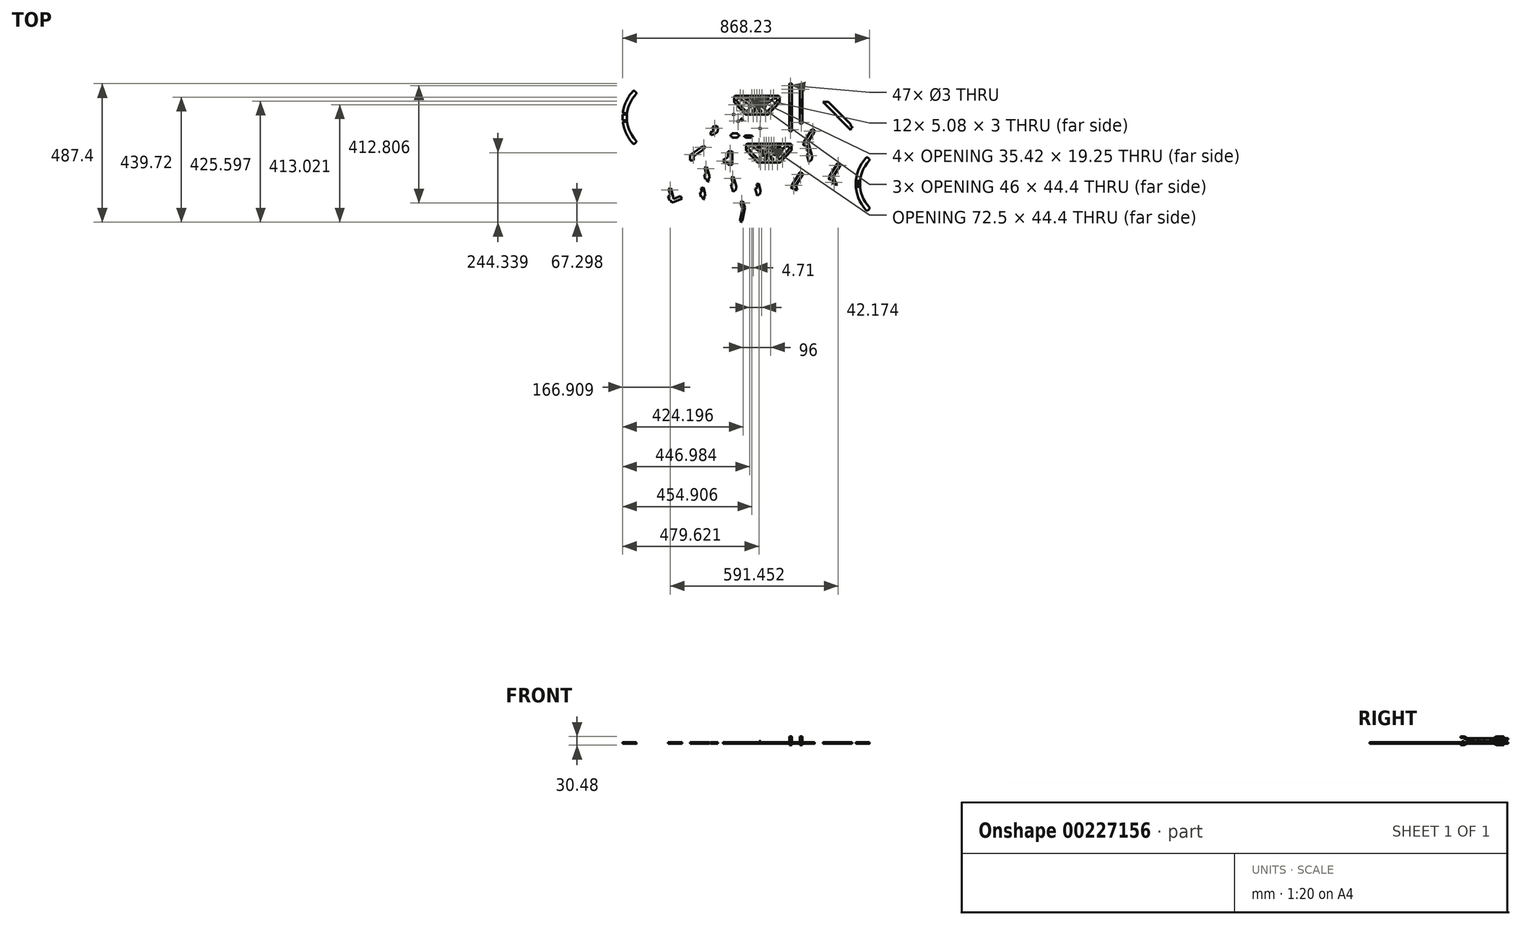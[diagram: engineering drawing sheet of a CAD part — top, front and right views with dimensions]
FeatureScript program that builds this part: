
annotation { "Feature Type Name" : "Feature", "Feature Type Description" : "" }
export const myFeature = defineFeature(function(context is Context, id is Id, definition is map)
    precondition{}
    {
        {
            var Q0;
            Q0=qCreatedBy(makeId("Top.planeOp"),FACE);
            var sketch = newSketch(context, id + "F0", { "sketchPlane" : qUnion([Q0])});
            skLineSegment(sketch, "E0.bottom", {"start": v(11.13, 62.94) * mm, "end": v(-148.87, 62.94) * mm});
            skLineSegment(sketch, "E0.top", {"start": v(11.13, 53.94) * mm, "end": v(-148.87, 53.94) * mm});
            skLineSegment(sketch, "E0.left", {"start": v(11.13, 62.94) * mm, "end": v(11.13, 53.94) * mm});
            skLineSegment(sketch, "E0.right", {"start": v(-148.87, 62.94) * mm, "end": v(-148.87, 53.94) * mm});
            skCircle(sketch, "E1", {"center": v(-127.12, 58.44) * mm, "radius": 1.5 * mm});
            skLineSegment(sketch, "E2.bottom", {"start": v(-43.87, 30.69) * mm, "end": v(-93.87, 30.69) * mm});
            skLineSegment(sketch, "E2.top", {"start": v(-43.87, 21.69) * mm, "end": v(-93.87, 21.69) * mm});
            skLineSegment(sketch, "E2.left", {"start": v(-43.87, 30.69) * mm, "end": v(-43.87, 21.69) * mm});
            skLineSegment(sketch, "E2.right", {"start": v(-93.87, 30.69) * mm, "end": v(-93.87, 21.69) * mm});
            skPoint(sketch, "E2.centerSnap0", {"position": v(-68.87, 53.94) * mm});
            skLineSegment(sketch, "E3", {"start": v(-76.37, 30.69) * mm, "end": v(-76.37, 53.94) * mm});
            skLineSegment(sketch, "E4", {"start": v(-68.87, 62.94) * mm, "end": v(-68.87, 21.69) * mm, "construction": true});
            skLineSegment(sketch, "E5.MirrorCS", {"start": v(-61.37, 30.69) * mm, "end": v(-61.37, 53.94) * mm});
            skPoint(sketch, "E6.centerSnap0", {"position": v(-93.87, 26.19) * mm});
            skCircle(sketch, "E7.MirrorC", {"center": v(-88, 26.19) * mm, "radius": 1.5 * mm});
            skCircle(sketch, "E8", {"center": v(-10.62, 58.44) * mm, "radius": 1.5 * mm});
            skLineSegment(sketch, "E9", {"start": v(-127.12, 58.44) * mm, "end": v(-10.62, 58.44) * mm, "construction": true});
            skLineSegment(sketch, "E10.bottom", {"start": v(-41.37, 6.69) * mm, "end": v(-96.37, 6.69) * mm});
            skLineSegment(sketch, "E10.top", {"start": v(-41.37, -2.31) * mm, "end": v(-96.37, -2.31) * mm});
            skLineSegment(sketch, "E10.left", {"start": v(-41.37, 6.69) * mm, "end": v(-41.37, -2.31) * mm});
            skLineSegment(sketch, "E10.right", {"start": v(-96.37, 6.69) * mm, "end": v(-96.37, -2.31) * mm});
            skLineSegment(sketch, "E11", {"start": v(-76.37, 21.69) * mm, "end": v(-76.37, 6.69) * mm});
            skLineSegment(sketch, "E12", {"start": v(-61.37, 21.69) * mm, "end": v(-61.37, 6.69) * mm});
            skCircle(sketch, "E13", {"center": v(-98.87, 2.19) * mm, "radius": 1.5 * mm});
            skPoint(sketch, "E13.centerSnap0", {"position": v(-96.37, 2.19) * mm});
            skLineSegment(sketch, "E14", {"start": v(-68.87, 21.69) * mm, "end": v(-68.87, -2.31) * mm});
            skCircle(sketch, "E15.MirrorC", {"center": v(-38.87, 2.19) * mm, "radius": 1.5 * mm});
            skLineSegment(sketch, "E16", {"start": v(-96.37, -2.31) * mm, "end": v(-148.87, 53.94) * mm});
            skLineSegment(sketch, "E17", {"start": v(-109.55, -2.31) * mm, "end": v(-96.37, -2.31) * mm});
            skLineSegment(sketch, "E18", {"start": v(-96.37, 6.69) * mm, "end": v(-104.77, 6.69) * mm});
            skLineSegment(sketch, "E19.MirrorCS", {"start": v(-41.37, -2.31) * mm, "end": v(11.13, 53.94) * mm});
            skLineSegment(sketch, "E20.MirrorCS", {"start": v(-28.2, -2.31) * mm, "end": v(-41.37, -2.31) * mm});
            skLineSegment(sketch, "E21.MirrorCS", {"start": v(-41.37, 6.69) * mm, "end": v(-32.97, 6.69) * mm});
            skLineSegment(sketch, "E22", {"start": v(-43.87, 21.69) * mm, "end": v(-32.97, 6.69) * mm});
            skLineSegment(sketch, "E23", {"start": v(-55, 21.69) * mm, "end": v(-44.1, 6.69) * mm});
            skLineSegment(sketch, "E24.MirrorCS", {"start": v(-82.75, 21.69) * mm, "end": v(-93.65, 6.69) * mm});
            skLineSegment(sketch, "E25.MirrorCS", {"start": v(-93.87, 21.69) * mm, "end": v(-104.77, 6.69) * mm});
            skLineSegment(sketch, "E26", {"start": v(2.13, 53.94) * mm, "end": v(2.13, 44.3) * mm});
            skLineSegment(sketch, "E27", {"start": v(11.13, 53.94) * mm, "end": v(11.13, 40.8) * mm});
            skLineSegment(sketch, "E28", {"start": v(11.13, 40.8) * mm, "end": v(-28.2, -2.31) * mm});
            skLineSegment(sketch, "E29.MirrorCS", {"start": v(-148.87, 40.8) * mm, "end": v(-109.55, -2.31) * mm});
            skLineSegment(sketch, "E30.MirrorCS", {"start": v(-148.87, 53.94) * mm, "end": v(-148.87, 40.8) * mm});
            skLineSegment(sketch, "E31.MirrorCS", {"start": v(-139.87, 53.94) * mm, "end": v(-139.87, 44.3) * mm});
            skLineSegment(sketch, "E32", {"start": v(-93.87, 30.69) * mm, "end": v(-129.3, 53.94) * mm});
            skLineSegment(sketch, "E33.MirrorCS", {"start": v(-43.87, 30.69) * mm, "end": v(-8.45, 53.94) * mm});
            skLineSegment(sketch, "E34", {"start": v(-104.18, 6.06) * mm, "end": v(-104.18, -2.31) * mm});
            skLineSegment(sketch, "E35", {"start": v(-93.57, -2.31) * mm, "end": v(-93.57, 6.69) * mm});
            skLineSegment(sketch, "E36", {"start": v(-93.57, 6.69) * mm, "end": v(-82.67, 21.69) * mm});
            skLineSegment(sketch, "E37.MirrorCS", {"start": v(-44.18, 6.69) * mm, "end": v(-55.08, 21.69) * mm});
            skLineSegment(sketch, "E38", {"start": v(-44.18, 6.69) * mm, "end": v(-44.18, -2.31) * mm});
            skLineSegment(sketch, "E39", {"start": v(-93.57, -2.31) * mm, "end": v(-76.13, 21.69) * mm});
            skLineSegment(sketch, "E40.MirrorCS", {"start": v(-44.18, -2.31) * mm, "end": v(-61.62, 21.69) * mm});
            skPoint(sketch, "E41.endSnap0", {"position": v(-111.59, 42.31) * mm});
            skLineSegment(sketch, "E42", {"start": v(-76.37, 30.69) * mm, "end": v(-111.8, 53.94) * mm});
            skLineSegment(sketch, "E43.MirrorCS", {"start": v(-61.37, 30.69) * mm, "end": v(-25.95, 53.94) * mm});
            skCircle(sketch, "E44", {"center": v(-60.12, 58.44) * mm, "radius": 1.5 * mm});
            skCircle(sketch, "E45.MirrorC", {"center": v(-77.62, 58.44) * mm, "radius": 1.5 * mm});
            skLineSegment(sketch, "E46", {"start": v(-82.47, 34.69) * mm, "end": v(-55.28, 34.69) * mm});
            skCircle(sketch, "E47", {"center": v(-49.75, 26.19) * mm, "radius": 2.25 * mm});
            skPoint(sketch, "E48.middle", {"position": v(-75.41, 26.69) * mm});
            skLineSegment(sketch, "E49.bottom", {"start": v(-67.37, 31.27) * mm, "end": v(-70.37, 31.27) * mm});
            skLineSegment(sketch, "E49.top", {"start": v(-67.37, 26.19) * mm, "end": v(-70.37, 26.19) * mm});
            skLineSegment(sketch, "E49.left", {"start": v(-67.37, 31.27) * mm, "end": v(-67.37, 26.19) * mm});
            skLineSegment(sketch, "E49.right", {"start": v(-70.37, 31.27) * mm, "end": v(-70.37, 26.19) * mm});
            skPoint(sketch, "E49.middle", {"position": v(-68.87, 28.73) * mm});
            skLineSegment(sketch, "E50.MirrorCS", {"start": v(-67.37, 21.1) * mm, "end": v(-70.37, 21.1) * mm});
            skLineSegment(sketch, "E51", {"start": v(-79.03, 17.69) * mm, "end": v(-58.71, 17.69) * mm});
            skLineSegment(sketch, "E52", {"start": v(-70.37, 26.19) * mm, "end": v(-70.37, 21.1) * mm});
            skLineSegment(sketch, "E53", {"start": v(-67.37, 26.19) * mm, "end": v(-67.37, 21.1) * mm});
            skPoint(sketch, "E54.centerSnap0", {"position": v(-44.18, 2.19) * mm});
            skLineSegment(sketch, "E55.bottom", {"start": v(45.17, 91.12) * mm, "end": v(54.17, 91.12) * mm});
            skLineSegment(sketch, "E55.top", {"start": v(45.17, -61.38) * mm, "end": v(54.17, -61.38) * mm});
            skLineSegment(sketch, "E55.left", {"start": v(45.17, 91.12) * mm, "end": v(45.17, -61.38) * mm});
            skLineSegment(sketch, "E55.right", {"start": v(54.17, 91.12) * mm, "end": v(54.17, -61.38) * mm});
            skCircle(sketch, "E56", {"center": v(49.67, 86.12) * mm, "radius": 1.5 * mm});
            skPoint(sketch, "E56.centerSnap0", {"position": v(49.67, 91.12) * mm});
            skCircle(sketch, "E57", {"center": v(49.67, 73.42) * mm, "radius": 1.5 * mm});
            skCircle(sketch, "E58", {"center": v(49.67, 98.82) * mm, "radius": 1.5 * mm});
            skLineSegment(sketch, "E59.top", {"start": v(45.17, 106.12) * mm, "end": v(54.17, 106.12) * mm});
            skLineSegment(sketch, "E59.left", {"start": v(45.17, 91.12) * mm, "end": v(45.17, 106.12) * mm});
            skLineSegment(sketch, "E59.right", {"start": v(54.17, 91.12) * mm, "end": v(54.17, 106.12) * mm});
            skCircle(sketch, "E60", {"center": v(49.67, -56.38) * mm, "radius": 1.5 * mm});
            skPoint(sketch, "E60.centerSnap0", {"position": v(49.67, -61.38) * mm});
            skLineSegment(sketch, "E61.bottom", {"start": v(82.38, 91.63) * mm, "end": v(91.38, 91.63) * mm});
            skLineSegment(sketch, "E61.top", {"start": v(82.38, -35.87) * mm, "end": v(91.38, -35.87) * mm});
            skLineSegment(sketch, "E61.left", {"start": v(82.38, 91.63) * mm, "end": v(82.38, -35.87) * mm});
            skLineSegment(sketch, "E61.right", {"start": v(91.38, 91.63) * mm, "end": v(91.38, -35.87) * mm});
            skCircle(sketch, "E62", {"center": v(86.88, 86.63) * mm, "radius": 1.5 * mm});
            skPoint(sketch, "E62.centerSnap0", {"position": v(86.88, 91.63) * mm});
            skCircle(sketch, "E63", {"center": v(86.88, -30.87) * mm, "radius": 1.5 * mm});
            skPoint(sketch, "E63.centerSnap0", {"position": v(86.88, -35.87) * mm});
            skCircle(sketch, "E64", {"center": v(-57.64, -51.35) * mm, "radius": 3 * mm});
            skCircle(sketch, "E65", {"center": v(-57.64, -51.35) * mm, "radius": 1.5 * mm});
            skPoint(sketch, "E66.middle", {"position": v(-68.87, 54.94) * mm});
            skLineSegment(sketch, "E67.bottom", {"start": v(-66.37, 49.4) * mm, "end": v(-71.37, 49.4) * mm});
            skLineSegment(sketch, "E67.top", {"start": v(-66.37, 44.32) * mm, "end": v(-71.37, 44.32) * mm});
            skLineSegment(sketch, "E67.left", {"start": v(-66.37, 49.4) * mm, "end": v(-66.37, 44.32) * mm});
            skLineSegment(sketch, "E67.right", {"start": v(-71.37, 49.4) * mm, "end": v(-71.37, 44.32) * mm});
            skPoint(sketch, "E67.middle", {"position": v(-68.87, 46.86) * mm});
            skLineSegment(sketch, "E68.bottom", {"start": v(-66.37, 38.32) * mm, "end": v(-71.37, 38.32) * mm});
            skLineSegment(sketch, "E68.top", {"start": v(-66.37, 33.24) * mm, "end": v(-71.37, 33.24) * mm});
            skLineSegment(sketch, "E68.left", {"start": v(-66.37, 38.32) * mm, "end": v(-66.37, 33.24) * mm});
            skLineSegment(sketch, "E68.right", {"start": v(-71.37, 38.32) * mm, "end": v(-71.37, 33.24) * mm});
            skPoint(sketch, "E68.middle", {"position": v(-68.87, 35.78) * mm});
            skLineSegment(sketch, "E69.bottom", {"start": v(-66.37, 17.1) * mm, "end": v(-71.37, 17.1) * mm});
            skLineSegment(sketch, "E69.top", {"start": v(-66.37, 12.03) * mm, "end": v(-71.37, 12.03) * mm});
            skLineSegment(sketch, "E69.left", {"start": v(-66.37, 17.1) * mm, "end": v(-66.37, 12.03) * mm});
            skLineSegment(sketch, "E69.right", {"start": v(-71.37, 17.1) * mm, "end": v(-71.37, 12.03) * mm});
            skPoint(sketch, "E69.middle", {"position": v(-68.87, 14.57) * mm});
            skLineSegment(sketch, "E70.bottom", {"start": v(-66.33, 3.69) * mm, "end": v(-71.41, 3.69) * mm});
            skLineSegment(sketch, "E70.top", {"start": v(-66.33, 0.69) * mm, "end": v(-71.41, 0.69) * mm});
            skLineSegment(sketch, "E70.left", {"start": v(-66.33, 3.69) * mm, "end": v(-66.33, 0.69) * mm});
            skLineSegment(sketch, "E70.right", {"start": v(-71.41, 3.69) * mm, "end": v(-71.41, 0.69) * mm});
            skPoint(sketch, "E70.middle", {"position": v(-68.87, 2.19) * mm});
            skPoint(sketch, "E70.middle.positionSnap0", {"position": v(-93.57, 2.19) * mm});
            skPoint(sketch, "E70.centerSnap0", {"position": v(-93.57, 2.19) * mm});
            skLineSegment(sketch, "E71.bottom", {"start": v(-58.83, 3.69) * mm, "end": v(-53.75, 3.69) * mm});
            skLineSegment(sketch, "E71.top", {"start": v(-58.83, 0.69) * mm, "end": v(-53.75, 0.69) * mm});
            skLineSegment(sketch, "E71.left", {"start": v(-58.83, 3.69) * mm, "end": v(-58.83, 0.69) * mm});
            skLineSegment(sketch, "E71.right", {"start": v(-53.75, 3.69) * mm, "end": v(-53.75, 0.69) * mm});
            skPoint(sketch, "E71.middle", {"position": v(-56.3, 2.19) * mm});
            skPoint(sketch, "E72.middle", {"position": v(-46.21, 2.19) * mm});
            skLineSegment(sketch, "E73.MirrorCS", {"start": v(-78.91, 3.69) * mm, "end": v(-84, 3.69) * mm});
            skLineSegment(sketch, "E74.MirrorCS", {"start": v(-78.91, 3.69) * mm, "end": v(-78.91, 0.69) * mm});
            skLineSegment(sketch, "E75.MirrorCS", {"start": v(-84, 3.69) * mm, "end": v(-84, 0.69) * mm});
            skLineSegment(sketch, "E76.MirrorCS", {"start": v(-78.91, 0.69) * mm, "end": v(-84, 0.69) * mm});
            skLineSegment(sketch, "E77.bottom", {"start": v(-136.64, -68.47) * mm, "end": v(-156.32, -68.47) * mm});
            skLineSegment(sketch, "E77.top", {"start": v(-136.64, -83.47) * mm, "end": v(-156.32, -83.47) * mm});
            skLineSegment(sketch, "E77.left", {"start": v(-136.64, -68.47) * mm, "end": v(-136.64, -83.47) * mm});
            skLineSegment(sketch, "E77.right", {"start": v(-156.32, -68.47) * mm, "end": v(-156.32, -83.47) * mm});
            skPoint(sketch, "E77.middle", {"position": v(-146.48, -75.97) * mm});
            skLineSegment(sketch, "E78.bottom", {"start": v(-136.64, -73.47) * mm, "end": v(-131.56, -73.47) * mm});
            skLineSegment(sketch, "E78.top", {"start": v(-136.64, -78.47) * mm, "end": v(-131.56, -78.47) * mm});
            skLineSegment(sketch, "E78.left", {"start": v(-136.64, -73.47) * mm, "end": v(-136.64, -78.47) * mm});
            skLineSegment(sketch, "E78.right", {"start": v(-131.56, -73.47) * mm, "end": v(-131.56, -78.47) * mm});
            skLineSegment(sketch, "E79", {"start": v(-146.48, -68.47) * mm, "end": v(-146.48, -83.47) * mm, "construction": true});
            skLineSegment(sketch, "E80.MirrorCS", {"start": v(-156.32, -78.47) * mm, "end": v(-161.4, -78.47) * mm});
            skLineSegment(sketch, "E81.MirrorCS", {"start": v(-161.4, -73.47) * mm, "end": v(-161.4, -78.47) * mm});
            skLineSegment(sketch, "E82.MirrorCS", {"start": v(-156.32, -73.47) * mm, "end": v(-161.4, -73.47) * mm});
            skLineSegment(sketch, "E83.bottom", {"start": v(-89.01, -76) * mm, "end": v(-108.7, -76) * mm});
            skLineSegment(sketch, "E83.top", {"start": v(-89.01, -84) * mm, "end": v(-108.7, -84) * mm});
            skLineSegment(sketch, "E83.left", {"start": v(-89.01, -76) * mm, "end": v(-89.01, -84) * mm});
            skLineSegment(sketch, "E83.right", {"start": v(-108.7, -76) * mm, "end": v(-108.7, -84) * mm});
            skPoint(sketch, "E83.middle", {"position": v(-98.85, -80) * mm});
            skLineSegment(sketch, "E84.bottom", {"start": v(-89.01, -78) * mm, "end": v(-83.93, -78) * mm});
            skLineSegment(sketch, "E84.top", {"start": v(-89.01, -81) * mm, "end": v(-83.93, -81) * mm});
            skLineSegment(sketch, "E84.left", {"start": v(-89.01, -78) * mm, "end": v(-89.01, -81) * mm});
            skLineSegment(sketch, "E84.right", {"start": v(-83.93, -78) * mm, "end": v(-83.93, -81) * mm});
            skLineSegment(sketch, "E85", {"start": v(-98.85, -76) * mm, "end": v(-98.85, -84) * mm, "construction": true});
            skLineSegment(sketch, "E86.MirrorCS", {"start": v(-108.7, -78) * mm, "end": v(-113.78, -78) * mm});
            skLineSegment(sketch, "E87.MirrorCS", {"start": v(-113.78, -78) * mm, "end": v(-113.78, -81) * mm});
            skLineSegment(sketch, "E88.MirrorCS", {"start": v(-108.7, -81) * mm, "end": v(-113.78, -81) * mm});
            skCircle(sketch, "E89", {"center": v(127.69, -61.42) * mm, "radius": 1.5 * mm});
            skCircle(sketch, "E90", {"center": v(103.99, -99.67) * mm, "radius": 1.5 * mm});
            skLineSegment(sketch, "E91", {"start": v(127.69, -61.42) * mm, "end": v(103.99, -99.67) * mm, "construction": true});
            skLineSegment(sketch, "E92", {"start": v(127.69, -61.42) * mm, "end": v(127.69, -99.67) * mm, "construction": true});
            skLineSegment(sketch, "E93", {"start": v(127.69, -99.67) * mm, "end": v(103.99, -99.67) * mm, "construction": true});
            skLineSegment(sketch, "E94", {"start": v(127.69, -61.42) * mm, "end": v(120.63, -61.42) * mm});
            skLineSegment(sketch, "E95", {"start": v(120.63, -61.42) * mm, "end": v(96.93, -99.67) * mm});
            skLineSegment(sketch, "E96", {"start": v(96.93, -99.67) * mm, "end": v(103.99, -99.67) * mm});
            skLineSegment(sketch, "E97", {"start": v(127.69, -61.42) * mm, "end": v(134.75, -61.42) * mm});
            skLineSegment(sketch, "E98", {"start": v(134.75, -61.42) * mm, "end": v(111.05, -99.67) * mm});
            skPoint(sketch, "E98.endSnap0", {"position": v(115.84, -99.67) * mm});
            skLineSegment(sketch, "E99", {"start": v(95.39, -107.27) * mm, "end": v(103.99, -104.75) * mm});
            skLineSegment(sketch, "E100", {"start": v(103.99, -104.75) * mm, "end": v(114.65, -141.2) * mm});
            skLineSegment(sketch, "E101", {"start": v(114.65, -141.2) * mm, "end": v(106.34, -143.64) * mm});
            skLineSegment(sketch, "E102", {"start": v(106.34, -143.64) * mm, "end": v(113.65, -168.6) * mm});
            skLineSegment(sketch, "E103", {"start": v(113.65, -168.6) * mm, "end": v(124.09, -161.55) * mm});
            skLineSegment(sketch, "E104", {"start": v(124.09, -161.55) * mm, "end": v(125.58, -149.65) * mm});
            skLineSegment(sketch, "E105", {"start": v(125.58, -149.65) * mm, "end": v(111.05, -99.67) * mm});
            skLineSegment(sketch, "E106", {"start": v(95.39, -107.27) * mm, "end": v(94.37, -103.8) * mm});
            skLineSegment(sketch, "E107", {"start": v(96.93, -99.67) * mm, "end": v(94.37, -103.8) * mm});
            skLineSegment(sketch, "E108", {"start": v(95.39, -107.27) * mm, "end": v(105.67, -110.5) * mm});
            skLineSegment(sketch, "E109", {"start": v(106.34, -143.64) * mm, "end": v(112.22, -132.88) * mm});
            skLineSegment(sketch, "E110", {"start": v(120.63, -61.42) * mm, "end": v(124.55, -55.1) * mm});
            skLineSegment(sketch, "E111", {"start": v(124.55, -55.1) * mm, "end": v(134.75, -61.42) * mm});
            skLineSegment(sketch, "E112", {"start": v(124.55, -55.1) * mm, "end": v(126.03, -52.7) * mm});
            skLineSegment(sketch, "E113", {"start": v(126.03, -52.7) * mm, "end": v(136.23, -59.03) * mm});
            skLineSegment(sketch, "E114", {"start": v(136.23, -59.03) * mm, "end": v(134.75, -61.42) * mm});
            skLineSegment(sketch, "E115", {"start": v(95.39, -107.27) * mm, "end": v(97.07, -113.01) * mm});
            skLineSegment(sketch, "E116", {"start": v(97.07, -113.01) * mm, "end": v(105.67, -110.5) * mm});
            skLineSegment(sketch, "E117.bottom", {"start": v(-49.04, 59.94) * mm, "end": v(-54.12, 59.94) * mm});
            skLineSegment(sketch, "E117.top", {"start": v(-49.04, 56.94) * mm, "end": v(-54.12, 56.94) * mm});
            skLineSegment(sketch, "E117.left", {"start": v(-49.04, 59.94) * mm, "end": v(-49.04, 56.94) * mm});
            skLineSegment(sketch, "E117.right", {"start": v(-54.12, 59.94) * mm, "end": v(-54.12, 56.94) * mm});
            skPoint(sketch, "E117.middle", {"position": v(-51.58, 58.44) * mm});
            skLineSegment(sketch, "E118", {"start": v(-49.75, 26.19) * mm, "end": v(-43.87, 26.19) * mm});
            skLineSegment(sketch, "E119.MirrorCS", {"start": v(-88.7, 59.94) * mm, "end": v(-83.62, 59.94) * mm});
            skLineSegment(sketch, "E120.MirrorCS", {"start": v(-83.62, 59.94) * mm, "end": v(-83.62, 56.94) * mm});
            skLineSegment(sketch, "E121.MirrorCS", {"start": v(-88.7, 56.94) * mm, "end": v(-83.62, 56.94) * mm});
            skLineSegment(sketch, "E122.MirrorCS", {"start": v(-88.7, 59.94) * mm, "end": v(-88.7, 56.94) * mm});
            skCircle(sketch, "E123", {"center": v(-134.48, -25.95) * mm, "radius": 1.5 * mm});
            skCircle(sketch, "E124", {"center": v(-134.48, -25.95) * mm, "radius": 3 * mm});
            skCircle(sketch, "E125", {"center": v(-121.7, -20.62) * mm, "radius": 2.25 * mm});
            skCircle(sketch, "E126", {"center": v(-121.7, -20.62) * mm, "radius": 3.75 * mm});
            skLineSegment(sketch, "E127", {"start": v(-93.87, 26.19) * mm, "end": v(-88, 26.19) * mm});
            skLineSegment(sketch, "E128.bottom", {"start": v(-66.33, 59.94) * mm, "end": v(-71.41, 59.94) * mm});
            skLineSegment(sketch, "E128.top", {"start": v(-66.33, 56.94) * mm, "end": v(-71.41, 56.94) * mm});
            skLineSegment(sketch, "E128.left", {"start": v(-66.33, 59.94) * mm, "end": v(-66.33, 56.94) * mm});
            skLineSegment(sketch, "E128.right", {"start": v(-71.41, 59.94) * mm, "end": v(-71.41, 56.94) * mm});
            skPoint(sketch, "E128.middle", {"position": v(-68.87, 58.44) * mm});
            skLineSegment(sketch, "E129.bottom", {"start": v(53.3, -105.74) * mm, "end": v(-106.7, -105.74) * mm});
            skLineSegment(sketch, "E129.top", {"start": v(53.3, -114.74) * mm, "end": v(-106.7, -114.74) * mm});
            skLineSegment(sketch, "E129.left", {"start": v(53.3, -105.74) * mm, "end": v(53.3, -114.74) * mm});
            skLineSegment(sketch, "E129.right", {"start": v(-106.7, -105.74) * mm, "end": v(-106.7, -114.74) * mm});
            skCircle(sketch, "E130", {"center": v(-84.95, -110.24) * mm, "radius": 1.5 * mm});
            skLineSegment(sketch, "E131.bottom", {"start": v(-1.7, -138) * mm, "end": v(-51.7, -138) * mm});
            skLineSegment(sketch, "E131.top", {"start": v(-1.7, -147) * mm, "end": v(-51.7, -147) * mm});
            skLineSegment(sketch, "E131.left", {"start": v(-1.7, -138) * mm, "end": v(-1.7, -147) * mm});
            skLineSegment(sketch, "E131.right", {"start": v(-51.7, -138) * mm, "end": v(-51.7, -147) * mm});
            skPoint(sketch, "E131.centerSnap0", {"position": v(-26.7, -114.74) * mm});
            skLineSegment(sketch, "E132", {"start": v(-34.2, -138) * mm, "end": v(-34.2, -114.74) * mm});
            skLineSegment(sketch, "E133", {"start": v(-26.7, -105.74) * mm, "end": v(-26.7, -147) * mm, "construction": true});
            skLineSegment(sketch, "E134.MirrorCS", {"start": v(-19.2, -138) * mm, "end": v(-19.2, -114.74) * mm});
            skPoint(sketch, "E135.centerSnap0", {"position": v(-51.7, -142.5) * mm});
            skCircle(sketch, "E136.MirrorC", {"center": v(-45.82, -142.5) * mm, "radius": 1.5 * mm});
            skCircle(sketch, "E137", {"center": v(31.55, -110.24) * mm, "radius": 1.5 * mm});
            skLineSegment(sketch, "E138", {"start": v(-84.95, -110.24) * mm, "end": v(31.55, -110.24) * mm, "construction": true});
            skLineSegment(sketch, "E139.bottom", {"start": v(0.8, -162) * mm, "end": v(-54.2, -162) * mm});
            skLineSegment(sketch, "E139.top", {"start": v(0.8, -171) * mm, "end": v(-54.2, -171) * mm});
            skLineSegment(sketch, "E139.left", {"start": v(0.8, -162) * mm, "end": v(0.8, -171) * mm});
            skLineSegment(sketch, "E139.right", {"start": v(-54.2, -162) * mm, "end": v(-54.2, -171) * mm});
            skLineSegment(sketch, "E140", {"start": v(-34.2, -147) * mm, "end": v(-34.2, -162) * mm});
            skLineSegment(sketch, "E141", {"start": v(-19.2, -147) * mm, "end": v(-19.2, -162) * mm});
            skCircle(sketch, "E142", {"center": v(-56.7, -166.5) * mm, "radius": 1.5 * mm});
            skPoint(sketch, "E142.centerSnap0", {"position": v(-54.2, -166.5) * mm});
            skLineSegment(sketch, "E143", {"start": v(-26.7, -147) * mm, "end": v(-26.7, -171) * mm});
            skCircle(sketch, "E144.MirrorC", {"center": v(3.3, -166.5) * mm, "radius": 1.5 * mm});
            skLineSegment(sketch, "E145", {"start": v(-54.2, -171) * mm, "end": v(-106.7, -114.74) * mm});
            skLineSegment(sketch, "E146", {"start": v(-67.37, -171) * mm, "end": v(-54.2, -171) * mm});
            skLineSegment(sketch, "E147", {"start": v(-54.2, -162) * mm, "end": v(-62.6, -162) * mm});
            skLineSegment(sketch, "E148.MirrorCS", {"start": v(0.8, -171) * mm, "end": v(53.3, -114.74) * mm});
            skLineSegment(sketch, "E149.MirrorCS", {"start": v(13.98, -171) * mm, "end": v(0.8, -171) * mm});
            skLineSegment(sketch, "E150.MirrorCS", {"start": v(0.8, -162) * mm, "end": v(9.2, -162) * mm});
            skLineSegment(sketch, "E151", {"start": v(-1.7, -147) * mm, "end": v(9.2, -162) * mm});
            skLineSegment(sketch, "E152", {"start": v(-12.82, -147) * mm, "end": v(-1.92, -162) * mm});
            skLineSegment(sketch, "E153.MirrorCS", {"start": v(-40.57, -147) * mm, "end": v(-51.47, -162) * mm});
            skLineSegment(sketch, "E154.MirrorCS", {"start": v(-51.7, -147) * mm, "end": v(-62.6, -162) * mm});
            skLineSegment(sketch, "E155", {"start": v(44.3, -114.74) * mm, "end": v(44.3, -124.39) * mm});
            skLineSegment(sketch, "E156", {"start": v(53.3, -114.74) * mm, "end": v(53.3, -127.87) * mm});
            skLineSegment(sketch, "E157", {"start": v(53.3, -127.87) * mm, "end": v(13.98, -171) * mm});
            skLineSegment(sketch, "E158.MirrorCS", {"start": v(-106.7, -127.87) * mm, "end": v(-67.37, -171) * mm});
            skLineSegment(sketch, "E159.MirrorCS", {"start": v(-106.7, -114.74) * mm, "end": v(-106.7, -127.87) * mm});
            skLineSegment(sketch, "E160.MirrorCS", {"start": v(-97.7, -114.74) * mm, "end": v(-97.7, -124.39) * mm});
            skLineSegment(sketch, "E161", {"start": v(-51.7, -138) * mm, "end": v(-87.12, -114.74) * mm});
            skLineSegment(sketch, "E162.MirrorCS", {"start": v(-1.7, -138) * mm, "end": v(33.73, -114.74) * mm});
            skLineSegment(sketch, "E163", {"start": v(-62, -162.63) * mm, "end": v(-62, -171) * mm});
            skLineSegment(sketch, "E164", {"start": v(-51.4, -171) * mm, "end": v(-51.4, -162) * mm});
            skLineSegment(sketch, "E165", {"start": v(-51.4, -162) * mm, "end": v(-40.5, -147) * mm});
            skLineSegment(sketch, "E166.MirrorCS", {"start": v(-2, -162) * mm, "end": v(-12.9, -147) * mm});
            skLineSegment(sketch, "E167", {"start": v(-2, -162) * mm, "end": v(-2, -171) * mm});
            skLineSegment(sketch, "E168", {"start": v(-51.4, -171) * mm, "end": v(-33.95, -147) * mm});
            skLineSegment(sketch, "E169.MirrorCS", {"start": v(-2, -171) * mm, "end": v(-19.45, -147) * mm});
            skPoint(sketch, "E170.endSnap0", {"position": v(-69.41, -126.37) * mm});
            skLineSegment(sketch, "E171", {"start": v(-34.2, -138) * mm, "end": v(-69.62, -114.74) * mm});
            skLineSegment(sketch, "E172.MirrorCS", {"start": v(-19.2, -138) * mm, "end": v(16.23, -114.74) * mm});
            skCircle(sketch, "E173", {"center": v(-17.95, -110.24) * mm, "radius": 1.5 * mm});
            skCircle(sketch, "E174.MirrorC", {"center": v(-35.45, -110.24) * mm, "radius": 1.5 * mm});
            skLineSegment(sketch, "E175", {"start": v(-40.3, -134) * mm, "end": v(-13.1, -134) * mm});
            skCircle(sketch, "E176", {"center": v(-7.57, -142.5) * mm, "radius": 2.25 * mm});
            skPoint(sketch, "E177.middle", {"position": v(-33.24, -142) * mm});
            skLineSegment(sketch, "E178.bottom", {"start": v(-25.2, -137.41) * mm, "end": v(-28.2, -137.41) * mm});
            skLineSegment(sketch, "E178.top", {"start": v(-25.2, -142.5) * mm, "end": v(-28.2, -142.5) * mm});
            skLineSegment(sketch, "E178.left", {"start": v(-25.2, -137.41) * mm, "end": v(-25.2, -142.5) * mm});
            skLineSegment(sketch, "E178.right", {"start": v(-28.2, -137.41) * mm, "end": v(-28.2, -142.5) * mm});
            skPoint(sketch, "E178.middle", {"position": v(-26.7, -139.95) * mm});
            skLineSegment(sketch, "E179.MirrorCS", {"start": v(-25.2, -147.57) * mm, "end": v(-28.2, -147.57) * mm});
            skLineSegment(sketch, "E180", {"start": v(-36.86, -151) * mm, "end": v(-16.54, -151) * mm});
            skLineSegment(sketch, "E181", {"start": v(-28.2, -142.5) * mm, "end": v(-28.2, -147.57) * mm});
            skLineSegment(sketch, "E182", {"start": v(-25.2, -142.5) * mm, "end": v(-25.2, -147.57) * mm});
            skPoint(sketch, "E183.centerSnap0", {"position": v(-2, -166.5) * mm});
            skPoint(sketch, "E184.middle", {"position": v(-26.7, -113.74) * mm});
            skLineSegment(sketch, "E185.bottom", {"start": v(-24.2, -119.28) * mm, "end": v(-29.2, -119.28) * mm});
            skLineSegment(sketch, "E185.top", {"start": v(-24.2, -124.36) * mm, "end": v(-29.2, -124.36) * mm});
            skLineSegment(sketch, "E185.left", {"start": v(-24.2, -119.28) * mm, "end": v(-24.2, -124.36) * mm});
            skLineSegment(sketch, "E185.right", {"start": v(-29.2, -119.28) * mm, "end": v(-29.2, -124.36) * mm});
            skPoint(sketch, "E185.middle", {"position": v(-26.7, -121.82) * mm});
            skPoint(sketch, "E186.middle", {"position": v(-26.7, -132.9) * mm});
            skLineSegment(sketch, "E187.bottom", {"start": v(-24.2, -151.57) * mm, "end": v(-29.2, -151.57) * mm});
            skLineSegment(sketch, "E187.top", {"start": v(-24.2, -156.65) * mm, "end": v(-29.2, -156.65) * mm});
            skLineSegment(sketch, "E187.left", {"start": v(-24.2, -151.57) * mm, "end": v(-24.2, -156.65) * mm});
            skLineSegment(sketch, "E187.right", {"start": v(-29.2, -151.57) * mm, "end": v(-29.2, -156.65) * mm});
            skPoint(sketch, "E187.middle", {"position": v(-26.7, -154.11) * mm});
            skLineSegment(sketch, "E188.bottom", {"start": v(-24.16, -165) * mm, "end": v(-29.24, -165) * mm});
            skLineSegment(sketch, "E188.top", {"start": v(-24.16, -168) * mm, "end": v(-29.24, -168) * mm});
            skLineSegment(sketch, "E188.left", {"start": v(-24.16, -165) * mm, "end": v(-24.16, -168) * mm});
            skLineSegment(sketch, "E188.right", {"start": v(-29.24, -165) * mm, "end": v(-29.24, -168) * mm});
            skPoint(sketch, "E188.middle", {"position": v(-26.7, -166.5) * mm});
            skPoint(sketch, "E188.middle.positionSnap0", {"position": v(-51.4, -166.5) * mm});
            skPoint(sketch, "E188.centerSnap0", {"position": v(-51.4, -166.5) * mm});
            skLineSegment(sketch, "E189.bottom", {"start": v(-16.66, -165) * mm, "end": v(-11.58, -165) * mm});
            skLineSegment(sketch, "E189.top", {"start": v(-16.66, -168) * mm, "end": v(-11.58, -168) * mm});
            skLineSegment(sketch, "E189.left", {"start": v(-16.66, -165) * mm, "end": v(-16.66, -168) * mm});
            skLineSegment(sketch, "E189.right", {"start": v(-11.58, -165) * mm, "end": v(-11.58, -168) * mm});
            skPoint(sketch, "E189.middle", {"position": v(-14.12, -166.5) * mm});
            skPoint(sketch, "E190.middle", {"position": v(-4.04, -166.5) * mm});
            skLineSegment(sketch, "E191.MirrorCS", {"start": v(-36.74, -165) * mm, "end": v(-41.82, -165) * mm});
            skLineSegment(sketch, "E192.MirrorCS", {"start": v(-36.74, -165) * mm, "end": v(-36.74, -168) * mm});
            skLineSegment(sketch, "E193.MirrorCS", {"start": v(-41.82, -165) * mm, "end": v(-41.82, -168) * mm});
            skLineSegment(sketch, "E194.MirrorCS", {"start": v(-36.74, -168) * mm, "end": v(-41.82, -168) * mm});
            skLineSegment(sketch, "E195.bottom", {"start": v(-6.87, -108.74) * mm, "end": v(-11.95, -108.74) * mm});
            skLineSegment(sketch, "E195.top", {"start": v(-6.87, -111.74) * mm, "end": v(-11.95, -111.74) * mm});
            skLineSegment(sketch, "E195.left", {"start": v(-6.87, -108.74) * mm, "end": v(-6.87, -111.74) * mm});
            skLineSegment(sketch, "E195.right", {"start": v(-11.95, -108.74) * mm, "end": v(-11.95, -111.74) * mm});
            skPoint(sketch, "E195.middle", {"position": v(-9.4, -110.24) * mm});
            skLineSegment(sketch, "E196", {"start": v(-7.57, -142.5) * mm, "end": v(-1.7, -142.5) * mm});
            skLineSegment(sketch, "E197.MirrorCS", {"start": v(-46.53, -108.74) * mm, "end": v(-41.45, -108.74) * mm});
            skLineSegment(sketch, "E198.MirrorCS", {"start": v(-41.45, -108.74) * mm, "end": v(-41.45, -111.74) * mm});
            skLineSegment(sketch, "E199.MirrorCS", {"start": v(-46.53, -111.74) * mm, "end": v(-41.45, -111.74) * mm});
            skLineSegment(sketch, "E200.MirrorCS", {"start": v(-46.53, -108.74) * mm, "end": v(-46.53, -111.74) * mm});
            skLineSegment(sketch, "E201", {"start": v(-51.7, -142.5) * mm, "end": v(-45.82, -142.5) * mm});
            skLineSegment(sketch, "E202.bottom", {"start": v(-24.16, -108.74) * mm, "end": v(-29.24, -108.74) * mm});
            skLineSegment(sketch, "E202.top", {"start": v(-24.16, -111.74) * mm, "end": v(-29.24, -111.74) * mm});
            skLineSegment(sketch, "E202.left", {"start": v(-24.16, -108.74) * mm, "end": v(-24.16, -111.74) * mm});
            skLineSegment(sketch, "E202.right", {"start": v(-29.24, -108.74) * mm, "end": v(-29.24, -111.74) * mm});
            skPoint(sketch, "E202.middle", {"position": v(-26.7, -110.24) * mm});
            skLineSegment(sketch, "E203", {"start": v(261.92, -36.97) * mm, "end": v(261.92, -56.97) * mm});
            skLineSegment(sketch, "E204", {"start": v(261.92, -56.97) * mm, "end": v(163.29, 41.66) * mm});
            skLineSegment(sketch, "E205", {"start": v(163.29, 41.66) * mm, "end": v(163.29, 61.66) * mm});
            skLineSegment(sketch, "E206", {"start": v(163.29, 61.66) * mm, "end": v(261.92, -36.97) * mm});
            skLineSegment(sketch, "E207", {"start": v(163.29, 41.66) * mm, "end": v(183.29, 41.66) * mm});
            skLineSegment(sketch, "E208.bottom", {"start": v(170.79, 41.66) * mm, "end": v(175.79, 41.66) * mm});
            skLineSegment(sketch, "E208.top", {"start": v(170.79, 46.74) * mm, "end": v(175.79, 46.74) * mm});
            skLineSegment(sketch, "E208.left", {"start": v(170.79, 41.66) * mm, "end": v(170.79, 46.74) * mm});
            skLineSegment(sketch, "E208.right", {"start": v(175.79, 41.66) * mm, "end": v(175.79, 46.74) * mm});
            skLineSegment(sketch, "E209.bottom", {"start": v(261.92, -44.47) * mm, "end": v(267, -44.47) * mm});
            skLineSegment(sketch, "E209.top", {"start": v(261.92, -49.47) * mm, "end": v(267, -49.47) * mm});
            skLineSegment(sketch, "E209.left", {"start": v(261.92, -44.47) * mm, "end": v(261.92, -49.47) * mm});
            skLineSegment(sketch, "E209.right", {"start": v(267, -44.47) * mm, "end": v(267, -49.47) * mm});
            skLineSegment(sketch, "E210.bottom", {"start": v(-24.2, -128.02) * mm, "end": v(-29.2, -128.02) * mm});
            skLineSegment(sketch, "E210.top", {"start": v(-24.2, -133.1) * mm, "end": v(-29.2, -133.1) * mm});
            skLineSegment(sketch, "E210.left", {"start": v(-24.2, -128.02) * mm, "end": v(-24.2, -133.1) * mm});
            skLineSegment(sketch, "E210.right", {"start": v(-29.2, -128.02) * mm, "end": v(-29.2, -133.1) * mm});
            skPoint(sketch, "E210.middle", {"position": v(-26.7, -130.56) * mm});
            skCircle(sketch, "E211", {"center": v(-406.07, -12.56) * mm, "radius": 120 * mm});
            skCircle(sketch, "E212", {"center": v(-406.07, -12.56) * mm, "radius": 135 * mm});
            skLineSegment(sketch, "E213", {"start": v(-406.07, 122.44) * mm, "end": v(-406.07, -147.56) * mm});
            skLineSegment(sketch, "E214", {"start": v(-406.07, -12.56) * mm, "end": v(-541.07, -12.56) * mm, "construction": true});
            skPoint(sketch, "E215.middle", {"position": v(-523.61, -12.56) * mm});
            skLineSegment(sketch, "E216", {"start": v(103.99, -99.67) * mm, "end": v(136.1, -90.33) * mm, "construction": true});
            skLineSegment(sketch, "E217", {"start": v(136.1, -90.33) * mm, "end": v(127.69, -61.42) * mm, "construction": true});
            skCircle(sketch, "E218", {"center": v(-255.87, -118.2) * mm, "radius": 1.5 * mm});
            skCircle(sketch, "E219", {"center": v(-292.67, -144.1) * mm, "radius": 1.5 * mm});
            skLineSegment(sketch, "E220", {"start": v(-255.87, -118.2) * mm, "end": v(-257.18, -139.48) * mm, "construction": true});
            skLineSegment(sketch, "E221", {"start": v(-257.18, -139.48) * mm, "end": v(-292.67, -144.1) * mm, "construction": true});
            skLineSegment(sketch, "E222", {"start": v(-255.87, -118.2) * mm, "end": v(-292.67, -144.1) * mm, "construction": true});
            skLineSegment(sketch, "E223", {"start": v(-255.87, -118.2) * mm, "end": v(-259.32, -113.3) * mm});
            skLineSegment(sketch, "E224", {"start": v(-259.32, -113.3) * mm, "end": v(-303.57, -144.43) * mm});
            skLineSegment(sketch, "E225", {"start": v(-303.57, -144.43) * mm, "end": v(-303.57, -164.43) * mm});
            skLineSegment(sketch, "E226", {"start": v(-279.88, -142.44) * mm, "end": v(-238.46, -113.3) * mm});
            skLineSegment(sketch, "E227", {"start": v(-259.32, -113.3) * mm, "end": v(-245.37, -103.49) * mm});
            skLineSegment(sketch, "E228", {"start": v(-245.37, -103.49) * mm, "end": v(-238.46, -113.3) * mm});
            skLineSegment(sketch, "E229", {"start": v(-248.32, -120.24) * mm, "end": v(-255.23, -110.42) * mm});
            skLineSegment(sketch, "E230", {"start": v(-279.88, -142.44) * mm, "end": v(-296.67, -154.24) * mm});
            skLineSegment(sketch, "E231", {"start": v(-303.57, -144.43) * mm, "end": v(-296.67, -154.24) * mm});
            skLineSegment(sketch, "E232", {"start": v(-291.57, -164.43) * mm, "end": v(-303.57, -164.43) * mm});
            skLineSegment(sketch, "E233", {"start": v(-291.57, -164.43) * mm, "end": v(-291.57, -150.66) * mm});
            skLineSegment(sketch, "E234.bottom", {"start": v(-300.07, -164.43) * mm, "end": v(-295.07, -164.43) * mm});
            skLineSegment(sketch, "E234.top", {"start": v(-300.07, -174.59) * mm, "end": v(-295.07, -174.59) * mm});
            skLineSegment(sketch, "E234.left", {"start": v(-300.07, -164.43) * mm, "end": v(-300.07, -174.59) * mm});
            skLineSegment(sketch, "E234.right", {"start": v(-295.07, -164.43) * mm, "end": v(-295.07, -174.59) * mm});
            skLineSegment(sketch, "E235", {"start": v(-406.07, -12.56) * mm, "end": v(-473.57, 104.35) * mm});
            skLineSegment(sketch, "E236", {"start": v(-406.07, -12.56) * mm, "end": v(-338.57, -129.47) * mm});
            skLineSegment(sketch, "E237.MirrorCS", {"start": v(-406.07, -12.56) * mm, "end": v(-338.57, 104.35) * mm});
            skLineSegment(sketch, "E238.MirrorCS", {"start": v(-406.07, -12.56) * mm, "end": v(-473.57, -129.47) * mm});
            skLineSegment(sketch, "E239", {"start": v(-297.57, -164.43) * mm, "end": v(-297.57, -152.96) * mm});
            skCircle(sketch, "E240", {"center": v(-163.13, -137.41) * mm, "radius": 1.5 * mm});
            skCircle(sketch, "E241", {"center": v(-179.87, -166.4) * mm, "radius": 1.5 * mm});
            skLineSegment(sketch, "E242.bottom", {"start": v(-170.63, -132.41) * mm, "end": v(-155.63, -132.41) * mm});
            skLineSegment(sketch, "E242.top", {"start": v(-170.63, -179.73) * mm, "end": v(-155.63, -179.73) * mm});
            skLineSegment(sketch, "E242.left", {"start": v(-170.63, -132.41) * mm, "end": v(-170.63, -179.73) * mm});
            skLineSegment(sketch, "E242.right", {"start": v(-155.63, -132.41) * mm, "end": v(-155.63, -179.73) * mm});
            skPoint(sketch, "E243", {"position": v(-163.13, -132.41) * mm});
            skLineSegment(sketch, "E244", {"start": v(-170.63, -161.07) * mm, "end": v(-179.87, -166.4) * mm});
            skLineSegment(sketch, "E245", {"start": v(-170.63, -152.41) * mm, "end": v(-187.95, -162.41) * mm});
            skLineSegment(sketch, "E246", {"start": v(-187.95, -162.41) * mm, "end": v(-180.45, -175.4) * mm});
            skLineSegment(sketch, "E247", {"start": v(-180.45, -175.4) * mm, "end": v(-170.63, -169.73) * mm});
            skLineSegment(sketch, "E248.bottom", {"start": v(-165.63, -179.73) * mm, "end": v(-160.63, -179.73) * mm});
            skLineSegment(sketch, "E248.top", {"start": v(-165.63, -184.81) * mm, "end": v(-160.63, -184.81) * mm});
            skLineSegment(sketch, "E248.left", {"start": v(-165.63, -179.73) * mm, "end": v(-165.63, -184.81) * mm});
            skLineSegment(sketch, "E248.right", {"start": v(-160.63, -179.73) * mm, "end": v(-160.63, -184.81) * mm});
            skCircle(sketch, "E249", {"center": v(-163.13, -174.73) * mm, "radius": 1.5 * mm});
            skPoint(sketch, "E249.centerSnap0", {"position": v(-163.13, -179.73) * mm});
            skLineSegment(sketch, "E250", {"start": v(-253.18, -113.33) * mm, "end": v(-267.26, -118.89) * mm});
            skLineSegment(sketch, "E251.MirrorCS", {"start": v(-250.37, -117.33) * mm, "end": v(-260.35, -128.7) * mm});
            skLineSegment(sketch, "E252.bottom", {"start": v(-540.7, -2.4) * mm, "end": v(-528.7, -2.4) * mm});
            skLineSegment(sketch, "E252.top", {"start": v(-540.7, 2.68) * mm, "end": v(-528.7, 2.68) * mm});
            skLineSegment(sketch, "E252.left", {"start": v(-540.7, -2.4) * mm, "end": v(-540.7, 2.68) * mm});
            skLineSegment(sketch, "E252.right", {"start": v(-528.7, -2.4) * mm, "end": v(-528.7, 2.68) * mm});
            skLineSegment(sketch, "E253.MirrorCS", {"start": v(-540.7, -22.72) * mm, "end": v(-528.7, -22.72) * mm});
            skLineSegment(sketch, "E254.MirrorCS", {"start": v(-540.7, -27.8) * mm, "end": v(-528.7, -27.8) * mm});
            skLineSegment(sketch, "E255.MirrorCS", {"start": v(-528.7, -22.72) * mm, "end": v(-528.7, -27.8) * mm});
            skLineSegment(sketch, "E256.MirrorCS", {"start": v(-540.7, -22.72) * mm, "end": v(-540.7, -27.8) * mm});
            skCircle(sketch, "E257", {"center": v(113.78, -147.7) * mm, "radius": 1.5 * mm});
            skLineSegment(sketch, "E258", {"start": v(113.78, -147.7) * mm, "end": v(112.1, -141.95) * mm});
            skLineSegment(sketch, "E259", {"start": v(113.78, -147.7) * mm, "end": v(108.02, -149.4) * mm});
            skCircle(sketch, "E260", {"center": v(-203.91, 35.97) * mm, "radius": 1.5 * mm});
            skCircle(sketch, "E261", {"center": v(-227.61, -2.28) * mm, "radius": 1.5 * mm});
            skLineSegment(sketch, "E262", {"start": v(-203.91, 35.97) * mm, "end": v(-227.61, -2.28) * mm, "construction": true});
            skLineSegment(sketch, "E263", {"start": v(-203.91, 35.97) * mm, "end": v(-203.91, -2.28) * mm, "construction": true});
            skLineSegment(sketch, "E264", {"start": v(-203.91, -2.28) * mm, "end": v(-227.61, -2.28) * mm, "construction": true});
            skLineSegment(sketch, "E265", {"start": v(-203.91, 35.97) * mm, "end": v(-210.97, 35.97) * mm});
            skLineSegment(sketch, "E266", {"start": v(-210.97, 35.97) * mm, "end": v(-234.67, -2.28) * mm});
            skLineSegment(sketch, "E267", {"start": v(-234.67, -2.28) * mm, "end": v(-227.61, -2.28) * mm});
            skLineSegment(sketch, "E268", {"start": v(-203.91, 35.97) * mm, "end": v(-196.85, 35.97) * mm});
            skLineSegment(sketch, "E269", {"start": v(-196.85, 35.97) * mm, "end": v(-220.55, -2.28) * mm});
            skPoint(sketch, "E269.endSnap0", {"position": v(-215.76, -2.28) * mm});
            skLineSegment(sketch, "E270", {"start": v(-236.21, -9.88) * mm, "end": v(-227.61, -7.36) * mm});
            skLineSegment(sketch, "E271", {"start": v(-227.61, -7.36) * mm, "end": v(-216.95, -43.8) * mm});
            skLineSegment(sketch, "E272", {"start": v(-216.95, -43.8) * mm, "end": v(-225.26, -46.24) * mm});
            skLineSegment(sketch, "E273", {"start": v(-225.26, -46.24) * mm, "end": v(-217.95, -71.22) * mm});
            skLineSegment(sketch, "E274", {"start": v(-217.95, -71.22) * mm, "end": v(-207.51, -64.16) * mm});
            skLineSegment(sketch, "E275", {"start": v(-207.51, -64.16) * mm, "end": v(-206.02, -52.25) * mm});
            skLineSegment(sketch, "E276", {"start": v(-206.02, -52.25) * mm, "end": v(-220.55, -2.28) * mm});
            skLineSegment(sketch, "E277", {"start": v(-236.21, -9.88) * mm, "end": v(-237.23, -6.4) * mm});
            skLineSegment(sketch, "E278", {"start": v(-234.67, -2.28) * mm, "end": v(-237.23, -6.4) * mm});
            skLineSegment(sketch, "E279", {"start": v(-236.21, -9.88) * mm, "end": v(-225.93, -13.1) * mm});
            skLineSegment(sketch, "E280", {"start": v(-225.26, -46.24) * mm, "end": v(-219.38, -35.49) * mm});
            skLineSegment(sketch, "E281", {"start": v(-210.97, 35.97) * mm, "end": v(-207.05, 42.3) * mm});
            skLineSegment(sketch, "E282", {"start": v(-207.05, 42.3) * mm, "end": v(-196.85, 35.97) * mm});
            skLineSegment(sketch, "E283", {"start": v(-207.05, 42.3) * mm, "end": v(-205.57, 44.69) * mm});
            skLineSegment(sketch, "E284", {"start": v(-205.57, 44.69) * mm, "end": v(-195.37, 38.37) * mm});
            skLineSegment(sketch, "E285", {"start": v(-195.37, 38.37) * mm, "end": v(-196.85, 35.97) * mm});
            skLineSegment(sketch, "E286", {"start": v(-236.21, -9.88) * mm, "end": v(-234.53, -15.62) * mm});
            skLineSegment(sketch, "E287", {"start": v(-234.53, -15.62) * mm, "end": v(-225.93, -13.1) * mm});
            skLineSegment(sketch, "E288", {"start": v(-227.61, -2.28) * mm, "end": v(-195.5, 7.06) * mm, "construction": true});
            skLineSegment(sketch, "E289", {"start": v(-195.5, 7.06) * mm, "end": v(-203.91, 35.97) * mm, "construction": true});
            skCircle(sketch, "E290", {"center": v(-217.82, -50.32) * mm, "radius": 1.5 * mm});
            skLineSegment(sketch, "E291", {"start": v(-217.82, -50.32) * mm, "end": v(-219.5, -44.56) * mm});
            skLineSegment(sketch, "E292", {"start": v(-217.82, -50.32) * mm, "end": v(-223.57, -52) * mm});
            skLineSegment(sketch, "E293", {"start": v(-216.95, -43.8) * mm, "end": v(-209.14, -41.52) * mm});
            skLineSegment(sketch, "E294", {"start": v(-217.95, -71.22) * mm, "end": v(-229.47, -74.58) * mm});
            skLineSegment(sketch, "E295", {"start": v(-229.47, -74.58) * mm, "end": v(-232.32, -64.83) * mm});
            skLineSegment(sketch, "E296", {"start": v(-232.32, -64.83) * mm, "end": v(-220.8, -61.46) * mm});
            skLineSegment(sketch, "E297", {"start": v(-406.07, -12.56) * mm, "end": v(-501.53, 82.9) * mm});
            skLineSegment(sketch, "E298.MirrorCS", {"start": v(-406.07, -12.56) * mm, "end": v(-501.53, -108.02) * mm});
            skCircle(sketch, "E299", {"center": v(414.01, -246.9) * mm, "radius": 135 * mm});
            skCircle(sketch, "E300", {"center": v(414.01, -246.9) * mm, "radius": 120 * mm});
            skLineSegment(sketch, "E301", {"start": v(414.01, -111.9) * mm, "end": v(414.01, -381.9) * mm});
            skLineSegment(sketch, "E302", {"start": v(414.01, -246.9) * mm, "end": v(279.01, -246.9) * mm});
            skLineSegment(sketch, "E303", {"start": v(414.01, -246.9) * mm, "end": v(318.55, -151.45) * mm});
            skLineSegment(sketch, "E304.MirrorCS", {"start": v(414.01, -246.9) * mm, "end": v(318.55, -342.37) * mm});
            skLineSegment(sketch, "E305", {"start": v(109.32, -122.98) * mm, "end": v(117.16, -120.68) * mm, "construction": true});
            skCircle(sketch, "E306", {"center": v(113.24, -121.83) * mm, "radius": 1.5 * mm});
            skLineSegment(sketch, "E307", {"start": v(112.22, -132.88) * mm, "end": v(120.04, -130.6) * mm});
            skCircle(sketch, "E308", {"center": v(217.3, -181.43) * mm, "radius": 1.5 * mm});
            skCircle(sketch, "E309", {"center": v(193.6, -219.69) * mm, "radius": 1.5 * mm});
            skLineSegment(sketch, "E310", {"start": v(217.3, -181.43) * mm, "end": v(193.6, -219.69) * mm, "construction": true});
            skLineSegment(sketch, "E311", {"start": v(217.3, -181.43) * mm, "end": v(217.3, -219.69) * mm, "construction": true});
            skLineSegment(sketch, "E312", {"start": v(217.3, -219.69) * mm, "end": v(193.6, -219.69) * mm, "construction": true});
            skLineSegment(sketch, "E313", {"start": v(217.3, -181.43) * mm, "end": v(210.23, -181.43) * mm});
            skLineSegment(sketch, "E314", {"start": v(210.23, -181.43) * mm, "end": v(186.53, -219.69) * mm});
            skLineSegment(sketch, "E315", {"start": v(186.53, -219.69) * mm, "end": v(193.6, -219.69) * mm});
            skLineSegment(sketch, "E316", {"start": v(217.3, -181.43) * mm, "end": v(224.35, -181.43) * mm});
            skLineSegment(sketch, "E317", {"start": v(224.35, -181.43) * mm, "end": v(200.65, -219.69) * mm});
            skPoint(sketch, "E317.endSnap0", {"position": v(205.44, -219.69) * mm});
            skLineSegment(sketch, "E318", {"start": v(185, -227.28) * mm, "end": v(193.6, -224.77) * mm});
            skLineSegment(sketch, "E319", {"start": v(193.6, -224.77) * mm, "end": v(204.26, -261.22) * mm});
            skLineSegment(sketch, "E320", {"start": v(204.26, -261.22) * mm, "end": v(195.94, -263.65) * mm});
            skLineSegment(sketch, "E321", {"start": v(195.94, -263.65) * mm, "end": v(203.25, -288.62) * mm});
            skLineSegment(sketch, "E322", {"start": v(203.25, -288.62) * mm, "end": v(213.69, -281.57) * mm});
            skLineSegment(sketch, "E323", {"start": v(213.69, -281.57) * mm, "end": v(215.19, -269.66) * mm});
            skLineSegment(sketch, "E324", {"start": v(215.19, -269.66) * mm, "end": v(200.65, -219.69) * mm});
            skLineSegment(sketch, "E325", {"start": v(185, -227.28) * mm, "end": v(183.98, -223.81) * mm});
            skLineSegment(sketch, "E326", {"start": v(186.53, -219.69) * mm, "end": v(183.98, -223.81) * mm});
            skLineSegment(sketch, "E327", {"start": v(185, -227.28) * mm, "end": v(195.27, -230.51) * mm});
            skLineSegment(sketch, "E328", {"start": v(195.94, -263.65) * mm, "end": v(201.82, -252.9) * mm});
            skLineSegment(sketch, "E329", {"start": v(210.23, -181.43) * mm, "end": v(214.15, -175.11) * mm});
            skLineSegment(sketch, "E330", {"start": v(214.15, -175.11) * mm, "end": v(224.35, -181.43) * mm});
            skLineSegment(sketch, "E331", {"start": v(214.15, -175.11) * mm, "end": v(215.63, -172.72) * mm});
            skLineSegment(sketch, "E332", {"start": v(215.63, -172.72) * mm, "end": v(225.83, -179.04) * mm});
            skLineSegment(sketch, "E333", {"start": v(225.83, -179.04) * mm, "end": v(224.35, -181.43) * mm});
            skLineSegment(sketch, "E334", {"start": v(185, -227.28) * mm, "end": v(186.67, -233.03) * mm});
            skLineSegment(sketch, "E335", {"start": v(186.67, -233.03) * mm, "end": v(195.27, -230.51) * mm});
            skLineSegment(sketch, "E336", {"start": v(193.6, -219.69) * mm, "end": v(225.7, -210.35) * mm, "construction": true});
            skLineSegment(sketch, "E337", {"start": v(225.7, -210.35) * mm, "end": v(217.3, -181.43) * mm, "construction": true});
            skCircle(sketch, "E338", {"center": v(203.39, -267.72) * mm, "radius": 1.5 * mm});
            skLineSegment(sketch, "E339", {"start": v(203.39, -267.72) * mm, "end": v(201.7, -261.96) * mm});
            skLineSegment(sketch, "E340", {"start": v(203.39, -267.72) * mm, "end": v(197.63, -269.4) * mm});
            skLineSegment(sketch, "E341", {"start": v(198.92, -243) * mm, "end": v(206.76, -240.7) * mm});
            skLineSegment(sketch, "E342", {"start": v(200.32, -247.78) * mm, "end": v(208.16, -245.5) * mm});
            skLineSegment(sketch, "E343.MirrorCS", {"start": v(197.52, -238.2) * mm, "end": v(205.35, -235.9) * mm});
            skCircle(sketch, "E344", {"center": v(202.84, -241.85) * mm, "radius": 1.5 * mm});
            skCircle(sketch, "E345", {"center": v(84.97, -213.04) * mm, "radius": 1.5 * mm});
            skCircle(sketch, "E346", {"center": v(61.27, -251.3) * mm, "radius": 1.5 * mm});
            skLineSegment(sketch, "E347", {"start": v(84.97, -213.04) * mm, "end": v(61.27, -251.3) * mm, "construction": true});
            skLineSegment(sketch, "E348", {"start": v(84.97, -213.04) * mm, "end": v(84.97, -251.3) * mm, "construction": true});
            skLineSegment(sketch, "E349", {"start": v(84.97, -251.3) * mm, "end": v(61.27, -251.3) * mm, "construction": true});
            skLineSegment(sketch, "E350", {"start": v(84.97, -213.04) * mm, "end": v(77.91, -213.04) * mm});
            skLineSegment(sketch, "E351", {"start": v(77.91, -213.04) * mm, "end": v(54.21, -251.3) * mm});
            skLineSegment(sketch, "E352", {"start": v(54.21, -251.3) * mm, "end": v(61.27, -251.3) * mm});
            skLineSegment(sketch, "E353", {"start": v(84.97, -213.04) * mm, "end": v(92.03, -213.04) * mm});
            skLineSegment(sketch, "E354", {"start": v(92.03, -213.04) * mm, "end": v(68.33, -251.3) * mm});
            skPoint(sketch, "E354.endSnap0", {"position": v(73.12, -251.3) * mm});
            skLineSegment(sketch, "E355", {"start": v(52.67, -258.89) * mm, "end": v(61.27, -256.37) * mm});
            skLineSegment(sketch, "E356", {"start": v(61.27, -256.37) * mm, "end": v(71.94, -292.82) * mm});
            skLineSegment(sketch, "E357", {"start": v(71.94, -292.82) * mm, "end": v(63.62, -295.25) * mm});
            skLineSegment(sketch, "E358", {"start": v(63.62, -295.25) * mm, "end": v(70.93, -320.23) * mm});
            skLineSegment(sketch, "E359", {"start": v(70.93, -320.23) * mm, "end": v(81.37, -313.17) * mm});
            skLineSegment(sketch, "E360", {"start": v(81.37, -313.17) * mm, "end": v(82.87, -301.27) * mm});
            skLineSegment(sketch, "E361", {"start": v(82.87, -301.27) * mm, "end": v(68.33, -251.3) * mm});
            skLineSegment(sketch, "E362", {"start": v(52.67, -258.89) * mm, "end": v(51.66, -255.42) * mm});
            skLineSegment(sketch, "E363", {"start": v(54.21, -251.3) * mm, "end": v(51.66, -255.42) * mm});
            skLineSegment(sketch, "E364", {"start": v(52.67, -258.89) * mm, "end": v(62.95, -262.12) * mm});
            skLineSegment(sketch, "E365", {"start": v(63.62, -295.25) * mm, "end": v(69.5, -284.5) * mm});
            skLineSegment(sketch, "E366", {"start": v(77.91, -213.04) * mm, "end": v(81.83, -206.72) * mm});
            skLineSegment(sketch, "E367", {"start": v(81.83, -206.72) * mm, "end": v(92.03, -213.04) * mm});
            skLineSegment(sketch, "E368", {"start": v(81.83, -206.72) * mm, "end": v(83.31, -204.33) * mm});
            skLineSegment(sketch, "E369", {"start": v(83.31, -204.33) * mm, "end": v(93.51, -210.65) * mm});
            skLineSegment(sketch, "E370", {"start": v(93.51, -210.65) * mm, "end": v(92.03, -213.04) * mm});
            skLineSegment(sketch, "E371", {"start": v(52.67, -258.89) * mm, "end": v(54.35, -264.63) * mm});
            skLineSegment(sketch, "E372", {"start": v(54.35, -264.63) * mm, "end": v(62.95, -262.12) * mm});
            skLineSegment(sketch, "E373", {"start": v(61.27, -251.3) * mm, "end": v(93.38, -241.95) * mm, "construction": true});
            skLineSegment(sketch, "E374", {"start": v(93.38, -241.95) * mm, "end": v(84.97, -213.04) * mm, "construction": true});
            skCircle(sketch, "E375", {"center": v(71.07, -299.33) * mm, "radius": 1.5 * mm});
            skLineSegment(sketch, "E376", {"start": v(71.07, -299.33) * mm, "end": v(69.38, -293.57) * mm});
            skLineSegment(sketch, "E377", {"start": v(71.07, -299.33) * mm, "end": v(65.3, -301.01) * mm});
            skLineSegment(sketch, "E378", {"start": v(66.6, -274.6) * mm, "end": v(74.44, -272.3) * mm});
            skLineSegment(sketch, "E379", {"start": v(68, -279.38) * mm, "end": v(75.84, -277.1) * mm});
            skCircle(sketch, "E380", {"center": v(70.52, -273.45) * mm, "radius": 1.5 * mm});
            skLineSegment(sketch, "E381", {"start": v(65.2, -269.79) * mm, "end": v(73.05, -267.5) * mm});
            skLineSegment(sketch, "E382", {"start": v(62.95, -262.12) * mm, "end": v(70.82, -259.83) * mm});
            skLineSegment(sketch, "E383", {"start": v(195.27, -230.51) * mm, "end": v(203.13, -228.23) * mm});
            skLineSegment(sketch, "E384", {"start": v(-66.4, -260.73) * mm, "end": v(-74.72, -263.16) * mm});
            skLineSegment(sketch, "E385", {"start": v(-74.72, -263.16) * mm, "end": v(-67.4, -288.13) * mm});
            skLineSegment(sketch, "E386", {"start": v(-67.4, -288.13) * mm, "end": v(-56.97, -281.08) * mm});
            skLineSegment(sketch, "E387", {"start": v(-56.97, -281.08) * mm, "end": v(-55.47, -269.17) * mm});
            skLineSegment(sketch, "E388", {"start": v(-74.72, -263.16) * mm, "end": v(-68.84, -252.4) * mm});
            skCircle(sketch, "E389", {"center": v(-67.27, -267.24) * mm, "radius": 1.5 * mm});
            skLineSegment(sketch, "E390", {"start": v(-67.27, -267.24) * mm, "end": v(-68.96, -261.48) * mm});
            skLineSegment(sketch, "E391", {"start": v(-67.27, -267.24) * mm, "end": v(-73.03, -268.92) * mm});
            skLineSegment(sketch, "E392", {"start": v(-71.73, -242.5) * mm, "end": v(-63.9, -240.21) * mm});
            skLineSegment(sketch, "E393", {"start": v(-70.33, -247.3) * mm, "end": v(-62.5, -245.01) * mm});
            skCircle(sketch, "E394", {"center": v(-67.82, -241.36) * mm, "radius": 1.5 * mm});
            skLineSegment(sketch, "E395", {"start": v(-73.14, -237.7) * mm, "end": v(-65.3, -235.41) * mm});
            skLineSegment(sketch, "E396", {"start": v(-151.99, -246.92) * mm, "end": v(-160.3, -249.35) * mm});
            skLineSegment(sketch, "E397", {"start": v(-160.3, -249.35) * mm, "end": v(-153, -274.33) * mm});
            skLineSegment(sketch, "E398", {"start": v(-153, -274.33) * mm, "end": v(-142.56, -267.27) * mm});
            skLineSegment(sketch, "E399", {"start": v(-142.56, -267.27) * mm, "end": v(-141.06, -255.36) * mm});
            skLineSegment(sketch, "E400", {"start": v(-160.3, -249.35) * mm, "end": v(-154.42, -238.6) * mm});
            skCircle(sketch, "E401", {"center": v(-152.86, -253.43) * mm, "radius": 1.5 * mm});
            skLineSegment(sketch, "E402", {"start": v(-152.86, -253.43) * mm, "end": v(-154.54, -247.67) * mm});
            skLineSegment(sketch, "E403", {"start": v(-152.86, -253.43) * mm, "end": v(-158.62, -255.11) * mm});
            skLineSegment(sketch, "E404", {"start": v(-157.32, -228.7) * mm, "end": v(-149.48, -226.4) * mm});
            skLineSegment(sketch, "E405", {"start": v(-155.92, -233.48) * mm, "end": v(-148.09, -231.2) * mm});
            skCircle(sketch, "E406", {"center": v(-153.4, -227.55) * mm, "radius": 1.5 * mm});
            skLineSegment(sketch, "E407", {"start": v(-158.73, -223.88) * mm, "end": v(-150.88, -221.6) * mm});
            skLineSegment(sketch, "E408", {"start": v(-158.73, -223.88) * mm, "end": v(-154.42, -238.6) * mm});
            skLineSegment(sketch, "E409", {"start": v(-150.88, -221.6) * mm, "end": v(-141.06, -255.36) * mm});
            skLineSegment(sketch, "E410", {"start": v(-73.14, -237.7) * mm, "end": v(-68.84, -252.4) * mm});
            skLineSegment(sketch, "E411", {"start": v(-65.3, -235.41) * mm, "end": v(-55.47, -269.17) * mm});
            skLineSegment(sketch, "E412", {"start": v(-68.84, -252.4) * mm, "end": v(-66.4, -260.73) * mm});
            skLineSegment(sketch, "E413", {"start": v(-151.99, -246.92) * mm, "end": v(-154.42, -238.6) * mm});
            skLineSegment(sketch, "E414", {"start": v(-246.05, -212.53) * mm, "end": v(-254.37, -214.96) * mm});
            skLineSegment(sketch, "E415", {"start": v(-254.37, -214.96) * mm, "end": v(-247.06, -239.93) * mm});
            skLineSegment(sketch, "E416", {"start": v(-251.4, -194.3) * mm, "end": v(-243.55, -192) * mm});
            skLineSegment(sketch, "E417", {"start": v(-250, -199.09) * mm, "end": v(-242.16, -196.81) * mm});
            skCircle(sketch, "E418", {"center": v(-247.47, -193.16) * mm, "radius": 1.5 * mm});
            skLineSegment(sketch, "E419", {"start": v(-252.8, -189.49) * mm, "end": v(-244.95, -187.2) * mm});
            skLineSegment(sketch, "E420", {"start": v(-252.8, -189.49) * mm, "end": v(-248.49, -204.2) * mm});
            skLineSegment(sketch, "E421", {"start": v(-244.95, -187.2) * mm, "end": v(-236.55, -216.1) * mm});
            skLineSegment(sketch, "E422", {"start": v(-246.05, -212.53) * mm, "end": v(-248.49, -204.2) * mm});
            skLineSegment(sketch, "E423", {"start": v(-247.06, -239.93) * mm, "end": v(-232.66, -235.72) * mm});
            skLineSegment(sketch, "E424", {"start": v(-232.66, -235.72) * mm, "end": v(-235.52, -225.97) * mm});
            skLineSegment(sketch, "E425", {"start": v(-235.52, -225.97) * mm, "end": v(-236.55, -216.1) * mm});
            skLineSegment(sketch, "E426", {"start": v(-261.27, -275.06) * mm, "end": v(-269.58, -277.49) * mm});
            skLineSegment(sketch, "E427", {"start": v(-269.58, -277.49) * mm, "end": v(-262.28, -302.46) * mm});
            skLineSegment(sketch, "E428", {"start": v(-266.6, -256.83) * mm, "end": v(-258.77, -254.54) * mm});
            skLineSegment(sketch, "E429", {"start": v(-265.2, -261.62) * mm, "end": v(-257.37, -259.34) * mm});
            skCircle(sketch, "E430", {"center": v(-262.69, -255.69) * mm, "radius": 1.5 * mm});
            skLineSegment(sketch, "E431", {"start": v(-268, -252.02) * mm, "end": v(-260.17, -249.74) * mm});
            skLineSegment(sketch, "E432", {"start": v(-268, -252.02) * mm, "end": v(-263.7, -266.73) * mm});
            skLineSegment(sketch, "E433", {"start": v(-260.17, -249.74) * mm, "end": v(-251.76, -278.62) * mm});
            skLineSegment(sketch, "E434", {"start": v(-261.27, -275.06) * mm, "end": v(-263.7, -266.73) * mm});
            skLineSegment(sketch, "E435", {"start": v(-262.28, -302.46) * mm, "end": v(-247.88, -298.25) * mm});
            skLineSegment(sketch, "E436", {"start": v(-247.88, -298.25) * mm, "end": v(-250.73, -288.5) * mm});
            skLineSegment(sketch, "E437", {"start": v(-250.73, -288.5) * mm, "end": v(-251.76, -278.62) * mm});
            skLineSegment(sketch, "E438", {"start": v(-261.27, -275.06) * mm, "end": v(-265.13, -292.7) * mm});
            skLineSegment(sketch, "E439", {"start": v(-246.05, -212.53) * mm, "end": v(-249.91, -230.18) * mm});
            skLineSegment(sketch, "E440", {"start": v(-249.91, -230.18) * mm, "end": v(-235.52, -225.97) * mm});
            skLineSegment(sketch, "E441", {"start": v(-245.11, -228.78) * mm, "end": v(-242.26, -238.53) * mm});
            skLineSegment(sketch, "E442", {"start": v(-240.31, -227.37) * mm, "end": v(-237.46, -237.12) * mm});
            skLineSegment(sketch, "E443", {"start": v(-265.13, -292.7) * mm, "end": v(-250.73, -288.5) * mm});
            skLineSegment(sketch, "E444", {"start": v(-255.53, -289.9) * mm, "end": v(-252.68, -299.65) * mm});
            skLineSegment(sketch, "E445", {"start": v(-257.48, -301.06) * mm, "end": v(-260.33, -291.3) * mm});
            skLineSegment(sketch, "E446.bottom", {"start": v(289.33, -236.79) * mm, "end": v(284.33, -236.79) * mm});
            skLineSegment(sketch, "E446.top", {"start": v(289.33, -257.03) * mm, "end": v(284.33, -257.03) * mm});
            skLineSegment(sketch, "E446.left", {"start": v(289.33, -236.79) * mm, "end": v(289.33, -257.03) * mm});
            skLineSegment(sketch, "E446.right", {"start": v(284.33, -236.79) * mm, "end": v(284.33, -257.03) * mm});
            skPoint(sketch, "E446.middle", {"position": v(286.83, -246.9) * mm});
            skLineSegment(sketch, "E447", {"start": v(76.76, -214.9) * mm, "end": v(80.59, -217.28) * mm});
            skLineSegment(sketch, "E448", {"start": v(80.59, -217.28) * mm, "end": v(78.93, -211.4) * mm});
            skLineSegment(sketch, "E449", {"start": v(77.04, -223) * mm, "end": v(73.21, -220.63) * mm});
            skLineSegment(sketch, "E450", {"start": v(77.04, -223) * mm, "end": v(80.59, -217.28) * mm});
            skLineSegment(sketch, "E451", {"start": v(78.82, -220.14) * mm, "end": v(74.99, -217.77) * mm});
            skLineSegment(sketch, "E452.MirrorCS", {"start": v(77.04, -223) * mm, "end": v(71.04, -224.14) * mm});
            skLineSegment(sketch, "E453", {"start": v(-120.08, -333.56) * mm, "end": v(-128.29, -336.32) * mm, "construction": true});
            skLineSegment(sketch, "E454", {"start": v(-128.29, -336.32) * mm, "end": v(-120, -360.99) * mm, "construction": true});
            skLineSegment(sketch, "E455", {"start": v(-120, -360.99) * mm, "end": v(-109.56, -353.93) * mm, "construction": true});
            skLineSegment(sketch, "E456", {"start": v(-109.56, -353.93) * mm, "end": v(-108.06, -342.03) * mm, "construction": true});
            skLineSegment(sketch, "E457", {"start": v(-128.29, -336.32) * mm, "end": v(-122.84, -325.34) * mm, "construction": true});
            skCircle(sketch, "E458", {"center": v(-120.69, -340.1) * mm, "radius": 1.5 * mm, "construction": true});
            skLineSegment(sketch, "E459", {"start": v(-120.69, -340.1) * mm, "end": v(-122.6, -334.41) * mm, "construction": true});
            skLineSegment(sketch, "E460", {"start": v(-120.69, -340.1) * mm, "end": v(-126.38, -342.01) * mm});
            skLineSegment(sketch, "E461", {"start": v(-126.17, -315.44) * mm, "end": v(-117.1, -312.52) * mm});
            skLineSegment(sketch, "E462", {"start": v(-124.6, -320.14) * mm, "end": v(-115.51, -317.26) * mm});
            skCircle(sketch, "E463", {"center": v(-121.64, -313.98) * mm, "radius": 1.5 * mm});
            skLineSegment(sketch, "E464", {"start": v(-127.73, -310.82) * mm, "end": v(-118.7, -307.78) * mm});
            skLineSegment(sketch, "E465", {"start": v(208.16, -245.5) * mm, "end": v(211.04, -244.66) * mm});
            skLineSegment(sketch, "E466", {"start": v(211.04, -244.66) * mm, "end": v(209.64, -239.86) * mm});
            skLineSegment(sketch, "E467", {"start": v(209.64, -239.86) * mm, "end": v(205.92, -237.82) * mm});
            skLineSegment(sketch, "E468.MirrorCS", {"start": v(211.04, -244.66) * mm, "end": v(212.43, -249.46) * mm});
            skLineSegment(sketch, "E469.MirrorCS", {"start": v(212.43, -249.46) * mm, "end": v(210.4, -253.18) * mm});
            skLineSegment(sketch, "E470", {"start": v(-118.7, -307.78) * mm, "end": v(-111.05, -330.53) * mm});
            skLineSegment(sketch, "E471", {"start": v(-120.08, -333.56) * mm, "end": v(-111.05, -330.53) * mm});
            skLineSegment(sketch, "E472", {"start": v(-111.05, -330.53) * mm, "end": v(-119.96, -374.64) * mm});
            skLineSegment(sketch, "E473", {"start": v(-119.96, -374.64) * mm, "end": v(-128.99, -377.67) * mm});
            skLineSegment(sketch, "E474", {"start": v(-120.08, -333.56) * mm, "end": v(-128.99, -377.67) * mm});
            skLineSegment(sketch, "E475", {"start": v(-127.73, -310.82) * mm, "end": v(-120.08, -333.56) * mm});
            skLineSegment(sketch, "E476", {"start": v(-126.7, -376.9) * mm, "end": v(-125.22, -381.28) * mm});
            skLineSegment(sketch, "E477", {"start": v(-125.22, -381.28) * mm, "end": v(-121, -379.87) * mm});
            skLineSegment(sketch, "E478", {"start": v(-121, -379.87) * mm, "end": v(-122.48, -375.49) * mm});
            skLineSegment(sketch, "E479.bottom", {"start": v(-75.63, -354.1) * mm, "end": v(-25.63, -354.1) * mm});
            skLineSegment(sketch, "E479.top", {"start": v(-75.63, -373.77) * mm, "end": v(-25.63, -373.77) * mm});
            skLineSegment(sketch, "E479.left", {"start": v(-75.63, -354.1) * mm, "end": v(-75.63, -373.77) * mm});
            skLineSegment(sketch, "E479.right", {"start": v(-25.63, -354.1) * mm, "end": v(-25.63, -373.77) * mm});
            skCircle(sketch, "E480", {"center": v(-150.37, -2.62) * mm, "radius": 1.5 * mm});
            skCircle(sketch, "E481", {"center": v(-150.37, -2.62) * mm, "radius": 3 * mm});
            skLineSegment(sketch, "E482", {"start": v(-17.95, -110.24) * mm, "end": v(-7.57, -142.5) * mm});
            skLineSegment(sketch, "E483", {"start": v(-372.74, -286.9) * mm, "end": v(-381.05, -289.34) * mm});
            skLineSegment(sketch, "E484", {"start": v(-381.05, -289.34) * mm, "end": v(-373.75, -314.3) * mm});
            skLineSegment(sketch, "E485", {"start": v(-378.08, -268.68) * mm, "end": v(-370.24, -266.39) * mm});
            skLineSegment(sketch, "E486", {"start": v(-376.68, -273.47) * mm, "end": v(-368.85, -271.19) * mm});
            skCircle(sketch, "E487", {"center": v(-374.16, -267.53) * mm, "radius": 1.5 * mm});
            skLineSegment(sketch, "E488", {"start": v(-379.48, -263.87) * mm, "end": v(-371.64, -261.59) * mm});
            skLineSegment(sketch, "E489", {"start": v(-379.48, -263.87) * mm, "end": v(-375.18, -278.58) * mm});
            skLineSegment(sketch, "E490", {"start": v(-371.64, -261.59) * mm, "end": v(-363.24, -290.47) * mm});
            skLineSegment(sketch, "E491", {"start": v(-372.74, -286.9) * mm, "end": v(-375.18, -278.58) * mm});
            skLineSegment(sketch, "E492", {"start": v(-373.75, -314.3) * mm, "end": v(-359.35, -310.1) * mm});
            skLineSegment(sketch, "E493", {"start": v(-359.35, -310.1) * mm, "end": v(-362.2, -300.35) * mm});
            skLineSegment(sketch, "E494", {"start": v(-362.2, -300.35) * mm, "end": v(-363.24, -290.47) * mm});
            skLineSegment(sketch, "E495", {"start": v(-372.74, -286.9) * mm, "end": v(-376.6, -304.56) * mm});
            skLineSegment(sketch, "E496", {"start": v(-376.6, -304.56) * mm, "end": v(-362.2, -300.35) * mm});
            skLineSegment(sketch, "E497", {"start": v(-367, -301.75) * mm, "end": v(-364.15, -311.5) * mm});
            skLineSegment(sketch, "E498", {"start": v(-368.95, -312.9) * mm, "end": v(-371.8, -303.15) * mm});
            skLineSegment(sketch, "E499", {"start": v(-359.35, -310.1) * mm, "end": v(-331.56, -298.12) * mm});
            skLineSegment(sketch, "E500", {"start": v(-331.56, -298.12) * mm, "end": v(-338.55, -290.15) * mm});
            skLineSegment(sketch, "E501", {"start": v(-338.55, -290.15) * mm, "end": v(-362.2, -300.35) * mm});
            skSolve(sketch);
        }
        {
            var Q0;
            Q0=makeQuery(id+"F0.imprint","IMPRINT",FACE,{"disambiguationData":[TD([[makeQuery(id+"F0.imprint","IMPRINT",EDGE,{"derivedFrom":sQuery(id+"F0.wireOp",EDGE,"E0.bottom")}),1.0]])]});
            var Q1;
            {var subQ3=sQuery(id+"F0.wireOp",EDGE,"E31.MirrorCS");Q1=makeQuery(id+"F0.imprint","IMPRINT",FACE,{"disambiguationData":[TD([[makeQuery(id+"F0.imprint","IMPRINT",EDGE,{"derivedFrom":subQ3}),-1.0]])]});}
            var Q2;
            {var subQ0=sQuery(id+"F0.wireOp",EDGE,"E29.MirrorCS");Q2=makeQuery(id+"F0.imprint","IMPRINT",FACE,{"disambiguationData":[TD([[makeQuery(id+"F0.imprint","IMPRINT",EDGE,{"derivedFrom":subQ0}),1.0]])]});}
            var Q3;
            {var subQ4=sQuery(id+"F0.wireOp",EDGE,"E32");Q3=makeQuery(id+"F0.imprint","IMPRINT",FACE,{"disambiguationData":[TD([[makeQuery(id+"F0.imprint","IMPRINT",EDGE,{"derivedFrom":subQ4}),-1.0]])]});}
            var Q4;
            {var subQ8=sQuery(id+"F0.wireOp",EDGE,"E2.right");Q4=makeQuery(id+"F0.imprint","IMPRINT",FACE,{"disambiguationData":[TD([[makeQuery(id+"F0.imprint","IMPRINT",EDGE,{"derivedFrom":subQ8}),1.0]])]});}
            var Q5;
            {var subQ0=sQuery(id+"F0.wireOp",EDGE,"E3");var subQ1=sQuery(id+"F0.wireOp",EDGE,"E0.top");var subQ2=makeQuery(id+"F0.imprint","INTERSECT",VERTEX,{"derivedFrom":[subQ1,subQ0]});Q5=makeQuery(id+"F0.imprint","IMPRINT",FACE,{"disambiguationData":[TD([[makeQuery(id+"F0.imprint","IMPRINT",EDGE,{"disambiguationData":[TD([[subQ2,1.0]])],"derivedFrom":subQ1}),1.0]])]});}
            var Q6;
            {var subQ4=sQuery(id+"F0.wireOp",EDGE,"E33.MirrorCS");Q6=makeQuery(id+"F0.imprint","IMPRINT",FACE,{"disambiguationData":[TD([[makeQuery(id+"F0.imprint","IMPRINT",EDGE,{"derivedFrom":subQ4}),1.0]])]});}
            var Q7;
            {var subQ8=sQuery(id+"F0.wireOp",EDGE,"E49.bottom");Q7=makeQuery(id+"F0.imprint","IMPRINT",FACE,{"disambiguationData":[TD([[makeQuery(id+"F0.imprint","IMPRINT",EDGE,{"derivedFrom":subQ8}),-1.0]])]});}
            var Q8;
            {var subQ0=sQuery(id+"F0.wireOp",EDGE,"E43.MirrorCS");var subQ3=sQuery(id+"F0.wireOp",EDGE,"E46");var subQ5=makeQuery(id+"F0.imprint","INTERSECT",VERTEX,{"derivedFrom":[subQ0,subQ3]});Q8=makeQuery(id+"F0.imprint","IMPRINT",FACE,{"disambiguationData":[TD([[makeQuery(id+"F0.imprint","IMPRINT",EDGE,{"disambiguationData":[TD([[subQ5,1.0]])],"derivedFrom":subQ3}),-1.0]])]});}
            var Q9;
            {var subQ0=sQuery(id+"F0.wireOp",EDGE,"E42");var subQ3=sQuery(id+"F0.wireOp",EDGE,"E46");var subQ5=makeQuery(id+"F0.imprint","INTERSECT",VERTEX,{"derivedFrom":[subQ0,subQ3]});Q9=makeQuery(id+"F0.imprint","IMPRINT",FACE,{"disambiguationData":[TD([[makeQuery(id+"F0.imprint","IMPRINT",EDGE,{"disambiguationData":[TD([[subQ5,-1.0]])],"derivedFrom":subQ3}),-1.0]])]});}
            var Q10;
            {var subQ4=sQuery(id+"F0.wireOp",EDGE,"E36");Q10=makeQuery(id+"F0.imprint","IMPRINT",FACE,{"disambiguationData":[TD([[makeQuery(id+"F0.imprint","IMPRINT",EDGE,{"derivedFrom":subQ4}),-1.0]])]});}
            var Q11;
            {var subQ0=sQuery(id+"F0.wireOp",EDGE,"E24.MirrorCS");Q11=makeQuery(id+"F0.imprint","IMPRINT",FACE,{"disambiguationData":[TD([[makeQuery(id+"F0.imprint","IMPRINT",EDGE,{"derivedFrom":subQ0}),1.0]])]});}
            var Q12;
            {var subQ1=sQuery(id+"F0.wireOp",EDGE,"E18");Q12=makeQuery(id+"F0.imprint","IMPRINT",FACE,{"disambiguationData":[TD([[makeQuery(id+"F0.imprint","IMPRINT",EDGE,{"derivedFrom":subQ1}),-1.0]])]});}
            var Q13;
            {var subQ0=sQuery(id+"F0.wireOp",EDGE,"E11");var subQ1=sQuery(id+"F0.wireOp",EDGE,"E10.bottom");var subQ2=makeQuery(id+"F0.imprint","INTERSECT",VERTEX,{"derivedFrom":[subQ1,subQ0]});Q13=makeQuery(id+"F0.imprint","IMPRINT",FACE,{"disambiguationData":[TD([[makeQuery(id+"F0.imprint","IMPRINT",EDGE,{"disambiguationData":[TD([[subQ2,1.0]])],"derivedFrom":subQ1}),-1.0]])]});}
            var Q14;
            {var subQ0=sQuery(id+"F0.wireOp",EDGE,"E12");var subQ1=sQuery(id+"F0.wireOp",EDGE,"E10.bottom");var subQ2=makeQuery(id+"F0.imprint","INTERSECT",VERTEX,{"derivedFrom":[subQ1,subQ0]});Q14=makeQuery(id+"F0.imprint","IMPRINT",FACE,{"disambiguationData":[TD([[makeQuery(id+"F0.imprint","IMPRINT",EDGE,{"disambiguationData":[TD([[subQ2,-1.0]])],"derivedFrom":subQ1}),-1.0]])]});}
            var Q15;
            {var subQ7=sQuery(id+"F0.wireOp",EDGE,"E12");var subQ8=sQuery(id+"F0.wireOp",EDGE,"E2.top");var subQ9=makeQuery(id+"F0.imprint","INTERSECT",VERTEX,{"derivedFrom":[subQ8,subQ7]});Q15=makeQuery(id+"F0.imprint","IMPRINT",FACE,{"disambiguationData":[TD([[makeQuery(id+"F0.imprint","IMPRINT",EDGE,{"disambiguationData":[TD([[subQ9,-1.0]])],"derivedFrom":subQ8}),1.0]])]});}
            var Q16;
            {var subQ7=sQuery(id+"F0.wireOp",EDGE,"E2.top");var subQ9=sQuery(id+"F0.wireOp",EDGE,"E11");var subQ10=makeQuery(id+"F0.imprint","INTERSECT",VERTEX,{"derivedFrom":[subQ7,subQ9]});Q16=makeQuery(id+"F0.imprint","IMPRINT",FACE,{"disambiguationData":[TD([[makeQuery(id+"F0.imprint","IMPRINT",EDGE,{"disambiguationData":[TD([[subQ10,1.0]])],"derivedFrom":subQ7}),1.0]])]});}
            var Q17;
            {var subQ10=sQuery(id+"F0.wireOp",EDGE,"E2.left");Q17=makeQuery(id+"F0.imprint","IMPRINT",FACE,{"disambiguationData":[TD([[makeQuery(id+"F0.imprint","IMPRINT",EDGE,{"derivedFrom":subQ10}),-1.0]])]});}
            var Q18;
            {var subQ3=sQuery(id+"F0.wireOp",EDGE,"E34");Q18=makeQuery(id+"F0.imprint","IMPRINT",FACE,{"disambiguationData":[TD([[makeQuery(id+"F0.imprint","IMPRINT",EDGE,{"derivedFrom":subQ3}),1.0]])]});}
            var Q19;
            {var subQ1=sQuery(id+"F0.wireOp",EDGE,"E10.right");Q19=makeQuery(id+"F0.imprint","IMPRINT",FACE,{"disambiguationData":[TD([[makeQuery(id+"F0.imprint","IMPRINT",EDGE,{"derivedFrom":subQ1}),-1.0]])]});}
            var Q20;
            {var subQ0=sQuery(id+"F0.wireOp",EDGE,"E10.right");Q20=makeQuery(id+"F0.imprint","IMPRINT",FACE,{"disambiguationData":[TD([[makeQuery(id+"F0.imprint","IMPRINT",EDGE,{"derivedFrom":subQ0}),1.0]])]});}
            var Q21;
            {var subQ0=sQuery(id+"F0.wireOp",EDGE,"E35");Q21=makeQuery(id+"F0.imprint","IMPRINT",FACE,{"disambiguationData":[TD([[makeQuery(id+"F0.imprint","IMPRINT",EDGE,{"derivedFrom":subQ0}),-1.0]])]});}
            var Q22;
            {var subQ0=sQuery(id+"F0.wireOp",EDGE,"E38");Q22=makeQuery(id+"F0.imprint","IMPRINT",FACE,{"disambiguationData":[TD([[makeQuery(id+"F0.imprint","IMPRINT",EDGE,{"derivedFrom":subQ0}),-1.0]])]});}
            var Q23;
            {var subQ0=sQuery(id+"F0.wireOp",EDGE,"E10.left");Q23=makeQuery(id+"F0.imprint","IMPRINT",FACE,{"disambiguationData":[TD([[makeQuery(id+"F0.imprint","IMPRINT",EDGE,{"derivedFrom":subQ0}),-1.0]])]});}
            var Q24;
            {var subQ4=sQuery(id+"F0.wireOp",EDGE,"E37.MirrorCS");Q24=makeQuery(id+"F0.imprint","IMPRINT",FACE,{"disambiguationData":[TD([[makeQuery(id+"F0.imprint","IMPRINT",EDGE,{"derivedFrom":subQ4}),1.0]])]});}
            var Q25;
            {var subQ0=sQuery(id+"F0.wireOp",EDGE,"E23");Q25=makeQuery(id+"F0.imprint","IMPRINT",FACE,{"disambiguationData":[TD([[makeQuery(id+"F0.imprint","IMPRINT",EDGE,{"derivedFrom":subQ0}),-1.0]])]});}
            var Q26;
            {var subQ1=sQuery(id+"F0.wireOp",EDGE,"E21.MirrorCS");Q26=makeQuery(id+"F0.imprint","IMPRINT",FACE,{"disambiguationData":[TD([[makeQuery(id+"F0.imprint","IMPRINT",EDGE,{"derivedFrom":subQ1}),1.0]])]});}
            var Q27;
            {var subQ3=sQuery(id+"F0.wireOp",EDGE,"E10.bottom");var subQ5=makeQuery(id+"F0.imprint","INTERSECT",VERTEX,{"derivedFrom":[subQ3,sQuery(id+"F0.wireOp",EDGE,"E12")]});Q27=makeQuery(id+"F0.imprint","IMPRINT",FACE,{"disambiguationData":[TD([[makeQuery(id+"F0.imprint","IMPRINT",EDGE,{"disambiguationData":[TD([[subQ5,1.0]])],"derivedFrom":subQ3}),1.0]])]});}
            var Q28;
            {var subQ5=sQuery(id+"F0.wireOp",EDGE,"E10.bottom");var subQ6=makeQuery(id+"F0.imprint","INTERSECT",VERTEX,{"derivedFrom":[subQ5,sQuery(id+"F0.wireOp",EDGE,"E11")]});Q28=makeQuery(id+"F0.imprint","IMPRINT",FACE,{"disambiguationData":[TD([[makeQuery(id+"F0.imprint","IMPRINT",EDGE,{"disambiguationData":[TD([[subQ6,1.0]])],"derivedFrom":subQ5}),1.0]])]});}
            var Q29;
            {var subQ5=sQuery(id+"F0.wireOp",EDGE,"E20.MirrorCS");Q29=makeQuery(id+"F0.imprint","IMPRINT",FACE,{"disambiguationData":[TD([[makeQuery(id+"F0.imprint","IMPRINT",EDGE,{"derivedFrom":subQ5}),-1.0]])]});}
            var Q30;
            {var subQ5=sQuery(id+"F0.wireOp",EDGE,"E10.left");Q30=makeQuery(id+"F0.imprint","IMPRINT",FACE,{"disambiguationData":[TD([[makeQuery(id+"F0.imprint","IMPRINT",EDGE,{"derivedFrom":subQ5}),1.0]])]});}
            var Q31;
            {var subQ3=sQuery(id+"F0.wireOp",EDGE,"E26");Q31=makeQuery(id+"F0.imprint","IMPRINT",FACE,{"disambiguationData":[TD([[makeQuery(id+"F0.imprint","IMPRINT",EDGE,{"derivedFrom":subQ3}),1.0]])]});}
            var Q32;
            Q32=makeQuery(id+"F0.imprint","IMPRINT",FACE,{"disambiguationData":[TD([[makeQuery(id+"F0.imprint","IMPRINT",EDGE,{"derivedFrom":sQuery(id+"F0.wireOp",EDGE,"E55.top")}),1.0]])]});
            var Q33;
            Q33=makeQuery(id+"F0.imprint","IMPRINT",FACE,{"disambiguationData":[TD([[makeQuery(id+"F0.imprint","IMPRINT",EDGE,{"derivedFrom":sQuery(id+"F0.wireOp",EDGE,"E58")}),-1.0]])]});
            var Q34;
            Q34=makeQuery(id+"F0.imprint","IMPRINT",FACE,{"disambiguationData":[TD([[makeQuery(id+"F0.imprint","IMPRINT",EDGE,{"derivedFrom":sQuery(id+"F0.wireOp",EDGE,"E61.bottom")}),-1.0]])]});
            var Q35;
            {var subQ0=sQuery(id+"F0.wireOp",EDGE,"E40.MirrorCS");var subQ1=sQuery(id+"F0.wireOp",EDGE,"E2.top");var subQ2=makeQuery(id+"F0.imprint","INTERSECT",VERTEX,{"derivedFrom":[subQ1,subQ0]});Q35=makeQuery(id+"F0.imprint","IMPRINT",FACE,{"disambiguationData":[TD([[makeQuery(id+"F0.imprint","IMPRINT",EDGE,{"disambiguationData":[TD([[subQ2,-1.0]])],"derivedFrom":subQ1}),1.0]])]});}
            var Q36;
            {var subQ0=sQuery(id+"F0.wireOp",EDGE,"E39");var subQ1=sQuery(id+"F0.wireOp",EDGE,"E2.top");var subQ2=makeQuery(id+"F0.imprint","INTERSECT",VERTEX,{"derivedFrom":[subQ1,subQ0]});Q36=makeQuery(id+"F0.imprint","IMPRINT",FACE,{"disambiguationData":[TD([[makeQuery(id+"F0.imprint","IMPRINT",EDGE,{"disambiguationData":[TD([[subQ2,1.0]])],"derivedFrom":subQ1}),1.0]])]});}
            var Q37;
            {var subQ0=sQuery(id+"F0.wireOp",EDGE,"E86.MirrorCS");Q37=makeQuery(id+"F0.imprint","IMPRINT",FACE,{"disambiguationData":[TD([[makeQuery(id+"F0.imprint","IMPRINT",EDGE,{"derivedFrom":subQ0}),1.0]])]});}
            var Q38;
            {var subQ3=sQuery(id+"F0.wireOp",EDGE,"E83.bottom");Q38=makeQuery(id+"F0.imprint","IMPRINT",FACE,{"disambiguationData":[TD([[makeQuery(id+"F0.imprint","IMPRINT",EDGE,{"derivedFrom":subQ3}),1.0]])]});}
            var Q39;
            Q39=makeQuery(id+"F0.imprint","IMPRINT",FACE,{"disambiguationData":[TD([[makeQuery(id+"F0.imprint","IMPRINT",EDGE,{"derivedFrom":sQuery(id+"F0.wireOp",EDGE,"E84.bottom")}),-1.0]])]});
            var Q40;
            Q40=makeQuery(id+"F0.imprint","IMPRINT",FACE,{"disambiguationData":[TD([[makeQuery(id+"F0.imprint","IMPRINT",EDGE,{"derivedFrom":sQuery(id+"F0.wireOp",EDGE,"E78.bottom")}),-1.0]])]});
            var Q41;
            {var subQ3=sQuery(id+"F0.wireOp",EDGE,"E77.bottom");Q41=makeQuery(id+"F0.imprint","IMPRINT",FACE,{"disambiguationData":[TD([[makeQuery(id+"F0.imprint","IMPRINT",EDGE,{"derivedFrom":subQ3}),1.0]])]});}
            var Q42;
            {var subQ0=sQuery(id+"F0.wireOp",EDGE,"E80.MirrorCS");Q42=makeQuery(id+"F0.imprint","IMPRINT",FACE,{"disambiguationData":[TD([[makeQuery(id+"F0.imprint","IMPRINT",EDGE,{"derivedFrom":subQ0}),-1.0]])]});}
            var Q43;
            Q43=makeQuery(id+"F0.imprint","IMPRINT",FACE,{"disambiguationData":[TD([[makeQuery(id+"F0.imprint","IMPRINT",EDGE,{"derivedFrom":sQuery(id+"F0.wireOp",EDGE,"E90")}),-1.0]])]});
            var Q44;
            {var subQ0=sQuery(id+"F0.wireOp",EDGE,"Khfw0hrx-Nett-xmZW-1Md8-0aTE6gzZZ4sy");Q44=makeQuery(id+"F0.imprint","IMPRINT",FACE,{"disambiguationData":[TD([[makeQuery(id+"F0.imprint","IMPRINT",EDGE,{"derivedFrom":subQ0}),-1.0]])]});}
            var Q45;
            {var subQ0=sQuery(id+"F0.wireOp",EDGE,"E110");Q45=makeQuery(id+"F0.imprint","IMPRINT",FACE,{"disambiguationData":[TD([[makeQuery(id+"F0.imprint","IMPRINT",EDGE,{"derivedFrom":subQ0}),-1.0]])]});}
            var Q46;
            Q46=makeQuery(id+"F0.imprint","IMPRINT",FACE,{"disambiguationData":[TD([[makeQuery(id+"F0.imprint","IMPRINT",EDGE,{"derivedFrom":sQuery(id+"F0.wireOp",EDGE,"E111")}),1.0]])]});
            var Q47;
            {var subQ0=sQuery(id+"F0.wireOp",EDGE,"E99");Q47=makeQuery(id+"F0.imprint","IMPRINT",FACE,{"disambiguationData":[TD([[makeQuery(id+"F0.imprint","IMPRINT",EDGE,{"derivedFrom":subQ0}),-1.0]])]});}
            var Q48;
            Q48=makeQuery(id+"F0.imprint","IMPRINT",FACE,{"disambiguationData":[TD([[makeQuery(id+"F0.imprint","IMPRINT",EDGE,{"derivedFrom":sQuery(id+"F0.wireOp",EDGE,"E108")}),-1.0]])]});
            var Q49;
            {var subQ5=sQuery(id+"F0.wireOp",EDGE,"19e5a43b-f4a1-4c00-8415-8db8257ce5900.MirrorCS");Q49=makeQuery(id+"F0.imprint","IMPRINT",FACE,{"disambiguationData":[TD([[makeQuery(id+"F0.imprint","IMPRINT",EDGE,{"derivedFrom":subQ5}),-1.0]])]});}
            var Q50;
            {var subQ5=sQuery(id+"F0.wireOp",EDGE,"1f2b1b67-34b6-4750-a4c0-013a82e771c90.MirrorCS");Q50=makeQuery(id+"F0.imprint","IMPRINT",FACE,{"disambiguationData":[TD([[makeQuery(id+"F0.imprint","IMPRINT",EDGE,{"derivedFrom":subQ5}),1.0]])]});}
            var Q51;
            {var subQ5=sQuery(id+"F0.wireOp",EDGE,"E72.right");Q51=makeQuery(id+"F0.imprint","IMPRINT",FACE,{"disambiguationData":[TD([[makeQuery(id+"F0.imprint","IMPRINT",EDGE,{"derivedFrom":subQ5}),-1.0]])]});}
            var Q52;
            {var subQ5=sQuery(id+"F0.wireOp",EDGE,"E72.left");Q52=makeQuery(id+"F0.imprint","IMPRINT",FACE,{"disambiguationData":[TD([[makeQuery(id+"F0.imprint","IMPRINT",EDGE,{"derivedFrom":subQ5}),1.0]])]});}
            var Q53;
            {var subQ5=sQuery(id+"F0.wireOp",EDGE,"E68.bottom");Q53=makeQuery(id+"F0.imprint","IMPRINT",FACE,{"disambiguationData":[TD([[makeQuery(id+"F0.imprint","IMPRINT",EDGE,{"derivedFrom":subQ5}),1.0]])]});}
            var Q54;
            {var subQ5=sQuery(id+"F0.wireOp",EDGE,"E49.top");Q54=makeQuery(id+"F0.imprint","IMPRINT",FACE,{"disambiguationData":[TD([[makeQuery(id+"F0.imprint","IMPRINT",EDGE,{"derivedFrom":subQ5}),-1.0]])]});}
            var Q55;
            {var subQ1=sQuery(id+"F0.wireOp",EDGE,"E49.top");Q55=makeQuery(id+"F0.imprint","IMPRINT",FACE,{"disambiguationData":[TD([[makeQuery(id+"F0.imprint","IMPRINT",EDGE,{"derivedFrom":subQ1}),1.0]])]});}
            var Q56;
            {var subQ5=sQuery(id+"F0.wireOp",EDGE,"E69.left");Q56=makeQuery(id+"F0.imprint","IMPRINT",FACE,{"disambiguationData":[TD([[makeQuery(id+"F0.imprint","IMPRINT",EDGE,{"derivedFrom":subQ5}),-1.0]])]});}
            var Q57;
            {var subQ5=sQuery(id+"F0.wireOp",EDGE,"E69.right");Q57=makeQuery(id+"F0.imprint","IMPRINT",FACE,{"disambiguationData":[TD([[makeQuery(id+"F0.imprint","IMPRINT",EDGE,{"derivedFrom":subQ5}),1.0]])]});}
            var Q58;
            {var subQ5=sQuery(id+"F0.wireOp",EDGE,"E68.top");Q58=makeQuery(id+"F0.imprint","IMPRINT",FACE,{"disambiguationData":[TD([[makeQuery(id+"F0.imprint","IMPRINT",EDGE,{"derivedFrom":subQ5}),-1.0]])]});}
            var Q59;
            {var subQ0=sQuery(id+"F0.wireOp",EDGE,"E14");var subQ1=sQuery(id+"F0.wireOp",EDGE,"E2.top");var subQ2=makeQuery(id+"F0.imprint","INTERSECT",VERTEX,{"derivedFrom":[subQ1,subQ0]});Q59=makeQuery(id+"F0.imprint","IMPRINT",FACE,{"disambiguationData":[TD([[makeQuery(id+"F0.imprint","IMPRINT",EDGE,{"disambiguationData":[TD([[subQ2,1.0]])],"derivedFrom":subQ1}),1.0]])]});}
            var Q60;
            {var subQ0=sQuery(id+"F0.wireOp",EDGE,"E14");var subQ1=sQuery(id+"F0.wireOp",EDGE,"E2.top");var subQ2=makeQuery(id+"F0.imprint","INTERSECT",VERTEX,{"derivedFrom":[subQ1,subQ0]});Q60=makeQuery(id+"F0.imprint","IMPRINT",FACE,{"disambiguationData":[TD([[makeQuery(id+"F0.imprint","IMPRINT",EDGE,{"disambiguationData":[TD([[subQ2,-1.0]])],"derivedFrom":subQ1}),1.0]])]});}
            var Q61;
            Q61=makeQuery(id+"F0.imprint","IMPRINT",FACE,{"disambiguationData":[TD([[makeQuery(id+"F0.imprint","IMPRINT",EDGE,{"derivedFrom":sQuery(id+"F0.wireOp",EDGE,"E129.bottom")}),1.0]])]});
            var Q62;
            {var subQ3=sQuery(id+"F0.wireOp",EDGE,"E160.MirrorCS");Q62=makeQuery(id+"F0.imprint","IMPRINT",FACE,{"disambiguationData":[TD([[makeQuery(id+"F0.imprint","IMPRINT",EDGE,{"derivedFrom":subQ3}),-1.0]])]});}
            var Q63;
            {var subQ0=sQuery(id+"F0.wireOp",EDGE,"E158.MirrorCS");Q63=makeQuery(id+"F0.imprint","IMPRINT",FACE,{"disambiguationData":[TD([[makeQuery(id+"F0.imprint","IMPRINT",EDGE,{"derivedFrom":subQ0}),1.0]])]});}
            var Q64;
            Q64=makeQuery(id+"F0.imprint","IMPRINT",FACE,{"disambiguationData":[TD([[makeQuery(id+"F0.imprint","IMPRINT",EDGE,{"derivedFrom":sQuery(id+"F0.wireOp",EDGE,"E185.bottom")}),-1.0]])]});
            var Q65;
            {var subQ1=sQuery(id+"F0.wireOp",EDGE,"E178.bottom");Q65=makeQuery(id+"F0.imprint","IMPRINT",FACE,{"disambiguationData":[TD([[makeQuery(id+"F0.imprint","IMPRINT",EDGE,{"derivedFrom":subQ1}),-1.0]])]});}
            var Q66;
            {var subQ0=sQuery(id+"F0.wireOp",EDGE,"E172.MirrorCS");var subQ3=sQuery(id+"F0.wireOp",EDGE,"E175");var subQ5=makeQuery(id+"F0.imprint","INTERSECT",VERTEX,{"derivedFrom":[subQ0,subQ3]});Q66=makeQuery(id+"F0.imprint","IMPRINT",FACE,{"disambiguationData":[TD([[makeQuery(id+"F0.imprint","IMPRINT",EDGE,{"disambiguationData":[TD([[subQ5,1.0]])],"derivedFrom":subQ3}),-1.0]])]});}
            var Q67;
            {var subQ0=sQuery(id+"F0.wireOp",EDGE,"E171");var subQ3=sQuery(id+"F0.wireOp",EDGE,"E175");var subQ5=makeQuery(id+"F0.imprint","INTERSECT",VERTEX,{"derivedFrom":[subQ0,subQ3]});Q67=makeQuery(id+"F0.imprint","IMPRINT",FACE,{"disambiguationData":[TD([[makeQuery(id+"F0.imprint","IMPRINT",EDGE,{"disambiguationData":[TD([[subQ5,-1.0]])],"derivedFrom":subQ3}),-1.0]])]});}
            var Q68;
            Q68=makeQuery(id+"F0.imprint","IMPRINT",FACE,{"disambiguationData":[TD([[makeQuery(id+"F0.imprint","IMPRINT",EDGE,{"derivedFrom":sQuery(id+"F0.wireOp",EDGE,"E136.MirrorC")}),1.0]])]});
            var Q69;
            {var subQ4=sQuery(id+"F0.wireOp",EDGE,"E162.MirrorCS");Q69=makeQuery(id+"F0.imprint","IMPRINT",FACE,{"disambiguationData":[TD([[makeQuery(id+"F0.imprint","IMPRINT",EDGE,{"derivedFrom":subQ4}),1.0]])]});}
            var Q70;
            {var subQ5=sQuery(id+"F0.wireOp",EDGE,"E149.MirrorCS");Q70=makeQuery(id+"F0.imprint","IMPRINT",FACE,{"disambiguationData":[TD([[makeQuery(id+"F0.imprint","IMPRINT",EDGE,{"derivedFrom":subQ5}),-1.0]])]});}
            var Q71;
            {var subQ3=sQuery(id+"F0.wireOp",EDGE,"E155");Q71=makeQuery(id+"F0.imprint","IMPRINT",FACE,{"disambiguationData":[TD([[makeQuery(id+"F0.imprint","IMPRINT",EDGE,{"derivedFrom":subQ3}),1.0]])]});}
            var Q72;
            {var subQ4=sQuery(id+"F0.wireOp",EDGE,"E161");Q72=makeQuery(id+"F0.imprint","IMPRINT",FACE,{"disambiguationData":[TD([[makeQuery(id+"F0.imprint","IMPRINT",EDGE,{"derivedFrom":subQ4}),-1.0]])]});}
            var Q73;
            Q73=makeQuery(id+"F0.imprint","IMPRINT",FACE,{"disambiguationData":[TD([[makeQuery(id+"F0.imprint","IMPRINT",EDGE,{"derivedFrom":sQuery(id+"F0.wireOp",EDGE,"E176")}),-1.0]])]});
            var Q74;
            {var subQ0=sQuery(id+"F0.wireOp",EDGE,"E150.MirrorCS");Q74=makeQuery(id+"F0.imprint","IMPRINT",FACE,{"disambiguationData":[TD([[makeQuery(id+"F0.imprint","IMPRINT",EDGE,{"derivedFrom":subQ0}),1.0]])]});}
            var Q75;
            {var subQ5=sQuery(id+"F0.wireOp",EDGE,"E166.MirrorCS");Q75=makeQuery(id+"F0.imprint","IMPRINT",FACE,{"disambiguationData":[TD([[makeQuery(id+"F0.imprint","IMPRINT",EDGE,{"derivedFrom":subQ5}),1.0]])]});}
            var Q76;
            {var subQ0=sQuery(id+"F0.wireOp",EDGE,"E165");Q76=makeQuery(id+"F0.imprint","IMPRINT",FACE,{"disambiguationData":[TD([[makeQuery(id+"F0.imprint","IMPRINT",EDGE,{"derivedFrom":subQ0}),-1.0]])]});}
            var Q77;
            {var subQ1=sQuery(id+"F0.wireOp",EDGE,"E147");Q77=makeQuery(id+"F0.imprint","IMPRINT",FACE,{"disambiguationData":[TD([[makeQuery(id+"F0.imprint","IMPRINT",EDGE,{"derivedFrom":subQ1}),-1.0]])]});}
            var Q78;
            {var subQ0=sQuery(id+"F0.wireOp",EDGE,"E139.right");Q78=makeQuery(id+"F0.imprint","IMPRINT",FACE,{"disambiguationData":[TD([[makeQuery(id+"F0.imprint","IMPRINT",EDGE,{"derivedFrom":subQ0}),1.0]])]});}
            var Q79;
            {var subQ4=sQuery(id+"F0.wireOp",EDGE,"E139.right");Q79=makeQuery(id+"F0.imprint","IMPRINT",FACE,{"disambiguationData":[TD([[makeQuery(id+"F0.imprint","IMPRINT",EDGE,{"derivedFrom":subQ4}),-1.0]])]});}
            var Q80;
            {var subQ0=sQuery(id+"F0.wireOp",EDGE,"E164");Q80=makeQuery(id+"F0.imprint","IMPRINT",FACE,{"disambiguationData":[TD([[makeQuery(id+"F0.imprint","IMPRINT",EDGE,{"derivedFrom":subQ0}),-1.0]])]});}
            var Q81;
            {var subQ0=sQuery(id+"F0.wireOp",EDGE,"E188.right");Q81=makeQuery(id+"F0.imprint","IMPRINT",FACE,{"disambiguationData":[TD([[makeQuery(id+"F0.imprint","IMPRINT",EDGE,{"derivedFrom":subQ0}),-1.0]])]});}
            var Q82;
            {var subQ3=sQuery(id+"F0.wireOp",EDGE,"E163");Q82=makeQuery(id+"F0.imprint","IMPRINT",FACE,{"disambiguationData":[TD([[makeQuery(id+"F0.imprint","IMPRINT",EDGE,{"derivedFrom":subQ3}),1.0]])]});}
            var Q83;
            {var subQ4=sQuery(id+"F0.wireOp",EDGE,"E139.left");Q83=makeQuery(id+"F0.imprint","IMPRINT",FACE,{"disambiguationData":[TD([[makeQuery(id+"F0.imprint","IMPRINT",EDGE,{"derivedFrom":subQ4}),1.0]])]});}
            var Q84;
            {var subQ0=sQuery(id+"F0.wireOp",EDGE,"E139.left");Q84=makeQuery(id+"F0.imprint","IMPRINT",FACE,{"disambiguationData":[TD([[makeQuery(id+"F0.imprint","IMPRINT",EDGE,{"derivedFrom":subQ0}),-1.0]])]});}
            var Q85;
            {var subQ0=sQuery(id+"F0.wireOp",EDGE,"E167");Q85=makeQuery(id+"F0.imprint","IMPRINT",FACE,{"disambiguationData":[TD([[makeQuery(id+"F0.imprint","IMPRINT",EDGE,{"derivedFrom":subQ0}),-1.0]])]});}
            var Q86;
            {var subQ0=sQuery(id+"F0.wireOp",EDGE,"E188.left");Q86=makeQuery(id+"F0.imprint","IMPRINT",FACE,{"disambiguationData":[TD([[makeQuery(id+"F0.imprint","IMPRINT",EDGE,{"derivedFrom":subQ0}),1.0]])]});}
            var Q87;
            {var subQ12=sQuery(id+"F0.wireOp",EDGE,"E187.left");Q87=makeQuery(id+"F0.imprint","IMPRINT",FACE,{"disambiguationData":[TD([[makeQuery(id+"F0.imprint","IMPRINT",EDGE,{"derivedFrom":subQ12}),1.0]])]});}
            var Q88;
            {var subQ5=sQuery(id+"F0.wireOp",EDGE,"E187.right");Q88=makeQuery(id+"F0.imprint","IMPRINT",FACE,{"disambiguationData":[TD([[makeQuery(id+"F0.imprint","IMPRINT",EDGE,{"derivedFrom":subQ5}),-1.0]])]});}
            var Q89;
            {var subQ0=sQuery(id+"F0.wireOp",EDGE,"E168");var subQ10=sQuery(id+"F0.wireOp",EDGE,"E131.top");var subQ11=makeQuery(id+"F0.imprint","INTERSECT",VERTEX,{"derivedFrom":[subQ10,subQ0]});Q89=makeQuery(id+"F0.imprint","IMPRINT",FACE,{"disambiguationData":[TD([[makeQuery(id+"F0.imprint","IMPRINT",EDGE,{"disambiguationData":[TD([[subQ11,1.0]])],"derivedFrom":subQ10}),1.0]])]});}
            var Q90;
            {var subQ0=sQuery(id+"F0.wireOp",EDGE,"E169.MirrorCS");var subQ1=sQuery(id+"F0.wireOp",EDGE,"E131.top");var subQ2=makeQuery(id+"F0.imprint","INTERSECT",VERTEX,{"derivedFrom":[subQ1,subQ0]});Q90=makeQuery(id+"F0.imprint","IMPRINT",FACE,{"disambiguationData":[TD([[makeQuery(id+"F0.imprint","IMPRINT",EDGE,{"disambiguationData":[TD([[subQ2,-1.0]])],"derivedFrom":subQ1}),1.0]])]});}
            var Q91;
            {var subQ0=sQuery(id+"F0.wireOp",EDGE,"E140");var subQ1=sQuery(id+"F0.wireOp",EDGE,"E131.top");var subQ2=makeQuery(id+"F0.imprint","INTERSECT",VERTEX,{"derivedFrom":[subQ1,subQ0]});Q91=makeQuery(id+"F0.imprint","IMPRINT",FACE,{"disambiguationData":[TD([[makeQuery(id+"F0.imprint","IMPRINT",EDGE,{"disambiguationData":[TD([[subQ2,1.0]])],"derivedFrom":subQ1}),1.0]])]});}
            var Q92;
            {var subQ0=sQuery(id+"F0.wireOp",EDGE,"E141");var subQ1=sQuery(id+"F0.wireOp",EDGE,"E131.top");var subQ2=makeQuery(id+"F0.imprint","INTERSECT",VERTEX,{"derivedFrom":[subQ1,subQ0]});Q92=makeQuery(id+"F0.imprint","IMPRINT",FACE,{"disambiguationData":[TD([[makeQuery(id+"F0.imprint","IMPRINT",EDGE,{"disambiguationData":[TD([[subQ2,-1.0]])],"derivedFrom":subQ1}),1.0]])]});}
            var Q93;
            {var subQ5=sQuery(id+"F0.wireOp",EDGE,"E186.bottom");Q93=makeQuery(id+"F0.imprint","IMPRINT",FACE,{"disambiguationData":[TD([[makeQuery(id+"F0.imprint","IMPRINT",EDGE,{"derivedFrom":subQ5}),1.0]])]});}
            var Q94;
            {var subQ5=sQuery(id+"F0.wireOp",EDGE,"E186.top");Q94=makeQuery(id+"F0.imprint","IMPRINT",FACE,{"disambiguationData":[TD([[makeQuery(id+"F0.imprint","IMPRINT",EDGE,{"derivedFrom":subQ5}),-1.0]])]});}
            var Q95;
            {var subQ0=sQuery(id+"F0.wireOp",EDGE,"E153.MirrorCS");Q95=makeQuery(id+"F0.imprint","IMPRINT",FACE,{"disambiguationData":[TD([[makeQuery(id+"F0.imprint","IMPRINT",EDGE,{"derivedFrom":subQ0}),1.0]])]});}
            var Q96;
            {var subQ0=sQuery(id+"F0.wireOp",EDGE,"E152");Q96=makeQuery(id+"F0.imprint","IMPRINT",FACE,{"disambiguationData":[TD([[makeQuery(id+"F0.imprint","IMPRINT",EDGE,{"derivedFrom":subQ0}),-1.0]])]});}
            var Q97;
            {var subQ5=sQuery(id+"F0.wireOp",EDGE,"E187.left");Q97=makeQuery(id+"F0.imprint","IMPRINT",FACE,{"disambiguationData":[TD([[makeQuery(id+"F0.imprint","IMPRINT",EDGE,{"derivedFrom":subQ5}),-1.0]])]});}
            var Q98;
            {var subQ5=sQuery(id+"F0.wireOp",EDGE,"E187.right");Q98=makeQuery(id+"F0.imprint","IMPRINT",FACE,{"disambiguationData":[TD([[makeQuery(id+"F0.imprint","IMPRINT",EDGE,{"derivedFrom":subQ5}),1.0]])]});}
            var Q99;
            {var subQ4=sQuery(id+"F0.wireOp",EDGE,"E203");Q99=makeQuery(id+"F0.imprint","IMPRINT",FACE,{"disambiguationData":[TD([[makeQuery(id+"F0.imprint","IMPRINT",EDGE,{"derivedFrom":subQ4}),-1.0]])]});}
            var Q100;
            {var subQ4=sQuery(id+"F0.wireOp",EDGE,"E208.bottom");Q100=makeQuery(id+"F0.imprint","IMPRINT",FACE,{"disambiguationData":[TD([[makeQuery(id+"F0.imprint","IMPRINT",EDGE,{"derivedFrom":subQ4}),1.0]])]});}
            var Q101;
            {var subQ0=sQuery(id+"F0.wireOp",EDGE,"E208.top");var subQ1=sQuery(id+"F0.wireOp",EDGE,"E206");var subQ2=makeQuery(id+"F0.imprint","INTERSECT",VERTEX,{"derivedFrom":[subQ1,subQ0]});Q101=makeQuery(id+"F0.imprint","IMPRINT",FACE,{"disambiguationData":[TD([[makeQuery(id+"F0.imprint","IMPRINT",EDGE,{"disambiguationData":[TD([[subQ2,-1.0]])],"derivedFrom":subQ1}),1.0]])]});}
            var Q102;
            Q102=makeQuery(id+"F0.imprint","IMPRINT",FACE,{"disambiguationData":[TD([[makeQuery(id+"F0.imprint","IMPRINT",EDGE,{"derivedFrom":sQuery(id+"F0.wireOp",EDGE,"E209.bottom")}),-1.0]])]});
            var Q103;
            Q103=makeQuery(id+"F0.imprint","IMPRINT",FACE,{"disambiguationData":[TD([[makeQuery(id+"F0.imprint","IMPRINT",EDGE,{"derivedFrom":sQuery(id+"F0.wireOp",EDGE,"E210.bottom")}),1.0]])]});
            var Q104;
            Q104=makeQuery(id+"F0.imprint","IMPRINT",FACE,{"disambiguationData":[TD([[makeQuery(id+"F0.imprint","IMPRINT",EDGE,{"derivedFrom":sQuery(id+"F0.wireOp",EDGE,"E218")}),-1.0]])]});
            var Q105;
            Q105=makeQuery(id+"F0.imprint","IMPRINT",FACE,{"disambiguationData":[TD([[makeQuery(id+"F0.imprint","IMPRINT",EDGE,{"derivedFrom":sQuery(id+"F0.wireOp",EDGE,"E234.bottom")}),-1.0]])]});
            var Q106;
            {var subQ4=sQuery(id+"F0.wireOp",EDGE,"95dxYYQW-zxzt-RspT-ydUF-MPakYYPAGUQe");Q106=makeQuery(id+"F0.imprint","IMPRINT",FACE,{"disambiguationData":[TD([[makeQuery(id+"F0.imprint","IMPRINT",EDGE,{"derivedFrom":subQ4}),1.0]])]});}
            var Q107;
            {var subQ3=sQuery(id+"F0.wireOp",EDGE,"E239");Q107=makeQuery(id+"F0.imprint","IMPRINT",FACE,{"disambiguationData":[TD([[makeQuery(id+"F0.imprint","IMPRINT",EDGE,{"derivedFrom":subQ3}),-1.0]])]});}
            var Q108;
            Q108=makeQuery(id+"F0.imprint","IMPRINT",FACE,{"disambiguationData":[TD([[makeQuery(id+"F0.imprint","IMPRINT",EDGE,{"derivedFrom":sQuery(id+"F0.wireOp",EDGE,"E241")}),-1.0]])]});
            var Q109;
            Q109=makeQuery(id+"F0.imprint","IMPRINT",FACE,{"disambiguationData":[TD([[makeQuery(id+"F0.imprint","IMPRINT",EDGE,{"derivedFrom":sQuery(id+"F0.wireOp",EDGE,"E240")}),-1.0]])]});
            var Q110;
            Q110=makeQuery(id+"F0.imprint","IMPRINT",FACE,{"disambiguationData":[TD([[makeQuery(id+"F0.imprint","IMPRINT",EDGE,{"derivedFrom":sQuery(id+"F0.wireOp",EDGE,"E248.bottom")}),-1.0]])]});
            var Q111;
            Q111=makeQuery(id+"F0.imprint","IMPRINT",FACE,{"disambiguationData":[TD([[makeQuery(id+"F0.imprint","IMPRINT",EDGE,{"derivedFrom":sQuery(id+"F0.wireOp",EDGE,"hov1V6x9-UtnZ-4hUH-PMWs-SKLAUF5STT8e.bottom")}),-1.0]])]});
            var Q112;
            {var subQ1=sQuery(id+"F0.wireOp",EDGE,"E225");Q112=makeQuery(id+"F0.imprint","IMPRINT",FACE,{"disambiguationData":[TD([[makeQuery(id+"F0.imprint","IMPRINT",EDGE,{"derivedFrom":subQ1}),1.0]])]});}
            var Q113;
            {var subQ1=sQuery(id+"F0.wireOp",EDGE,"E252.bottom");Q113=makeQuery(id+"F0.imprint","IMPRINT",FACE,{"disambiguationData":[TD([[makeQuery(id+"F0.imprint","IMPRINT",EDGE,{"derivedFrom":subQ1}),-1.0]])]});}
            var Q114;
            Q114=makeQuery(id+"F0.imprint","IMPRINT",FACE,{"disambiguationData":[TD([[makeQuery(id+"F0.imprint","IMPRINT",EDGE,{"derivedFrom":sQuery(id+"F0.wireOp",EDGE,"IsovM9We-VkvH-QV3N-ZQYP-mXsuS8m1GRjf.bottom")}),-1.0]])]});
            var Q115;
            Q115=makeQuery(id+"F0.imprint","IMPRINT",FACE,{"disambiguationData":[TD([[makeQuery(id+"F0.imprint","IMPRINT",EDGE,{"derivedFrom":sQuery(id+"F0.wireOp",EDGE,"OTGBigC1-bcfi-ZySC-RHFn-dXcfwSEauxWA")}),-1.0]])]});
            var Q116;
            {var subQ0=sQuery(id+"F0.wireOp",EDGE,"E258");var subQ3=sQuery(id+"F0.wireOp",EDGE,"E257");var subQ4=makeQuery(id+"F0.imprint","INTERSECT",VERTEX,{"derivedFrom":[subQ3,subQ0]});Q116=makeQuery(id+"F0.imprint","IMPRINT",FACE,{"disambiguationData":[TD([[makeQuery(id+"F0.imprint","IMPRINT",EDGE,{"disambiguationData":[TD([[subQ4,-1.0]])],"derivedFrom":subQ3}),-1.0]])]});}
            var Q117;
            Q117=makeQuery(id+"F0.imprint","IMPRINT",FACE,{"disambiguationData":[TD([[makeQuery(id+"F0.imprint","IMPRINT",EDGE,{"derivedFrom":sQuery(id+"F0.wireOp",EDGE,"3C2WIfIl-k7oo-ORYC-q91I-utM6jY0S7P4w")}),1.0]])]});
            var Q118;
            {var subQ0=sQuery(id+"F0.wireOp",EDGE,"E274");Q118=makeQuery(id+"F0.imprint","IMPRINT",FACE,{"disambiguationData":[TD([[makeQuery(id+"F0.imprint","IMPRINT",EDGE,{"derivedFrom":subQ0}),1.0]])]});}
            var Q119;
            {var subQ0=sQuery(id+"F0.wireOp",EDGE,"E291");var subQ3=sQuery(id+"F0.wireOp",EDGE,"E290");var subQ4=makeQuery(id+"F0.imprint","INTERSECT",VERTEX,{"derivedFrom":[subQ3,subQ0]});Q119=makeQuery(id+"F0.imprint","IMPRINT",FACE,{"disambiguationData":[TD([[makeQuery(id+"F0.imprint","IMPRINT",EDGE,{"disambiguationData":[TD([[subQ4,-1.0]])],"derivedFrom":subQ3}),-1.0]])]});}
            var Q120;
            {var subQ0=sQuery(id+"F0.wireOp",EDGE,"E294");Q120=makeQuery(id+"F0.imprint","IMPRINT",FACE,{"disambiguationData":[TD([[makeQuery(id+"F0.imprint","IMPRINT",EDGE,{"derivedFrom":subQ0}),-1.0]])]});}
            var Q121;
            {var subQ0=sQuery(id+"F0.wireOp",EDGE,"E303");var subQ1=sQuery(id+"F0.wireOp",EDGE,"E299");var subQ2=makeQuery(id+"F0.imprint","INTERSECT",VERTEX,{"derivedFrom":[subQ1,subQ0]});Q121=makeQuery(id+"F0.imprint","IMPRINT",FACE,{"disambiguationData":[TD([[makeQuery(id+"F0.imprint","IMPRINT",EDGE,{"disambiguationData":[TD([[subQ2,-1.0]])],"derivedFrom":subQ1}),1.0]])]});}
            var Q122;
            {var subQ0=sQuery(id+"F0.wireOp",EDGE,"d5502434-5674-4539-93ae-29f8488eadf2");Q122=makeQuery(id+"F0.imprint","IMPRINT",FACE,{"disambiguationData":[TD([[makeQuery(id+"F0.imprint","IMPRINT",EDGE,{"derivedFrom":subQ0}),1.0]])]});}
            var Q123;
            {var subQ0=sQuery(id+"F0.wireOp",EDGE,"5fe69d83-e354-47ea-aa82-d88ca2f8aa38");var subQ1=sQuery(id+"F0.wireOp",EDGE,"f95eb643-fcac-4193-b3cc-2e51d070cb75");var subQ2=makeQuery(id+"F0.imprint","INTERSECT",VERTEX,{"derivedFrom":[subQ1,subQ0]});Q123=makeQuery(id+"F0.imprint","IMPRINT",FACE,{"disambiguationData":[TD([[makeQuery(id+"F0.imprint","IMPRINT",EDGE,{"disambiguationData":[TD([[subQ2,-1.0]])],"derivedFrom":subQ1}),-1.0]])]});}
            var Q124;
            {var subQ2=sQuery(id+"F0.wireOp",EDGE,"ANHEktnk-wsEN-DgU7-QHv2-maxrdJbpi9cD");Q124=makeQuery(id+"F0.imprint","IMPRINT",FACE,{"disambiguationData":[TD([[makeQuery(id+"F0.imprint","IMPRINT",EDGE,{"derivedFrom":subQ2}),-1.0]])]});}
            var Q125;
            Q125=makeQuery(id+"F0.imprint","IMPRINT",FACE,{"disambiguationData":[TD([[makeQuery(id+"F0.imprint","IMPRINT",EDGE,{"derivedFrom":sQuery(id+"F0.wireOp",EDGE,"4WpL3V0v-MQQN-GzT2-LPTR-6nhKLZ0xWXXD")}),-1.0]])]});
            var Q126;
            {var subQ0=sQuery(id+"F0.wireOp",EDGE,"E103");Q126=makeQuery(id+"F0.imprint","IMPRINT",FACE,{"disambiguationData":[TD([[makeQuery(id+"F0.imprint","IMPRINT",EDGE,{"derivedFrom":subQ0}),1.0]])]});}
            var Q127;
            {var subQ4=sQuery(id+"F0.wireOp",EDGE,"E329");Q127=makeQuery(id+"F0.imprint","IMPRINT",FACE,{"disambiguationData":[TD([[makeQuery(id+"F0.imprint","IMPRINT",EDGE,{"derivedFrom":subQ4}),-1.0]])]});}
            var Q128;
            Q128=makeQuery(id+"F0.imprint","IMPRINT",FACE,{"disambiguationData":[TD([[makeQuery(id+"F0.imprint","IMPRINT",EDGE,{"derivedFrom":sQuery(id+"F0.wireOp",EDGE,"E330")}),1.0]])]});
            var Q129;
            Q129=makeQuery(id+"F0.imprint","IMPRINT",FACE,{"disambiguationData":[TD([[makeQuery(id+"F0.imprint","IMPRINT",EDGE,{"derivedFrom":sQuery(id+"F0.wireOp",EDGE,"E309")}),-1.0]])]});
            var Q130;
            {var subQ0=sQuery(id+"F0.wireOp",EDGE,"E318");Q130=makeQuery(id+"F0.imprint","IMPRINT",FACE,{"disambiguationData":[TD([[makeQuery(id+"F0.imprint","IMPRINT",EDGE,{"derivedFrom":subQ0}),-1.0]])]});}
            var Q131;
            Q131=makeQuery(id+"F0.imprint","IMPRINT",FACE,{"disambiguationData":[TD([[makeQuery(id+"F0.imprint","IMPRINT",EDGE,{"derivedFrom":sQuery(id+"F0.wireOp",EDGE,"E327")}),-1.0]])]});
            var Q132;
            {var subQ8=sQuery(id+"F0.wireOp",EDGE,"E342");Q132=makeQuery(id+"F0.imprint","IMPRINT",FACE,{"disambiguationData":[TD([[makeQuery(id+"F0.imprint","IMPRINT",EDGE,{"derivedFrom":subQ8}),1.0]])]});}
            var Q133;
            {var subQ0=sQuery(id+"F0.wireOp",EDGE,"E355");Q133=makeQuery(id+"F0.imprint","IMPRINT",FACE,{"disambiguationData":[TD([[makeQuery(id+"F0.imprint","IMPRINT",EDGE,{"derivedFrom":subQ0}),-1.0]])]});}
            var Q134;
            Q134=makeQuery(id+"F0.imprint","IMPRINT",FACE,{"disambiguationData":[TD([[makeQuery(id+"F0.imprint","IMPRINT",EDGE,{"derivedFrom":sQuery(id+"F0.wireOp",EDGE,"E364")}),-1.0]])]});
            var Q135;
            Q135=makeQuery(id+"F0.imprint","IMPRINT",FACE,{"disambiguationData":[TD([[makeQuery(id+"F0.imprint","IMPRINT",EDGE,{"derivedFrom":sQuery(id+"F0.wireOp",EDGE,"E346")}),-1.0]])]});
            var Q136;
            Q136=makeQuery(id+"F0.imprint","IMPRINT",FACE,{"disambiguationData":[TD([[makeQuery(id+"F0.imprint","IMPRINT",EDGE,{"derivedFrom":sQuery(id+"F0.wireOp",EDGE,"E367")}),1.0]])]});
            var Q137;
            {var subQ7=sQuery(id+"F0.wireOp",EDGE,"E383");Q137=makeQuery(id+"F0.imprint","IMPRINT",FACE,{"disambiguationData":[TD([[makeQuery(id+"F0.imprint","IMPRINT",EDGE,{"derivedFrom":subQ7}),-1.0]])]});}
            var Q138;
            {var subQ0=sQuery(id+"F0.wireOp",EDGE,"E407");Q138=makeQuery(id+"F0.imprint","IMPRINT",FACE,{"disambiguationData":[TD([[makeQuery(id+"F0.imprint","IMPRINT",EDGE,{"derivedFrom":subQ0}),-1.0]])]});}
            var Q139;
            {var subQ0=sQuery(id+"F0.wireOp",EDGE,"E405");Q139=makeQuery(id+"F0.imprint","IMPRINT",FACE,{"disambiguationData":[TD([[makeQuery(id+"F0.imprint","IMPRINT",EDGE,{"derivedFrom":subQ0}),1.0]])]});}
            var Q140;
            {var subQ14=sQuery(id+"F0.wireOp",EDGE,"E398");Q140=makeQuery(id+"F0.imprint","IMPRINT",FACE,{"disambiguationData":[TD([[makeQuery(id+"F0.imprint","IMPRINT",EDGE,{"derivedFrom":subQ14}),1.0]])]});}
            var Q141;
            {var subQ0=sQuery(id+"F0.wireOp",EDGE,"E402");var subQ3=sQuery(id+"F0.wireOp",EDGE,"E401");var subQ4=makeQuery(id+"F0.imprint","INTERSECT",VERTEX,{"derivedFrom":[subQ3,subQ0]});Q141=makeQuery(id+"F0.imprint","IMPRINT",FACE,{"disambiguationData":[TD([[makeQuery(id+"F0.imprint","IMPRINT",EDGE,{"disambiguationData":[TD([[subQ4,-1.0]])],"derivedFrom":subQ3}),-1.0]])]});}
            var Q142;
            {var subQ13=sQuery(id+"F0.wireOp",EDGE,"E386");Q142=makeQuery(id+"F0.imprint","IMPRINT",FACE,{"disambiguationData":[TD([[makeQuery(id+"F0.imprint","IMPRINT",EDGE,{"derivedFrom":subQ13}),1.0]])]});}
            var Q143;
            {var subQ0=sQuery(id+"F0.wireOp",EDGE,"E390");var subQ3=sQuery(id+"F0.wireOp",EDGE,"E389");var subQ4=makeQuery(id+"F0.imprint","INTERSECT",VERTEX,{"derivedFrom":[subQ3,subQ0]});Q143=makeQuery(id+"F0.imprint","IMPRINT",FACE,{"disambiguationData":[TD([[makeQuery(id+"F0.imprint","IMPRINT",EDGE,{"disambiguationData":[TD([[subQ4,-1.0]])],"derivedFrom":subQ3}),-1.0]])]});}
            var Q144;
            {var subQ0=sQuery(id+"F0.wireOp",EDGE,"E390");var subQ1=sQuery(id+"F0.wireOp",EDGE,"E389");var subQ2=makeQuery(id+"F0.imprint","INTERSECT",VERTEX,{"derivedFrom":[subQ1,subQ0]});Q144=makeQuery(id+"F0.imprint","IMPRINT",FACE,{"disambiguationData":[TD([[makeQuery(id+"F0.imprint","IMPRINT",EDGE,{"disambiguationData":[TD([[subQ2,-1.0]])],"derivedFrom":subQ1}),1.0]])]});}
            var Q145;
            {var subQ0=sQuery(id+"F0.wireOp",EDGE,"E390");var subQ1=sQuery(id+"F0.wireOp",EDGE,"E389");var subQ2=makeQuery(id+"F0.imprint","INTERSECT",VERTEX,{"derivedFrom":[subQ1,subQ0]});Q145=makeQuery(id+"F0.imprint","IMPRINT",FACE,{"disambiguationData":[TD([[makeQuery(id+"F0.imprint","IMPRINT",EDGE,{"disambiguationData":[TD([[subQ2,1.0]])],"derivedFrom":subQ1}),1.0]])]});}
            var Q146;
            {var subQ0=sQuery(id+"F0.wireOp",EDGE,"E402");var subQ1=sQuery(id+"F0.wireOp",EDGE,"E401");var subQ2=makeQuery(id+"F0.imprint","INTERSECT",VERTEX,{"derivedFrom":[subQ1,subQ0]});Q146=makeQuery(id+"F0.imprint","IMPRINT",FACE,{"disambiguationData":[TD([[makeQuery(id+"F0.imprint","IMPRINT",EDGE,{"disambiguationData":[TD([[subQ2,-1.0]])],"derivedFrom":subQ1}),1.0]])]});}
            var Q147;
            {var subQ0=sQuery(id+"F0.wireOp",EDGE,"E402");var subQ1=sQuery(id+"F0.wireOp",EDGE,"E401");var subQ2=makeQuery(id+"F0.imprint","INTERSECT",VERTEX,{"derivedFrom":[subQ1,subQ0]});Q147=makeQuery(id+"F0.imprint","IMPRINT",FACE,{"disambiguationData":[TD([[makeQuery(id+"F0.imprint","IMPRINT",EDGE,{"disambiguationData":[TD([[subQ2,1.0]])],"derivedFrom":subQ1}),1.0]])]});}
            var Q148;
            {var subQ0=sQuery(id+"F0.wireOp",EDGE,"E419");Q148=makeQuery(id+"F0.imprint","IMPRINT",FACE,{"disambiguationData":[TD([[makeQuery(id+"F0.imprint","IMPRINT",EDGE,{"derivedFrom":subQ0}),-1.0]])]});}
            var Q149;
            {var subQ3=sQuery(id+"F0.wireOp",EDGE,"E420");var subQ5=sQuery(id+"F0.wireOp",EDGE,"E416");var subQ10=makeQuery(id+"F0.imprint","INTERSECT",VERTEX,{"derivedFrom":[subQ5,subQ3]});Q149=makeQuery(id+"F0.imprint","IMPRINT",FACE,{"disambiguationData":[TD([[makeQuery(id+"F0.imprint","IMPRINT",EDGE,{"disambiguationData":[TD([[subQ10,-1.0]])],"derivedFrom":subQ5}),-1.0]])]});}
            var Q150;
            {var subQ0=sQuery(id+"F0.wireOp",EDGE,"E422");Q150=makeQuery(id+"F0.imprint","IMPRINT",FACE,{"disambiguationData":[TD([[makeQuery(id+"F0.imprint","IMPRINT",EDGE,{"derivedFrom":subQ0}),-1.0]])]});}
            var Q151;
            {var subQ0=sQuery(id+"F0.wireOp",EDGE,"a78c5445-5684-4007-b0e8-18fa9457db71");var subQ3=sQuery(id+"F0.wireOp",EDGE,"76325574-faa0-434f-a953-613189bb89e6");var subQ4=makeQuery(id+"F0.imprint","INTERSECT",VERTEX,{"derivedFrom":[subQ3,subQ0]});Q151=makeQuery(id+"F0.imprint","IMPRINT",FACE,{"disambiguationData":[TD([[makeQuery(id+"F0.imprint","IMPRINT",EDGE,{"disambiguationData":[TD([[subQ4,-1.0]])],"derivedFrom":subQ3}),-1.0]])]});}
            var Q152;
            {var subQ0=sQuery(id+"F0.wireOp",EDGE,"E434");Q152=makeQuery(id+"F0.imprint","IMPRINT",FACE,{"disambiguationData":[TD([[makeQuery(id+"F0.imprint","IMPRINT",EDGE,{"derivedFrom":subQ0}),-1.0]])]});}
            var Q153;
            {var subQ0=sQuery(id+"F0.wireOp",EDGE,"cdbb3e63-fbb1-47bc-be27-200395dd0a79");var subQ3=sQuery(id+"F0.wireOp",EDGE,"d836a354-d18a-435f-a8ba-ac5ae2cda933");var subQ4=makeQuery(id+"F0.imprint","INTERSECT",VERTEX,{"derivedFrom":[subQ3,subQ0]});Q153=makeQuery(id+"F0.imprint","IMPRINT",FACE,{"disambiguationData":[TD([[makeQuery(id+"F0.imprint","IMPRINT",EDGE,{"disambiguationData":[TD([[subQ4,-1.0]])],"derivedFrom":subQ3}),-1.0]])]});}
            var Q154;
            {var subQ0=sQuery(id+"F0.wireOp",EDGE,"a78c5445-5684-4007-b0e8-18fa9457db71");var subQ1=sQuery(id+"F0.wireOp",EDGE,"76325574-faa0-434f-a953-613189bb89e6");var subQ2=makeQuery(id+"F0.imprint","INTERSECT",VERTEX,{"derivedFrom":[subQ1,subQ0]});Q154=makeQuery(id+"F0.imprint","IMPRINT",FACE,{"disambiguationData":[TD([[makeQuery(id+"F0.imprint","IMPRINT",EDGE,{"disambiguationData":[TD([[subQ2,1.0]])],"derivedFrom":subQ1}),1.0]])]});}
            var Q155;
            {var subQ0=sQuery(id+"F0.wireOp",EDGE,"a78c5445-5684-4007-b0e8-18fa9457db71");var subQ1=sQuery(id+"F0.wireOp",EDGE,"76325574-faa0-434f-a953-613189bb89e6");var subQ2=makeQuery(id+"F0.imprint","INTERSECT",VERTEX,{"derivedFrom":[subQ1,subQ0]});Q155=makeQuery(id+"F0.imprint","IMPRINT",FACE,{"disambiguationData":[TD([[makeQuery(id+"F0.imprint","IMPRINT",EDGE,{"disambiguationData":[TD([[subQ2,-1.0]])],"derivedFrom":subQ1}),1.0]])]});}
            var Q156;
            {var subQ0=sQuery(id+"F0.wireOp",EDGE,"cdbb3e63-fbb1-47bc-be27-200395dd0a79");var subQ1=sQuery(id+"F0.wireOp",EDGE,"d836a354-d18a-435f-a8ba-ac5ae2cda933");var subQ2=makeQuery(id+"F0.imprint","INTERSECT",VERTEX,{"derivedFrom":[subQ1,subQ0]});Q156=makeQuery(id+"F0.imprint","IMPRINT",FACE,{"disambiguationData":[TD([[makeQuery(id+"F0.imprint","IMPRINT",EDGE,{"disambiguationData":[TD([[subQ2,1.0]])],"derivedFrom":subQ1}),1.0]])]});}
            var Q157;
            {var subQ0=sQuery(id+"F0.wireOp",EDGE,"cdbb3e63-fbb1-47bc-be27-200395dd0a79");var subQ1=sQuery(id+"F0.wireOp",EDGE,"d836a354-d18a-435f-a8ba-ac5ae2cda933");var subQ2=makeQuery(id+"F0.imprint","INTERSECT",VERTEX,{"derivedFrom":[subQ1,subQ0]});Q157=makeQuery(id+"F0.imprint","IMPRINT",FACE,{"disambiguationData":[TD([[makeQuery(id+"F0.imprint","IMPRINT",EDGE,{"disambiguationData":[TD([[subQ2,-1.0]])],"derivedFrom":subQ1}),1.0]])]});}
            var Q158;
            {var subQ2=sQuery(id+"F0.wireOp",EDGE,"E381");Q158=makeQuery(id+"F0.imprint","IMPRINT",FACE,{"disambiguationData":[TD([[makeQuery(id+"F0.imprint","IMPRINT",EDGE,{"derivedFrom":subQ2}),1.0]])]});}
            var Q159;
            {var subQ0=sQuery(id+"F0.wireOp",EDGE,"E302");var subQ1=sQuery(id+"F0.wireOp",EDGE,"E299");var subQ2=makeQuery(id+"F0.imprint","INTERSECT",VERTEX,{"derivedFrom":[subQ1,subQ0]});Q159=makeQuery(id+"F0.imprint","IMPRINT",FACE,{"disambiguationData":[TD([[makeQuery(id+"F0.imprint","IMPRINT",EDGE,{"disambiguationData":[TD([[subQ2,-1.0]])],"derivedFrom":subQ1}),1.0]])]});}
            var Q160;
            {var subQ0=sQuery(id+"F0.wireOp",EDGE,"E434");Q160=makeQuery(id+"F0.imprint","IMPRINT",FACE,{"disambiguationData":[TD([[makeQuery(id+"F0.imprint","IMPRINT",EDGE,{"derivedFrom":subQ0}),1.0]])]});}
            var Q161;
            {var subQ0=sQuery(id+"F0.wireOp",EDGE,"E422");Q161=makeQuery(id+"F0.imprint","IMPRINT",FACE,{"disambiguationData":[TD([[makeQuery(id+"F0.imprint","IMPRINT",EDGE,{"derivedFrom":subQ0}),1.0]])]});}
            var Q162;
            {var subQ0=sQuery(id+"F0.wireOp",EDGE,"E441");Q162=makeQuery(id+"F0.imprint","IMPRINT",FACE,{"disambiguationData":[TD([[makeQuery(id+"F0.imprint","IMPRINT",EDGE,{"derivedFrom":subQ0}),1.0]])]});}
            var Q163;
            {var subQ0=sQuery(id+"F0.wireOp",EDGE,"E439");Q163=makeQuery(id+"F0.imprint","IMPRINT",FACE,{"disambiguationData":[TD([[makeQuery(id+"F0.imprint","IMPRINT",EDGE,{"derivedFrom":subQ0}),-1.0]])]});}
            var Q164;
            {var subQ0=sQuery(id+"F0.wireOp",EDGE,"E444");Q164=makeQuery(id+"F0.imprint","IMPRINT",FACE,{"disambiguationData":[TD([[makeQuery(id+"F0.imprint","IMPRINT",EDGE,{"derivedFrom":subQ0}),-1.0]])]});}
            var Q165;
            {var subQ0=sQuery(id+"F0.wireOp",EDGE,"E426");Q165=makeQuery(id+"F0.imprint","IMPRINT",FACE,{"disambiguationData":[TD([[makeQuery(id+"F0.imprint","IMPRINT",EDGE,{"derivedFrom":subQ0}),1.0]])]});}
            var Q166;
            {var subQ0=sQuery(id+"F0.wireOp",EDGE,"E367");Q166=makeQuery(id+"F0.imprint","IMPRINT",FACE,{"disambiguationData":[TD([[makeQuery(id+"F0.imprint","IMPRINT",EDGE,{"derivedFrom":subQ0}),-1.0]])]});}
            var Q167;
            {var subQ2=sQuery(id+"F0.wireOp",EDGE,"E456");Q167=makeQuery(id+"F0.imprint","IMPRINT",FACE,{"disambiguationData":[TD([[makeQuery(id+"F0.imprint","IMPRINT",EDGE,{"derivedFrom":subQ2}),1.0]])]});}
            var Q168;
            {var subQ4=sQuery(id+"F0.wireOp",EDGE,"E456");Q168=makeQuery(id+"F0.imprint","IMPRINT",FACE,{"disambiguationData":[TD([[makeQuery(id+"F0.imprint","IMPRINT",EDGE,{"derivedFrom":subQ4}),-1.0]])]});}
            var Q169;
            {var subQ0=sQuery(id+"F0.wireOp",EDGE,"BnSrfYL9-JGz9-WoVh-ZA29-NejsGV2hQXQg");Q169=makeQuery(id+"F0.imprint","IMPRINT",FACE,{"disambiguationData":[TD([[makeQuery(id+"F0.imprint","IMPRINT",EDGE,{"derivedFrom":subQ0}),1.0]])]});}
            var Q170;
            {var subQ4=sQuery(id+"F0.wireOp",EDGE,"E335");Q170=makeQuery(id+"F0.imprint","IMPRINT",FACE,{"disambiguationData":[TD([[makeQuery(id+"F0.imprint","IMPRINT",EDGE,{"derivedFrom":subQ4}),-1.0]])]});}
            var Q171;
            {var subQ0=sQuery(id+"F0.wireOp",EDGE,"E366");var subQ3=sQuery(id+"F0.wireOp",EDGE,"E448");var subQ5=makeQuery(id+"F0.imprint","INTERSECT",VERTEX,{"derivedFrom":[subQ0,subQ3]});Q171=makeQuery(id+"F0.imprint","IMPRINT",FACE,{"disambiguationData":[TD([[makeQuery(id+"F0.imprint","IMPRINT",EDGE,{"disambiguationData":[TD([[subQ5,1.0]])],"derivedFrom":subQ3}),1.0]])]});}
            var Q172;
            {var subQ5=sQuery(id+"F0.wireOp",EDGE,"E447");Q172=makeQuery(id+"F0.imprint","IMPRINT",FACE,{"disambiguationData":[TD([[makeQuery(id+"F0.imprint","IMPRINT",EDGE,{"derivedFrom":subQ5}),1.0]])]});}
            var Q173;
            {var subQ0=sQuery(id+"F0.wireOp",EDGE,"E447");Q173=makeQuery(id+"F0.imprint","IMPRINT",FACE,{"disambiguationData":[TD([[makeQuery(id+"F0.imprint","IMPRINT",EDGE,{"derivedFrom":subQ0}),-1.0]])]});}
            var Q174;
            {var subQ0=sQuery(id+"F0.wireOp",EDGE,"E449");Q174=makeQuery(id+"F0.imprint","IMPRINT",FACE,{"disambiguationData":[TD([[makeQuery(id+"F0.imprint","IMPRINT",EDGE,{"derivedFrom":subQ0}),-1.0]])]});}
            var Q175;
            {var subQ0=sQuery(id+"F0.wireOp",EDGE,"E449");Q175=makeQuery(id+"F0.imprint","IMPRINT",FACE,{"disambiguationData":[TD([[makeQuery(id+"F0.imprint","IMPRINT",EDGE,{"derivedFrom":subQ0}),1.0]])]});}
            var Q176;
            {var subQ0=sQuery(id+"F0.wireOp",EDGE,"E372");Q176=makeQuery(id+"F0.imprint","IMPRINT",FACE,{"disambiguationData":[TD([[makeQuery(id+"F0.imprint","IMPRINT",EDGE,{"derivedFrom":subQ0}),-1.0]])]});}
            var Q177;
            {var subQ5=sQuery(id+"F0.wireOp",EDGE,"E343.MirrorCS");Q177=makeQuery(id+"F0.imprint","IMPRINT",FACE,{"disambiguationData":[TD([[makeQuery(id+"F0.imprint","IMPRINT",EDGE,{"derivedFrom":subQ5}),-1.0]])]});}
            var Q178;
            {var subQ0=sQuery(id+"F0.wireOp",EDGE,"E341");var subQ5=sQuery(id+"F0.wireOp",EDGE,"E319");var subQ6=makeQuery(id+"F0.imprint","INTERSECT",VERTEX,{"derivedFrom":[subQ5,subQ0]});Q178=makeQuery(id+"F0.imprint","IMPRINT",FACE,{"disambiguationData":[TD([[makeQuery(id+"F0.imprint","IMPRINT",EDGE,{"disambiguationData":[TD([[subQ6,-1.0]])],"derivedFrom":subQ5}),1.0]])]});}
            var Q179;
            {var subQ0=sQuery(id+"F0.wireOp",EDGE,"Fr2m7nvS-aiLL-53Eb-Yacg-OlUH9iOtgxkQ");Q179=makeQuery(id+"F0.imprint","IMPRINT",FACE,{"disambiguationData":[TD([[makeQuery(id+"F0.imprint","IMPRINT",EDGE,{"derivedFrom":subQ0}),1.0]])]});}
            var Q180;
            {var subQ4=sQuery(id+"F0.wireOp",EDGE,"Cxx9pjYG-bE2c-Mbkh-tHiK-V0QWooCELOWI");Q180=makeQuery(id+"F0.imprint","IMPRINT",FACE,{"disambiguationData":[TD([[makeQuery(id+"F0.imprint","IMPRINT",EDGE,{"derivedFrom":subQ4}),-1.0]])]});}
            var Q181;
            {var subQ0=sQuery(id+"F0.wireOp",EDGE,"Fr2m7nvS-aiLL-53Eb-Yacg-OlUH9iOtgxkQ");Q181=makeQuery(id+"F0.imprint","IMPRINT",FACE,{"disambiguationData":[TD([[makeQuery(id+"F0.imprint","IMPRINT",EDGE,{"derivedFrom":subQ0}),-1.0]])]});}
            var Q182;
            {var subQ0=sQuery(id+"F0.wireOp",EDGE,"E465");Q182=makeQuery(id+"F0.imprint","IMPRINT",FACE,{"disambiguationData":[TD([[makeQuery(id+"F0.imprint","IMPRINT",EDGE,{"derivedFrom":subQ0}),-1.0]])]});}
            var Q183;
            {var subQ0=sQuery(id+"F0.wireOp",EDGE,"E465");Q183=makeQuery(id+"F0.imprint","IMPRINT",FACE,{"disambiguationData":[TD([[makeQuery(id+"F0.imprint","IMPRINT",EDGE,{"derivedFrom":subQ0}),1.0]])]});}
            var Q184;
            {var subQ0=sQuery(id+"F0.wireOp",EDGE,"E476");Q184=makeQuery(id+"F0.imprint","IMPRINT",FACE,{"disambiguationData":[TD([[makeQuery(id+"F0.imprint","IMPRINT",EDGE,{"derivedFrom":subQ0}),1.0]])]});}
            var Q185;
            {var subQ4=sQuery(id+"F0.wireOp",EDGE,"E471");Q185=makeQuery(id+"F0.imprint","IMPRINT",FACE,{"disambiguationData":[TD([[makeQuery(id+"F0.imprint","IMPRINT",EDGE,{"derivedFrom":subQ4}),-1.0]])]});}
            var Q186;
            {var subQ0=sQuery(id+"F0.wireOp",EDGE,"E462");Q186=makeQuery(id+"F0.imprint","IMPRINT",FACE,{"disambiguationData":[TD([[makeQuery(id+"F0.imprint","IMPRINT",EDGE,{"derivedFrom":subQ0}),-1.0]])]});}
            var Q187;
            {var subQ0=sQuery(id+"F0.wireOp",EDGE,"E462");Q187=makeQuery(id+"F0.imprint","IMPRINT",FACE,{"disambiguationData":[TD([[makeQuery(id+"F0.imprint","IMPRINT",EDGE,{"derivedFrom":subQ0}),1.0]])]});}
            var Q188;
            {var subQ0=sQuery(id+"F0.wireOp",EDGE,"E464");Q188=makeQuery(id+"F0.imprint","IMPRINT",FACE,{"disambiguationData":[TD([[makeQuery(id+"F0.imprint","IMPRINT",EDGE,{"derivedFrom":subQ0}),-1.0]])]});}
            var Q189;
            {var subQ5=sQuery(id+"F0.wireOp",EDGE,"E49.bottom");Q189=makeQuery(id+"F0.imprint","IMPRINT",FACE,{"disambiguationData":[TD([[makeQuery(id+"F0.imprint","IMPRINT",EDGE,{"derivedFrom":subQ5}),1.0]])]});}
            var Q190;
            Q190=makeQuery(id+"F0.imprint","IMPRINT",FACE,{"disambiguationData":[TD([[makeQuery(id+"F0.imprint","IMPRINT",EDGE,{"derivedFrom":sQuery(id+"F0.wireOp",EDGE,"E480")}),-1.0]])]});
            var Q191;
            {var subQ7=sQuery(id+"F0.wireOp",EDGE,"E131.top");var subQ17=makeQuery(id+"F0.imprint","INTERSECT",VERTEX,{"derivedFrom":[subQ7,sQuery(id+"F0.wireOp",EDGE,"E152")]});Q191=makeQuery(id+"F0.imprint","IMPRINT",FACE,{"disambiguationData":[TD([[makeQuery(id+"F0.imprint","IMPRINT",EDGE,{"disambiguationData":[TD([[subQ17,-1.0]])],"derivedFrom":subQ7}),-1.0]])]});}
            var Q192;
            {var subQ0=sQuery(id+"F0.wireOp",EDGE,"E172.MirrorCS");var subQ5=makeQuery(id+"F0.imprint","INTERSECT",VERTEX,{"derivedFrom":[subQ0,sQuery(id+"F0.wireOp",EDGE,"E175")]});Q192=makeQuery(id+"F0.imprint","IMPRINT",FACE,{"disambiguationData":[TD([[makeQuery(id+"F0.imprint","IMPRINT",EDGE,{"disambiguationData":[TD([[subQ5,-1.0]])],"derivedFrom":subQ0}),-1.0]])]});}
            var Q193;
            {var subQ4=sQuery(id+"F0.wireOp",EDGE,"E491");Q193=makeQuery(id+"F0.imprint","IMPRINT",FACE,{"disambiguationData":[TD([[makeQuery(id+"F0.imprint","IMPRINT",EDGE,{"derivedFrom":subQ4}),-1.0]])]});}
            var Q194;
            {var subQ0=sQuery(id+"F0.wireOp",EDGE,"E497");Q194=makeQuery(id+"F0.imprint","IMPRINT",FACE,{"disambiguationData":[TD([[makeQuery(id+"F0.imprint","IMPRINT",EDGE,{"derivedFrom":subQ0}),-1.0]])]});}
            var Q195;
            {var subQ0=sQuery(id+"F0.wireOp",EDGE,"E493");Q195=makeQuery(id+"F0.imprint","IMPRINT",FACE,{"disambiguationData":[TD([[makeQuery(id+"F0.imprint","IMPRINT",EDGE,{"derivedFrom":subQ0}),1.0]])]});}
            var Q196;
            Q196=makeQuery(id+"F0.imprint","IMPRINT",FACE,{"disambiguationData":[TD([[makeQuery(id+"F0.imprint","IMPRINT",EDGE,{"derivedFrom":sQuery(id+"F0.wireOp",EDGE,"E493")}),-1.0]])]});
            var Q197;
            {var subQ0=sQuery(id+"F0.wireOp",EDGE,"E488");Q197=makeQuery(id+"F0.imprint","IMPRINT",FACE,{"disambiguationData":[TD([[makeQuery(id+"F0.imprint","IMPRINT",EDGE,{"derivedFrom":subQ0}),-1.0]])]});}
            var Q198;
            {var subQ3=sQuery(id+"F0.wireOp",EDGE,"E489");var subQ5=sQuery(id+"F0.wireOp",EDGE,"E485");var subQ10=makeQuery(id+"F0.imprint","INTERSECT",VERTEX,{"derivedFrom":[subQ5,subQ3]});Q198=makeQuery(id+"F0.imprint","IMPRINT",FACE,{"disambiguationData":[TD([[makeQuery(id+"F0.imprint","IMPRINT",EDGE,{"disambiguationData":[TD([[subQ10,-1.0]])],"derivedFrom":subQ5}),-1.0]])]});}
            var Q199;
            {var subQ0=sQuery(id+"F0.wireOp",EDGE,"E483");Q199=makeQuery(id+"F0.imprint","IMPRINT",FACE,{"disambiguationData":[TD([[makeQuery(id+"F0.imprint","IMPRINT",EDGE,{"derivedFrom":subQ0}),1.0]])]});}
            extrude(context, id + "F1", {"entities" : qUnion([Q0, Q1, Q2, Q3, Q4, Q5, Q6, Q7, Q8, Q9, Q10, Q11, Q12, Q13, Q14, Q15, Q16, Q17, Q18, Q19, Q20, Q21, Q22, Q23, Q24, Q25, Q26, Q27, Q28, Q29, Q30, Q31, Q32, Q33, Q34, Q35, Q36, Q37, Q38, Q39, Q40, Q41, Q42, Q43, Q44, Q45, Q46, Q47, Q48, Q49, Q50, Q51, Q52, Q53, Q54, Q55, Q56, Q57, Q58, Q59, Q60, Q61, Q62, Q63, Q64, Q65, Q66, Q67, Q68, Q69, Q70, Q71, Q72, Q73, Q74, Q75, Q76, Q77, Q78, Q79, Q80, Q81, Q82, Q83, Q84, Q85, Q86, Q87, Q88, Q89, Q90, Q91, Q92, Q93, Q94, Q95, Q96, Q97, Q98, Q99, Q100, Q101, Q102, Q103, Q104, Q105, Q106, Q107, Q108, Q109, Q110, Q111, Q112, Q113, Q114, Q115, Q116, Q117, Q118, Q119, Q120, Q121, Q122, Q123, Q124, Q125, Q126, Q127, Q128, Q129, Q130, Q131, Q132, Q133, Q134, Q135, Q136, Q137, Q138, Q139, Q140, Q141, Q142, Q143, Q144, Q145, Q146, Q147, Q148, Q149, Q150, Q151, Q152, Q153, Q154, Q155, Q156, Q157, Q158, Q159, Q160, Q161, Q162, Q163, Q164, Q165, Q166, Q167, Q168, Q169, Q170, Q171, Q172, Q173, Q174, Q175, Q176, Q177, Q178, Q179, Q180, Q181, Q182, Q183, Q184, Q185, Q186, Q187, Q188, Q189, Q190, Q191, Q192, Q193, Q194, Q195, Q196, Q197, Q198, Q199]), "depth" : 5.08 * mm, "offsetDistance" : 25 * mm});
        }
        {
            var Q0;
            Q0=makeQuery(id+"F1.opExtrude","SWEPT_FACE",FACE,{"disambiguationData":[OSD([sQuery(id+"F0.wireOp",EDGE,"E55.right"),sQuery(id+"F0.wireOp",EDGE,"E59.right")])]});
            var sketch = newSketch(context, id + "F2", { "sketchPlane" : qUnion([Q0])});
            skLineSegment(sketch, "E502", {"start": v(27.13, 5.08) * mm, "end": v(16.75, 34.3) * mm});
            skLineSegment(sketch, "E503", {"start": v(16.75, 34.3) * mm, "end": v(5.96, 5.08) * mm});
            skLineSegment(sketch, "E504", {"start": v(13.23, 5.08) * mm, "end": v(16.75, 14.6) * mm});
            skLineSegment(sketch, "E505", {"start": v(16.75, 14.6) * mm, "end": v(20.13, 5.08) * mm});
            skLineSegment(sketch, "E506", {"start": v(23.75, 14.6) * mm, "end": v(9.48, 14.6) * mm});
            skLineSegment(sketch, "E507", {"start": v(24.46, 12.6) * mm, "end": v(8.74, 12.6) * mm});
            skLineSegment(sketch, "E508", {"start": v(26.42, 7.08) * mm, "end": v(6.7, 7.08) * mm});
            skLineSegment(sketch, "E509", {"start": v(5.96, 5.08) * mm, "end": v(5.96, 32.32) * mm, "construction": true});
            skLineSegment(sketch, "E510.MirrorCS", {"start": v(-4.82, 34.3) * mm, "end": v(5.96, 5.08) * mm});
            skLineSegment(sketch, "E511.MirrorCS", {"start": v(-15.2, 5.08) * mm, "end": v(-4.82, 34.3) * mm});
            skLineSegment(sketch, "E512.MirrorCS", {"start": v(-11.82, 14.6) * mm, "end": v(2.45, 14.6) * mm});
            skLineSegment(sketch, "E513.MirrorCS", {"start": v(-12.53, 12.6) * mm, "end": v(3.19, 12.6) * mm});
            skLineSegment(sketch, "E514.MirrorCS", {"start": v(-1.3, 5.08) * mm, "end": v(-4.82, 14.6) * mm});
            skLineSegment(sketch, "E515.MirrorCS", {"start": v(-4.82, 14.6) * mm, "end": v(-8.2, 5.08) * mm});
            skLineSegment(sketch, "E516.MirrorCS", {"start": v(-14.5, 7.08) * mm, "end": v(5.22, 7.08) * mm});
            skLineSegment(sketch, "E517", {"start": v(5.22, 7.08) * mm, "end": v(6.7, 7.08) * mm});
            skLineSegment(sketch, "E518", {"start": v(-15.2, 5.08) * mm, "end": v(-15.2, 35.34) * mm, "construction": true});
            skLineSegment(sketch, "E519.MirrorCS", {"start": v(-15.2, 5.08) * mm, "end": v(-25.6, 34.3) * mm});
            skLineSegment(sketch, "E520.MirrorCS", {"start": v(-25.6, 34.3) * mm, "end": v(-36.38, 5.08) * mm});
            skLineSegment(sketch, "E521.MirrorCS", {"start": v(-25.6, 14.6) * mm, "end": v(-22.2, 5.08) * mm});
            skLineSegment(sketch, "E522.MirrorCS", {"start": v(-29.1, 5.08) * mm, "end": v(-25.6, 14.6) * mm});
            skLineSegment(sketch, "E523.MirrorCS", {"start": v(-15.92, 7.08) * mm, "end": v(-35.64, 7.08) * mm});
            skLineSegment(sketch, "E524.MirrorCS", {"start": v(-17.88, 12.6) * mm, "end": v(-33.6, 12.6) * mm});
            skLineSegment(sketch, "E525.MirrorCS", {"start": v(-18.6, 14.6) * mm, "end": v(-32.86, 14.6) * mm});
            skLineSegment(sketch, "E526", {"start": v(-14.5, 7.08) * mm, "end": v(-15.92, 7.08) * mm});
            skLineSegment(sketch, "E527", {"start": v(27.13, 5.08) * mm, "end": v(27.13, 32.32) * mm, "construction": true});
            skLineSegment(sketch, "E528", {"start": v(26.42, 7.08) * mm, "end": v(27.84, 7.08) * mm});
            skSolve(sketch);
        }
        {
            var Q0;
            {var subQ0=sQuery(id+"F2.wireOp",EDGE,"E513.MirrorCS");var subQ1=sQuery(id+"F2.wireOp",EDGE,"E511.MirrorCS");var subQ2=makeQuery(id+"F2.imprint","INTERSECT",VERTEX,{"derivedFrom":[subQ1,subQ0]});Q0=makeQuery(id+"F2.imprint","IMPRINT",FACE,{"disambiguationData":[TD([[makeQuery(id+"F2.imprint","IMPRINT",EDGE,{"disambiguationData":[TD([[subQ2,1.0]])],"derivedFrom":subQ1}),-1.0]])]});}
            var Q1;
            {var subQ0=sQuery(id+"F2.wireOp",EDGE,"E512.MirrorCS");var subQ1=sQuery(id+"F2.wireOp",EDGE,"E510.MirrorCS");var subQ2=makeQuery(id+"F2.imprint","INTERSECT",VERTEX,{"derivedFrom":[subQ1,subQ0]});Q1=makeQuery(id+"F2.imprint","IMPRINT",FACE,{"disambiguationData":[TD([[makeQuery(id+"F2.imprint","IMPRINT",EDGE,{"disambiguationData":[TD([[subQ2,-1.0]])],"derivedFrom":subQ1}),-1.0]])]});}
            var Q2;
            {var subQ0=sQuery(id+"F2.wireOp",EDGE,"E515.MirrorCS");var subQ1=sQuery(id+"F2.wireOp",EDGE,"E513.MirrorCS");var subQ2=makeQuery(id+"F2.imprint","INTERSECT",VERTEX,{"derivedFrom":[subQ1,subQ0]});Q2=makeQuery(id+"F2.imprint","IMPRINT",FACE,{"disambiguationData":[TD([[makeQuery(id+"F2.imprint","IMPRINT",EDGE,{"disambiguationData":[TD([[subQ2,-1.0]])],"derivedFrom":subQ1}),1.0]])]});}
            var Q3;
            {var subQ0=sQuery(id+"F2.wireOp",EDGE,"E512.MirrorCS");var subQ1=sQuery(id+"F2.wireOp",EDGE,"E511.MirrorCS");var subQ2=makeQuery(id+"F2.imprint","INTERSECT",VERTEX,{"derivedFrom":[subQ1,subQ0]});Q3=makeQuery(id+"F2.imprint","IMPRINT",FACE,{"disambiguationData":[TD([[makeQuery(id+"F2.imprint","IMPRINT",EDGE,{"disambiguationData":[TD([[subQ2,1.0]])],"derivedFrom":subQ1}),-1.0]])]});}
            var Q4;
            {var subQ0=sQuery(id+"F2.wireOp",EDGE,"E513.MirrorCS");var subQ1=sQuery(id+"F2.wireOp",EDGE,"E510.MirrorCS");var subQ2=makeQuery(id+"F2.imprint","INTERSECT",VERTEX,{"derivedFrom":[subQ1,subQ0]});Q4=makeQuery(id+"F2.imprint","IMPRINT",FACE,{"disambiguationData":[TD([[makeQuery(id+"F2.imprint","IMPRINT",EDGE,{"disambiguationData":[TD([[subQ2,1.0]])],"derivedFrom":subQ0}),-1.0]])]});}
            var Q5;
            {var subQ3=sQuery(id+"F2.wireOp",EDGE,"E516.MirrorCS");var subQ5=sQuery(id+"F2.wireOp",EDGE,"E514.MirrorCS");var subQ7=makeQuery(id+"F2.imprint","INTERSECT",VERTEX,{"derivedFrom":[subQ5,subQ3]});Q5=makeQuery(id+"F2.imprint","IMPRINT",FACE,{"disambiguationData":[TD([[makeQuery(id+"F2.imprint","IMPRINT",EDGE,{"disambiguationData":[TD([[subQ7,1.0]])],"derivedFrom":subQ5}),-1.0]])]});}
            var Q6;
            {var subQ0=sQuery(id+"F2.wireOp",EDGE,"E514.MirrorCS");var subQ3=sQuery(id+"F2.wireOp",EDGE,"E516.MirrorCS");var subQ4=makeQuery(id+"F2.imprint","INTERSECT",VERTEX,{"derivedFrom":[subQ0,subQ3]});Q6=makeQuery(id+"F2.imprint","IMPRINT",FACE,{"disambiguationData":[TD([[makeQuery(id+"F2.imprint","IMPRINT",EDGE,{"disambiguationData":[TD([[subQ4,1.0]])],"derivedFrom":subQ3}),-1.0]])]});}
            var Q7;
            {var subQ0=sQuery(id+"F2.wireOp",EDGE,"E511.MirrorCS");var subQ3=sQuery(id+"F2.wireOp",EDGE,"E516.MirrorCS");var subQ4=makeQuery(id+"F2.imprint","INTERSECT",VERTEX,{"derivedFrom":[subQ0,subQ3]});Q7=makeQuery(id+"F2.imprint","IMPRINT",FACE,{"disambiguationData":[TD([[makeQuery(id+"F2.imprint","IMPRINT",EDGE,{"disambiguationData":[TD([[subQ4,-1.0]])],"derivedFrom":subQ3}),-1.0]])]});}
            var Q8;
            {var subQ3=sQuery(id+"F2.wireOp",EDGE,"E508");var subQ5=sQuery(id+"F2.wireOp",EDGE,"E504");var subQ7=makeQuery(id+"F2.imprint","INTERSECT",VERTEX,{"derivedFrom":[subQ5,subQ3]});Q8=makeQuery(id+"F2.imprint","IMPRINT",FACE,{"disambiguationData":[TD([[makeQuery(id+"F2.imprint","IMPRINT",EDGE,{"disambiguationData":[TD([[subQ7,1.0]])],"derivedFrom":subQ5}),1.0]])]});}
            var Q9;
            {var subQ3=sQuery(id+"F2.wireOp",EDGE,"E508");var subQ5=sQuery(id+"F2.wireOp",EDGE,"E504");var subQ6=makeQuery(id+"F2.imprint","INTERSECT",VERTEX,{"derivedFrom":[subQ5,subQ3]});Q9=makeQuery(id+"F2.imprint","IMPRINT",FACE,{"disambiguationData":[TD([[makeQuery(id+"F2.imprint","IMPRINT",EDGE,{"disambiguationData":[TD([[subQ6,-1.0]])],"derivedFrom":subQ5}),1.0]])]});}
            var Q10;
            {var subQ1=sQuery(id+"F2.wireOp",EDGE,"E504");var subQ3=sQuery(id+"F2.wireOp",EDGE,"E507");var subQ4=makeQuery(id+"F2.imprint","INTERSECT",VERTEX,{"derivedFrom":[subQ1,subQ3]});Q10=makeQuery(id+"F2.imprint","IMPRINT",FACE,{"disambiguationData":[TD([[makeQuery(id+"F2.imprint","IMPRINT",EDGE,{"disambiguationData":[TD([[subQ4,1.0]])],"derivedFrom":subQ3}),-1.0]])]});}
            var Q11;
            {var subQ0=sQuery(id+"F2.wireOp",EDGE,"E506");var subQ1=sQuery(id+"F2.wireOp",EDGE,"E502");var subQ2=makeQuery(id+"F2.imprint","INTERSECT",VERTEX,{"derivedFrom":[subQ1,subQ0]});Q11=makeQuery(id+"F2.imprint","IMPRINT",FACE,{"disambiguationData":[TD([[makeQuery(id+"F2.imprint","IMPRINT",EDGE,{"disambiguationData":[TD([[subQ2,1.0]])],"derivedFrom":subQ1}),1.0]])]});}
            var Q12;
            {var subQ0=sQuery(id+"F2.wireOp",EDGE,"E504");var subQ3=sQuery(id+"F2.wireOp",EDGE,"E508");var subQ4=makeQuery(id+"F2.imprint","INTERSECT",VERTEX,{"derivedFrom":[subQ0,subQ3]});Q12=makeQuery(id+"F2.imprint","IMPRINT",FACE,{"disambiguationData":[TD([[makeQuery(id+"F2.imprint","IMPRINT",EDGE,{"disambiguationData":[TD([[subQ4,1.0]])],"derivedFrom":subQ3}),1.0]])]});}
            var Q13;
            {var subQ0=sQuery(id+"F2.wireOp",EDGE,"E507");var subQ1=sQuery(id+"F2.wireOp",EDGE,"E502");var subQ2=makeQuery(id+"F2.imprint","INTERSECT",VERTEX,{"derivedFrom":[subQ1,subQ0]});Q13=makeQuery(id+"F2.imprint","IMPRINT",FACE,{"disambiguationData":[TD([[makeQuery(id+"F2.imprint","IMPRINT",EDGE,{"disambiguationData":[TD([[subQ2,1.0]])],"derivedFrom":subQ1}),1.0]])]});}
            var Q14;
            {var subQ0=sQuery(id+"F2.wireOp",EDGE,"E506");var subQ1=sQuery(id+"F2.wireOp",EDGE,"E503");var subQ2=makeQuery(id+"F2.imprint","INTERSECT",VERTEX,{"derivedFrom":[subQ1,subQ0]});Q14=makeQuery(id+"F2.imprint","IMPRINT",FACE,{"disambiguationData":[TD([[makeQuery(id+"F2.imprint","IMPRINT",EDGE,{"disambiguationData":[TD([[subQ2,-1.0]])],"derivedFrom":subQ1}),1.0]])]});}
            var Q15;
            {var subQ0=sQuery(id+"F2.wireOp",EDGE,"E502");var subQ3=sQuery(id+"F2.wireOp",EDGE,"E508");var subQ4=makeQuery(id+"F2.imprint","INTERSECT",VERTEX,{"derivedFrom":[subQ0,subQ3]});Q15=makeQuery(id+"F2.imprint","IMPRINT",FACE,{"disambiguationData":[TD([[makeQuery(id+"F2.imprint","IMPRINT",EDGE,{"disambiguationData":[TD([[subQ4,-1.0]])],"derivedFrom":subQ3}),1.0]])]});}
            var Q16;
            {var subQ3=sQuery(id+"F2.wireOp",EDGE,"E517");Q16=makeQuery(id+"F2.imprint","IMPRINT",FACE,{"disambiguationData":[TD([[makeQuery(id+"F2.imprint","IMPRINT",EDGE,{"derivedFrom":subQ3}),-1.0]])]});}
            var Q17;
            {var subQ0=sQuery(id+"F2.wireOp",EDGE,"E520.MirrorCS");var subQ3=sQuery(id+"F2.wireOp",EDGE,"E523.MirrorCS");var subQ4=makeQuery(id+"F2.imprint","INTERSECT",VERTEX,{"derivedFrom":[subQ0,subQ3]});Q17=makeQuery(id+"F2.imprint","IMPRINT",FACE,{"disambiguationData":[TD([[makeQuery(id+"F2.imprint","IMPRINT",EDGE,{"disambiguationData":[TD([[subQ4,1.0]])],"derivedFrom":subQ3}),1.0]])]});}
            var Q18;
            {var subQ0=sQuery(id+"F2.wireOp",EDGE,"E523.MirrorCS");var subQ1=sQuery(id+"F2.wireOp",EDGE,"E520.MirrorCS");var subQ2=makeQuery(id+"F2.imprint","INTERSECT",VERTEX,{"derivedFrom":[subQ1,subQ0]});Q18=makeQuery(id+"F2.imprint","IMPRINT",FACE,{"disambiguationData":[TD([[makeQuery(id+"F2.imprint","IMPRINT",EDGE,{"disambiguationData":[TD([[subQ2,1.0]])],"derivedFrom":subQ1}),1.0]])]});}
            var Q19;
            {var subQ0=sQuery(id+"F2.wireOp",EDGE,"E521.MirrorCS");var subQ3=sQuery(id+"F2.wireOp",EDGE,"E523.MirrorCS");var subQ4=makeQuery(id+"F2.imprint","INTERSECT",VERTEX,{"derivedFrom":[subQ0,subQ3]});Q19=makeQuery(id+"F2.imprint","IMPRINT",FACE,{"disambiguationData":[TD([[makeQuery(id+"F2.imprint","IMPRINT",EDGE,{"disambiguationData":[TD([[subQ4,-1.0]])],"derivedFrom":subQ3}),1.0]])]});}
            var Q20;
            {var subQ3=sQuery(id+"F2.wireOp",EDGE,"E523.MirrorCS");var subQ5=sQuery(id+"F2.wireOp",EDGE,"E521.MirrorCS");var subQ7=makeQuery(id+"F2.imprint","INTERSECT",VERTEX,{"derivedFrom":[subQ5,subQ3]});Q20=makeQuery(id+"F2.imprint","IMPRINT",FACE,{"disambiguationData":[TD([[makeQuery(id+"F2.imprint","IMPRINT",EDGE,{"disambiguationData":[TD([[subQ7,-1.0]])],"derivedFrom":subQ5}),1.0]])]});}
            var Q21;
            {var subQ3=sQuery(id+"F2.wireOp",EDGE,"E524.MirrorCS");var subQ5=sQuery(id+"F2.wireOp",EDGE,"E521.MirrorCS");var subQ6=makeQuery(id+"F2.imprint","INTERSECT",VERTEX,{"derivedFrom":[subQ5,subQ3]});Q21=makeQuery(id+"F2.imprint","IMPRINT",FACE,{"disambiguationData":[TD([[makeQuery(id+"F2.imprint","IMPRINT",EDGE,{"disambiguationData":[TD([[subQ6,-1.0]])],"derivedFrom":subQ5}),1.0]])]});}
            var Q22;
            {var subQ3=sQuery(id+"F2.wireOp",EDGE,"E526");Q22=makeQuery(id+"F2.imprint","IMPRINT",FACE,{"disambiguationData":[TD([[makeQuery(id+"F2.imprint","IMPRINT",EDGE,{"derivedFrom":subQ3}),1.0]])]});}
            var Q23;
            {var subQ0=sQuery(id+"F2.wireOp",EDGE,"E524.MirrorCS");var subQ1=sQuery(id+"F2.wireOp",EDGE,"E520.MirrorCS");var subQ2=makeQuery(id+"F2.imprint","INTERSECT",VERTEX,{"derivedFrom":[subQ1,subQ0]});Q23=makeQuery(id+"F2.imprint","IMPRINT",FACE,{"disambiguationData":[TD([[makeQuery(id+"F2.imprint","IMPRINT",EDGE,{"disambiguationData":[TD([[subQ2,1.0]])],"derivedFrom":subQ1}),1.0]])]});}
            var Q24;
            {var subQ0=sQuery(id+"F2.wireOp",EDGE,"E524.MirrorCS");var subQ1=sQuery(id+"F2.wireOp",EDGE,"E519.MirrorCS");var subQ2=makeQuery(id+"F2.imprint","INTERSECT",VERTEX,{"derivedFrom":[subQ1,subQ0]});Q24=makeQuery(id+"F2.imprint","IMPRINT",FACE,{"disambiguationData":[TD([[makeQuery(id+"F2.imprint","IMPRINT",EDGE,{"disambiguationData":[TD([[subQ2,-1.0]])],"derivedFrom":subQ1}),1.0]])]});}
            var Q25;
            {var subQ1=sQuery(id+"F2.wireOp",EDGE,"E521.MirrorCS");var subQ3=sQuery(id+"F2.wireOp",EDGE,"E524.MirrorCS");var subQ4=makeQuery(id+"F2.imprint","INTERSECT",VERTEX,{"derivedFrom":[subQ1,subQ3]});Q25=makeQuery(id+"F2.imprint","IMPRINT",FACE,{"disambiguationData":[TD([[makeQuery(id+"F2.imprint","IMPRINT",EDGE,{"disambiguationData":[TD([[subQ4,-1.0]])],"derivedFrom":subQ3}),-1.0]])]});}
            var Q26;
            {var subQ0=sQuery(id+"F2.wireOp",EDGE,"123b0633-e9c3-4d8f-8caa-eb3c23134d4b0.MirrorCS");var subQ1=sQuery(id+"F2.wireOp",EDGE,"4a4ab292-51dd-458c-aa99-028982b729380.MirrorCS");var subQ2=makeQuery(id+"F2.imprint","INTERSECT",VERTEX,{"derivedFrom":[subQ1,subQ0]});Q26=makeQuery(id+"F2.imprint","IMPRINT",FACE,{"disambiguationData":[TD([[makeQuery(id+"F2.imprint","IMPRINT",EDGE,{"disambiguationData":[TD([[subQ2,1.0]])],"derivedFrom":subQ1}),-1.0]])]});}
            var Q27;
            {var subQ0=sQuery(id+"F2.wireOp",EDGE,"123b0633-e9c3-4d8f-8caa-eb3c23134d4b0.MirrorCS");var subQ1=sQuery(id+"F2.wireOp",EDGE,"4a4ab292-51dd-458c-aa99-028982b729380.MirrorCS");var subQ2=makeQuery(id+"F2.imprint","INTERSECT",VERTEX,{"derivedFrom":[subQ1,subQ0]});Q27=makeQuery(id+"F2.imprint","IMPRINT",FACE,{"disambiguationData":[TD([[makeQuery(id+"F2.imprint","IMPRINT",EDGE,{"disambiguationData":[TD([[subQ2,-1.0]])],"derivedFrom":subQ1}),-1.0]])]});}
            var Q28;
            {var subQ0=sQuery(id+"F2.wireOp",EDGE,"123b0633-e9c3-4d8f-8caa-eb3c23134d4b0.MirrorCS");var subQ1=sQuery(id+"F2.wireOp",EDGE,"a192f13d-38c9-4a17-bca0-c32c0c851aed0.MirrorCS");var subQ2=makeQuery(id+"F2.imprint","INTERSECT",VERTEX,{"derivedFrom":[subQ1,subQ0]});Q28=makeQuery(id+"F2.imprint","IMPRINT",FACE,{"disambiguationData":[TD([[makeQuery(id+"F2.imprint","IMPRINT",EDGE,{"disambiguationData":[TD([[subQ2,1.0]])],"derivedFrom":subQ1}),-1.0]])]});}
            var Q29;
            {var subQ0=sQuery(id+"F2.wireOp",EDGE,"30fbd543-fbbf-43c3-8e79-c92e36c134c40.MirrorCS");var subQ1=sQuery(id+"F2.wireOp",EDGE,"123b0633-e9c3-4d8f-8caa-eb3c23134d4b0.MirrorCS");var subQ2=makeQuery(id+"F2.imprint","INTERSECT",VERTEX,{"derivedFrom":[subQ1,subQ0]});Q29=makeQuery(id+"F2.imprint","IMPRINT",FACE,{"disambiguationData":[TD([[makeQuery(id+"F2.imprint","IMPRINT",EDGE,{"disambiguationData":[TD([[subQ2,-1.0]])],"derivedFrom":subQ1}),1.0]])]});}
            var Q30;
            {var subQ0=sQuery(id+"F2.wireOp",EDGE,"123b0633-e9c3-4d8f-8caa-eb3c23134d4b0.MirrorCS");var subQ1=sQuery(id+"F2.wireOp",EDGE,"a192f13d-38c9-4a17-bca0-c32c0c851aed0.MirrorCS");var subQ2=makeQuery(id+"F2.imprint","INTERSECT",VERTEX,{"derivedFrom":[subQ1,subQ0]});Q30=makeQuery(id+"F2.imprint","IMPRINT",FACE,{"disambiguationData":[TD([[makeQuery(id+"F2.imprint","IMPRINT",EDGE,{"disambiguationData":[TD([[subQ2,1.0]])],"derivedFrom":subQ0}),-1.0]])]});}
            var Q31;
            {var subQ3=sQuery(id+"F2.wireOp",EDGE,"4b878aee-223c-4878-9fc0-5cc1982745620.MirrorCS");var subQ5=sQuery(id+"F2.wireOp",EDGE,"08371756-1cee-49c3-8ec5-516781062f8a0.MirrorCS");var subQ6=makeQuery(id+"F2.imprint","INTERSECT",VERTEX,{"derivedFrom":[subQ3,subQ5]});Q31=makeQuery(id+"F2.imprint","IMPRINT",FACE,{"disambiguationData":[TD([[makeQuery(id+"F2.imprint","IMPRINT",EDGE,{"disambiguationData":[TD([[subQ6,-1.0]])],"derivedFrom":subQ3}),-1.0]])]});}
            var Q32;
            {var subQ0=sQuery(id+"F2.wireOp",EDGE,"30fbd543-fbbf-43c3-8e79-c92e36c134c40.MirrorCS");var subQ1=sQuery(id+"F2.wireOp",EDGE,"4b878aee-223c-4878-9fc0-5cc1982745620.MirrorCS");var subQ2=makeQuery(id+"F2.imprint","INTERSECT",VERTEX,{"derivedFrom":[subQ1,subQ0]});Q32=makeQuery(id+"F2.imprint","IMPRINT",FACE,{"disambiguationData":[TD([[makeQuery(id+"F2.imprint","IMPRINT",EDGE,{"disambiguationData":[TD([[subQ2,-1.0]])],"derivedFrom":subQ1}),-1.0]])]});}
            var Q33;
            {var subQ0=sQuery(id+"F2.wireOp",EDGE,"4a4ab292-51dd-458c-aa99-028982b729380.MirrorCS");var subQ3=sQuery(id+"F2.wireOp",EDGE,"4b878aee-223c-4878-9fc0-5cc1982745620.MirrorCS");var subQ4=makeQuery(id+"F2.imprint","INTERSECT",VERTEX,{"derivedFrom":[subQ0,subQ3]});Q33=makeQuery(id+"F2.imprint","IMPRINT",FACE,{"disambiguationData":[TD([[makeQuery(id+"F2.imprint","IMPRINT",EDGE,{"disambiguationData":[TD([[subQ4,-1.0]])],"derivedFrom":subQ3}),-1.0]])]});}
            var Q34;
            {var subQ0=sQuery(id+"F2.wireOp",EDGE,"8e2a2ccc-98a9-4138-9ab0-815458238a250.MirrorCS");var subQ1=sQuery(id+"F2.wireOp",EDGE,"4bbb00fc-2797-420c-bf34-4fd031abc2b10.MirrorCS");var subQ2=makeQuery(id+"F2.imprint","INTERSECT",VERTEX,{"derivedFrom":[subQ1,subQ0]});Q34=makeQuery(id+"F2.imprint","IMPRINT",FACE,{"disambiguationData":[TD([[makeQuery(id+"F2.imprint","IMPRINT",EDGE,{"disambiguationData":[TD([[subQ2,-1.0]])],"derivedFrom":subQ1}),1.0]])]});}
            var Q35;
            {var subQ0=sQuery(id+"F2.wireOp",EDGE,"8e2a2ccc-98a9-4138-9ab0-815458238a250.MirrorCS");var subQ1=sQuery(id+"F2.wireOp",EDGE,"5b930245-8816-43fa-bd4d-b8e34537e7050.MirrorCS");var subQ2=makeQuery(id+"F2.imprint","INTERSECT",VERTEX,{"derivedFrom":[subQ1,subQ0]});Q35=makeQuery(id+"F2.imprint","IMPRINT",FACE,{"disambiguationData":[TD([[makeQuery(id+"F2.imprint","IMPRINT",EDGE,{"disambiguationData":[TD([[subQ2,1.0]])],"derivedFrom":subQ1}),1.0]])]});}
            var Q36;
            {var subQ0=sQuery(id+"F2.wireOp",EDGE,"8b008e0e-9662-4d0d-9bf2-2f9cc21301950.MirrorCS");var subQ1=sQuery(id+"F2.wireOp",EDGE,"dd5926df-115c-492e-af38-fb9159792ec70.MirrorCS");var subQ2=makeQuery(id+"F2.imprint","INTERSECT",VERTEX,{"derivedFrom":[subQ1,subQ0]});Q36=makeQuery(id+"F2.imprint","IMPRINT",FACE,{"disambiguationData":[TD([[makeQuery(id+"F2.imprint","IMPRINT",EDGE,{"disambiguationData":[TD([[subQ2,-1.0]])],"derivedFrom":subQ1}),-1.0]])]});}
            var Q37;
            {var subQ1=sQuery(id+"F2.wireOp",EDGE,"4bbb00fc-2797-420c-bf34-4fd031abc2b10.MirrorCS");var subQ3=sQuery(id+"F2.wireOp",EDGE,"dd5926df-115c-492e-af38-fb9159792ec70.MirrorCS");var subQ4=makeQuery(id+"F2.imprint","INTERSECT",VERTEX,{"derivedFrom":[subQ1,subQ3]});Q37=makeQuery(id+"F2.imprint","IMPRINT",FACE,{"disambiguationData":[TD([[makeQuery(id+"F2.imprint","IMPRINT",EDGE,{"disambiguationData":[TD([[subQ4,1.0]])],"derivedFrom":subQ3}),1.0]])]});}
            var Q38;
            {var subQ3=sQuery(id+"F2.wireOp",EDGE,"3381025f-ecdf-4143-9fbf-dde5d61434980.MirrorCS");var subQ5=sQuery(id+"F2.wireOp",EDGE,"319a4433-90c5-4ef1-acbc-a89d884d17140.MirrorCS");var subQ7=makeQuery(id+"F2.imprint","INTERSECT",VERTEX,{"derivedFrom":[subQ5,subQ3]});Q38=makeQuery(id+"F2.imprint","IMPRINT",FACE,{"disambiguationData":[TD([[makeQuery(id+"F2.imprint","IMPRINT",EDGE,{"disambiguationData":[TD([[subQ7,1.0]])],"derivedFrom":subQ5}),1.0]])]});}
            var Q39;
            {var subQ0=sQuery(id+"F2.wireOp",EDGE,"319a4433-90c5-4ef1-acbc-a89d884d17140.MirrorCS");var subQ3=sQuery(id+"F2.wireOp",EDGE,"3381025f-ecdf-4143-9fbf-dde5d61434980.MirrorCS");var subQ4=makeQuery(id+"F2.imprint","INTERSECT",VERTEX,{"derivedFrom":[subQ0,subQ3]});Q39=makeQuery(id+"F2.imprint","IMPRINT",FACE,{"disambiguationData":[TD([[makeQuery(id+"F2.imprint","IMPRINT",EDGE,{"disambiguationData":[TD([[subQ4,1.0]])],"derivedFrom":subQ3}),1.0]])]});}
            var Q40;
            {var subQ0=sQuery(id+"F2.wireOp",EDGE,"5b930245-8816-43fa-bd4d-b8e34537e7050.MirrorCS");var subQ3=sQuery(id+"F2.wireOp",EDGE,"3381025f-ecdf-4143-9fbf-dde5d61434980.MirrorCS");var subQ4=makeQuery(id+"F2.imprint","INTERSECT",VERTEX,{"derivedFrom":[subQ0,subQ3]});Q40=makeQuery(id+"F2.imprint","IMPRINT",FACE,{"disambiguationData":[TD([[makeQuery(id+"F2.imprint","IMPRINT",EDGE,{"disambiguationData":[TD([[subQ4,-1.0]])],"derivedFrom":subQ3}),1.0]])]});}
            var Q41;
            {var subQ0=sQuery(id+"F2.wireOp",EDGE,"dd5926df-115c-492e-af38-fb9159792ec70.MirrorCS");var subQ1=sQuery(id+"F2.wireOp",EDGE,"5b930245-8816-43fa-bd4d-b8e34537e7050.MirrorCS");var subQ2=makeQuery(id+"F2.imprint","INTERSECT",VERTEX,{"derivedFrom":[subQ1,subQ0]});Q41=makeQuery(id+"F2.imprint","IMPRINT",FACE,{"disambiguationData":[TD([[makeQuery(id+"F2.imprint","IMPRINT",EDGE,{"disambiguationData":[TD([[subQ2,1.0]])],"derivedFrom":subQ1}),1.0]])]});}
            var Q42;
            {var subQ3=sQuery(id+"F2.wireOp",EDGE,"11e7c196-8995-468a-ac04-200424c3d07e0.MirrorCS");Q42=makeQuery(id+"F2.imprint","IMPRINT",FACE,{"disambiguationData":[TD([[makeQuery(id+"F2.imprint","IMPRINT",EDGE,{"derivedFrom":subQ3}),1.0]])]});}
            var Q43;
            {var subQ3=sQuery(id+"F2.wireOp",EDGE,"E528");Q43=makeQuery(id+"F2.imprint","IMPRINT",FACE,{"disambiguationData":[TD([[makeQuery(id+"F2.imprint","IMPRINT",EDGE,{"derivedFrom":subQ3}),-1.0]])]});}
            extrude(context, id + "F3", {"entities" : qUnion([Q0, Q1, Q2, Q3, Q4, Q5, Q6, Q7, Q8, Q9, Q10, Q11, Q12, Q13, Q14, Q15, Q16, Q17, Q18, Q19, Q20, Q21, Q22, Q23, Q24, Q25, Q26, Q27, Q28, Q29, Q30, Q31, Q32, Q33, Q34, Q35, Q36, Q37, Q38, Q39, Q40, Q41, Q42, Q43]), "operationType" : NewBodyOperationType.ADD, "oppositeDirection" : true, "depth" : 9 * mm, "offsetDistance" : 25 * mm});
        }
        {
            var Q0;
            Q0=makeQuery(id+"F3.opExtrude","SWEPT_FACE",FACE,{"disambiguationData":[OSD([sQuery(id+"F2.wireOp",EDGE,"E506")])]});
            var sketch = newSketch(context, id + "F4", { "sketchPlane" : qUnion([Q0])});
            skCircle(sketch, "E529.0", {"center": v(49.67, 73.42) * mm, "radius": 1.5 * mm});
            skCircle(sketch, "E529.1", {"center": v(49.67, 86.12) * mm, "radius": 1.5 * mm});
            skCircle(sketch, "E529.2", {"center": v(49.67, 98.82) * mm, "radius": 1.5 * mm});
            skLineSegment(sketch, "E529.3", {"start": v(45.17, 106.12) * mm, "end": v(54.17, 106.12) * mm});
            skLineSegment(sketch, "E529.4", {"start": v(54.17, 106.12) * mm, "end": v(54.17, 27.13) * mm});
            skLineSegment(sketch, "E529.5", {"start": v(45.17, 106.12) * mm, "end": v(45.17, 27.13) * mm});
            skLineSegment(sketch, "E529.6", {"start": v(45.17, -36.38) * mm, "end": v(45.17, -61.38) * mm});
            skLineSegment(sketch, "E529.7", {"start": v(45.17, -61.38) * mm, "end": v(54.17, -61.38) * mm});
            skLineSegment(sketch, "E529.8", {"start": v(54.17, -36.38) * mm, "end": v(54.17, -61.38) * mm});
            skCircle(sketch, "E529.9", {"center": v(49.67, -56.38) * mm, "radius": 1.5 * mm});
            skLineSegment(sketch, "E530", {"start": v(45.17, 27.13) * mm, "end": v(45.17, -36.38) * mm});
            skLineSegment(sketch, "E531", {"start": v(54.17, 27.13) * mm, "end": v(54.17, -36.38) * mm});
            skSolve(sketch);
        }
        {
            var Q0;
            Q0=makeQuery(id+"F4.imprint","IMPRINT",FACE,{"disambiguationData":[TD([[makeQuery(id+"F4.imprint","IMPRINT",EDGE,{"derivedFrom":sQuery(id+"F4.wireOp",EDGE,"E529.0")}),-1.0]])]});
            var Q1;
            {var subQ1=sQuery(id+"F4.wireOp",EDGE,"E529.6");Q1=makeQuery(id+"F4.imprint","IMPRINT",FACE,{"disambiguationData":[TD([[makeQuery(id+"F4.imprint","IMPRINT",EDGE,{"derivedFrom":subQ1}),1.0]])]});}
            var Q2;
            {var subQ1=sQuery(id+"F2.wireOp",EDGE,"E506");var subQ2=makeQuery(id+"F3.opExtrude","SWEPT_EDGE",EDGE,{"disambiguationData":[OSD([sQuery(id+"F2.wireOp",EDGE,"E502"),subQ1])]});Q2=makeQuery(id+"F4.imprint","IMPRINT",FACE,{"disambiguationData":[TD([[makeQuery(id+"F4.imprint","IMPRINT",EDGE,{"derivedFrom":subQ2}),-1.0]])]});}
            extrude(context, id + "F5", {"entities" : qUnion([Q0, Q1, Q2]), "operationType" : NewBodyOperationType.ADD, "depth" : 5.08 * mm, "offsetDistance" : 25 * mm});
        }
        {
            var Q0;
            {var subQ0=sQuery(id+"F0.wireOp",EDGE,"E59.right");var subQ1=sQuery(id+"F0.wireOp",EDGE,"E55.right");Q0=makeQuery(id+"F5.boolean.opBoolean","MERGE",FACE,{"derivedFrom":[makeQuery(id+"F3.boolean.opBoolean","MERGE",FACE,{"derivedFrom":[makeQuery(id+"F1.opExtrude","SWEPT_FACE",FACE,{"disambiguationData":[OSD([subQ1,subQ0])]}),makeQuery(id+"F3.opExtrude","CAP_FACE",FACE,{"disambiguationData":[OSD([subQ1,subQ0,sQuery(id+"F2.wireOp",EDGE,"E502"),sQuery(id+"F2.wireOp",EDGE,"E503"),sQuery(id+"F2.wireOp",EDGE,"E504"),sQuery(id+"F2.wireOp",EDGE,"E505"),sQuery(id+"F2.wireOp",EDGE,"E506"),sQuery(id+"F2.wireOp",EDGE,"E507"),sQuery(id+"F2.wireOp",EDGE,"E508"),sQuery(id+"F2.wireOp",EDGE,"E510.MirrorCS"),sQuery(id+"F2.wireOp",EDGE,"E511.MirrorCS"),sQuery(id+"F2.wireOp",EDGE,"E512.MirrorCS"),sQuery(id+"F2.wireOp",EDGE,"E513.MirrorCS"),sQuery(id+"F2.wireOp",EDGE,"E514.MirrorCS"),sQuery(id+"F2.wireOp",EDGE,"E515.MirrorCS"),sQuery(id+"F2.wireOp",EDGE,"E516.MirrorCS"),sQuery(id+"F2.wireOp",EDGE,"E517")])],"isStart":true})]}),makeQuery(id+"F5.opExtrude","SWEPT_FACE",FACE,{"disambiguationData":[OSD([sQuery(id+"F4.wireOp",EDGE,"E529.4"),sQuery(id+"F4.wireOp",EDGE,"E529.8"),sQuery(id+"F4.wireOp",EDGE,"E531")])]})]});}
            var sketch = newSketch(context, id + "F6", { "sketchPlane" : qUnion([Q0])});
            skLineSegment(sketch, "E532", {"start": v(-48.38, 25.08) * mm, "end": v(-61.38, 25.08) * mm});
            skLineSegment(sketch, "E533", {"start": v(-61.38, 25.08) * mm, "end": v(-61.38, 20) * mm});
            skLineSegment(sketch, "E534", {"start": v(-48.38, 25.08) * mm, "end": v(-28.45, 14.6) * mm});
            skLineSegment(sketch, "E535", {"start": v(-39.36, 14.6) * mm, "end": v(-49.63, 20) * mm});
            skLineSegment(sketch, "E536", {"start": v(-49.63, 20) * mm, "end": v(-61.38, 20) * mm});
            skLineSegment(sketch, "E537", {"start": v(-34.62, 9.84) * mm, "end": v(-61.38, 9.84) * mm});
            skLineSegment(sketch, "E538.MirrorCS", {"start": v(-48.38, -5.4) * mm, "end": v(-28.45, 5.08) * mm});
            skLineSegment(sketch, "E539.MirrorCS", {"start": v(-48.38, -5.4) * mm, "end": v(-61.38, -5.4) * mm});
            skLineSegment(sketch, "E540.MirrorCS", {"start": v(-61.38, -5.4) * mm, "end": v(-61.38, -0.32) * mm});
            skLineSegment(sketch, "E541.MirrorCS", {"start": v(-49.63, -0.32) * mm, "end": v(-61.38, -0.32) * mm});
            skLineSegment(sketch, "E542.MirrorCS", {"start": v(-39.36, 5.08) * mm, "end": v(-49.63, -0.32) * mm});
            skSolve(sketch);
        }
        {
            var Q0;
            {var subQ0=sQuery(id+"F6.wireOp",EDGE,"E532");Q0=makeQuery(id+"F6.imprint","IMPRINT",FACE,{"disambiguationData":[TD([[makeQuery(id+"F6.imprint","IMPRINT",EDGE,{"derivedFrom":subQ0}),1.0]])]});}
            var Q1;
            {var subQ0=sQuery(id+"F6.wireOp",EDGE,"5bfdd5a5-6efa-4a54-9add-7d60015b02190.MirrorCS");Q1=makeQuery(id+"F6.imprint","IMPRINT",FACE,{"disambiguationData":[TD([[makeQuery(id+"F6.imprint","IMPRINT",EDGE,{"derivedFrom":subQ0}),-1.0]])]});}
            var Q2;
            {var subQ0=sQuery(id+"F6.wireOp",EDGE,"E539.MirrorCS");Q2=makeQuery(id+"F6.imprint","IMPRINT",FACE,{"disambiguationData":[TD([[makeQuery(id+"F6.imprint","IMPRINT",EDGE,{"derivedFrom":subQ0}),-1.0]])]});}
            extrude(context, id + "F7", {"entities" : qUnion([Q0, Q1, Q2]), "operationType" : NewBodyOperationType.ADD, "oppositeDirection" : true, "depth" : 9 * mm, "offsetDistance" : 25 * mm});
        }
        {
            var Q0;
            Q0 = qSketchRegion(id + "F6", true);
            var Q1;
            {var subQ0=sQuery(id+"F6.wireOp",EDGE,"E535");Q1=makeQuery(id+"F6.imprint","IMPRINT",FACE,{"disambiguationData":[TD([[makeQuery(id+"F6.imprint","IMPRINT",EDGE,{"derivedFrom":subQ0}),1.0]])]});}
            var Q2;
            {var subQ0=sQuery(id+"F6.wireOp",EDGE,"321b92c2-a39f-4954-875b-2a5402b5bb2f0.MirrorCS");Q2=makeQuery(id+"F6.imprint","IMPRINT",FACE,{"disambiguationData":[TD([[makeQuery(id+"F6.imprint","IMPRINT",EDGE,{"derivedFrom":subQ0}),-1.0]])]});}
            var Q3;
            {var subQ0=sQuery(id+"F6.wireOp",EDGE,"E541.MirrorCS");Q3=makeQuery(id+"F6.imprint","IMPRINT",FACE,{"disambiguationData":[TD([[makeQuery(id+"F6.imprint","IMPRINT",EDGE,{"derivedFrom":subQ0}),-1.0]])]});}
            extrude(context, id + "F8", {"entities" : qUnion([Q0, Q1, Q2, Q3]), "operationType" : NewBodyOperationType.REMOVE, "oppositeDirection" : true, "depth" : 25 * mm, "offsetDistance" : 25 * mm});
        }
        {
            var Q0;
            Q0=makeQuery(id+"F7.opExtrude","SWEPT_FACE",FACE,{"disambiguationData":[OSD([sQuery(id+"F6.wireOp",EDGE,"E539.MirrorCS")])]});
            var sketch = newSketch(context, id + "F9", { "sketchPlane" : qUnion([Q0])});
            skCircle(sketch, "E543", {"center": v(49.67, 56.38) * mm, "radius": 1.5 * mm});
            skPoint(sketch, "E543.centerSnap0", {"position": v(49.67, 61.38) * mm});
            skSolve(sketch);
        }
        {
            var Q0;
            Q0=makeQuery(id+"F9.imprint","IMPRINT",FACE,{"disambiguationData":[TD([[makeQuery(id+"F9.imprint","IMPRINT",EDGE,{"derivedFrom":sQuery(id+"F9.wireOp",EDGE,"E543")}),1.0]])]});
            extrude(context, id + "F10", {"entities" : qUnion([Q0]), "operationType" : NewBodyOperationType.REMOVE, "oppositeDirection" : true, "depth" : 35 * mm, "offsetDistance" : 25 * mm});
        }
        {
            var Q0;
            Q0=makeQuery(id+"F1.opExtrude","SWEPT_FACE",FACE,{"disambiguationData":[OSD([sQuery(id+"F0.wireOp",EDGE,"E61.right")])]});
            var sketch = newSketch(context, id + "F11", { "sketchPlane" : qUnion([Q0])});
            skLineSegment(sketch, "E544", {"start": v(-12.87, 5.08) * mm, "end": v(-9.4, 14.6) * mm});
            skLineSegment(sketch, "E545", {"start": v(-9.4, 14.6) * mm, "end": v(-5.94, 5.08) * mm});
            skLineSegment(sketch, "E546", {"start": v(-19.87, 5.08) * mm, "end": v(-9.4, 33.84) * mm});
            skLineSegment(sketch, "E547", {"start": v(-9.4, 33.84) * mm, "end": v(1.06, 5.08) * mm});
            skLineSegment(sketch, "E548", {"start": v(-16.4, 14.6) * mm, "end": v(-2.4, 14.6) * mm});
            skLineSegment(sketch, "E549", {"start": v(-17.14, 12.6) * mm, "end": v(-1.68, 12.6) * mm});
            skLineSegment(sketch, "E550", {"start": v(-19.15, 7.08) * mm, "end": v(0.33, 7.08) * mm});
            skLineSegment(sketch, "E551", {"start": v(1.06, 5.08) * mm, "end": v(1.06, 33.84) * mm, "construction": true});
            skLineSegment(sketch, "E552.MirrorCS", {"start": v(11.53, 33.84) * mm, "end": v(1.06, 5.08) * mm});
            skLineSegment(sketch, "E553.MirrorCS", {"start": v(22, 5.08) * mm, "end": v(11.53, 33.84) * mm});
            skLineSegment(sketch, "E554.MirrorCS", {"start": v(18.53, 14.6) * mm, "end": v(4.53, 14.6) * mm});
            skLineSegment(sketch, "E555.MirrorCS", {"start": v(19.25, 12.6) * mm, "end": v(3.8, 12.6) * mm});
            skLineSegment(sketch, "E556.MirrorCS", {"start": v(15, 5.08) * mm, "end": v(11.53, 14.6) * mm});
            skLineSegment(sketch, "E557.MirrorCS", {"start": v(11.53, 14.6) * mm, "end": v(8.06, 5.08) * mm});
            skLineSegment(sketch, "E558", {"start": v(0.33, 7.08) * mm, "end": v(1.79, 7.08) * mm});
            skLineSegment(sketch, "E559", {"start": v(22, 5.08) * mm, "end": v(22, 33.84) * mm, "construction": true});
            skLineSegment(sketch, "E560.MirrorCS", {"start": v(22, 5.08) * mm, "end": v(32.46, 33.84) * mm});
            skLineSegment(sketch, "E561.MirrorCS", {"start": v(32.46, 33.84) * mm, "end": v(42.93, 5.08) * mm});
            skLineSegment(sketch, "E562.MirrorCS", {"start": v(25.46, 14.6) * mm, "end": v(39.46, 14.6) * mm});
            skLineSegment(sketch, "E563.MirrorCS", {"start": v(24.73, 12.6) * mm, "end": v(40.19, 12.6) * mm});
            skLineSegment(sketch, "E564.MirrorCS", {"start": v(29, 5.08) * mm, "end": v(32.46, 14.6) * mm});
            skLineSegment(sketch, "E565.MirrorCS", {"start": v(32.46, 14.6) * mm, "end": v(35.93, 5.08) * mm});
            skLineSegment(sketch, "E566", {"start": v(21.26, 7.08) * mm, "end": v(22.72, 7.08) * mm});
            skLineSegment(sketch, "E567.MirrorCS", {"start": v(21.26, 7.08) * mm, "end": v(1.79, 7.08) * mm});
            skLineSegment(sketch, "E568.MirrorCS", {"start": v(22.72, 7.08) * mm, "end": v(42.2, 7.08) * mm});
            skLineSegment(sketch, "E569.MirrorCS", {"start": v(43.65, 7.08) * mm, "end": v(42.2, 7.08) * mm});
            skSolve(sketch);
        }
        {
            var Q0;
            {var subQ1=makeQuery(id+"F1.opExtrude","CAP_EDGE",EDGE,{"disambiguationData":[OSD([sQuery(id+"F0.wireOp",EDGE,"E61.right")])],"isStart":false});var subQ5=sQuery(id+"F11.wireOp",EDGE,"E557.MirrorCS");var subQ6=makeQuery(id+"F11.imprint","INTERSECT",VERTEX,{"derivedFrom":[subQ1,subQ5]});Q0=makeQuery(id+"F11.imprint","IMPRINT",FACE,{"disambiguationData":[TD([[makeQuery(id+"F11.imprint","IMPRINT",EDGE,{"disambiguationData":[TD([[subQ6,1.0]])],"derivedFrom":subQ5}),-1.0]])]});}
            var Q1;
            {var subQ0=sQuery(id+"F11.wireOp",EDGE,"E555.MirrorCS");var subQ1=sQuery(id+"F11.wireOp",EDGE,"E552.MirrorCS");var subQ2=makeQuery(id+"F11.imprint","INTERSECT",VERTEX,{"derivedFrom":[subQ1,subQ0]});Q1=makeQuery(id+"F11.imprint","IMPRINT",FACE,{"disambiguationData":[TD([[makeQuery(id+"F11.imprint","IMPRINT",EDGE,{"disambiguationData":[TD([[subQ2,1.0]])],"derivedFrom":subQ0}),1.0]])]});}
            var Q2;
            {var subQ0=sQuery(id+"F11.wireOp",EDGE,"E554.MirrorCS");var subQ1=sQuery(id+"F11.wireOp",EDGE,"E552.MirrorCS");var subQ2=makeQuery(id+"F11.imprint","INTERSECT",VERTEX,{"derivedFrom":[subQ1,subQ0]});Q2=makeQuery(id+"F11.imprint","IMPRINT",FACE,{"disambiguationData":[TD([[makeQuery(id+"F11.imprint","IMPRINT",EDGE,{"disambiguationData":[TD([[subQ2,-1.0]])],"derivedFrom":subQ1}),1.0]])]});}
            var Q3;
            {var subQ0=sQuery(id+"F11.wireOp",EDGE,"E554.MirrorCS");var subQ1=sQuery(id+"F11.wireOp",EDGE,"E553.MirrorCS");var subQ2=makeQuery(id+"F11.imprint","INTERSECT",VERTEX,{"derivedFrom":[subQ1,subQ0]});Q3=makeQuery(id+"F11.imprint","IMPRINT",FACE,{"disambiguationData":[TD([[makeQuery(id+"F11.imprint","IMPRINT",EDGE,{"disambiguationData":[TD([[subQ2,1.0]])],"derivedFrom":subQ1}),1.0]])]});}
            var Q4;
            {var subQ0=sQuery(id+"F11.wireOp",EDGE,"E556.MirrorCS");var subQ1=sQuery(id+"F11.wireOp",EDGE,"E555.MirrorCS");var subQ2=makeQuery(id+"F11.imprint","INTERSECT",VERTEX,{"derivedFrom":[subQ1,subQ0]});Q4=makeQuery(id+"F11.imprint","IMPRINT",FACE,{"disambiguationData":[TD([[makeQuery(id+"F11.imprint","IMPRINT",EDGE,{"disambiguationData":[TD([[subQ2,-1.0]])],"derivedFrom":subQ1}),-1.0]])]});}
            var Q5;
            {var subQ0=sQuery(id+"F11.wireOp",EDGE,"E555.MirrorCS");var subQ1=sQuery(id+"F11.wireOp",EDGE,"E553.MirrorCS");var subQ2=makeQuery(id+"F11.imprint","INTERSECT",VERTEX,{"derivedFrom":[subQ1,subQ0]});Q5=makeQuery(id+"F11.imprint","IMPRINT",FACE,{"disambiguationData":[TD([[makeQuery(id+"F11.imprint","IMPRINT",EDGE,{"disambiguationData":[TD([[subQ2,-1.0]])],"derivedFrom":subQ0}),1.0]])]});}
            var Q6;
            {var subQ1=makeQuery(id+"F1.opExtrude","CAP_EDGE",EDGE,{"disambiguationData":[OSD([sQuery(id+"F0.wireOp",EDGE,"E61.right")])],"isStart":false});var subQ5=sQuery(id+"F11.wireOp",EDGE,"E556.MirrorCS");var subQ6=makeQuery(id+"F11.imprint","INTERSECT",VERTEX,{"derivedFrom":[subQ1,subQ5]});Q6=makeQuery(id+"F11.imprint","IMPRINT",FACE,{"disambiguationData":[TD([[makeQuery(id+"F11.imprint","IMPRINT",EDGE,{"disambiguationData":[TD([[subQ6,-1.0]])],"derivedFrom":subQ5}),-1.0]])]});}
            var Q7;
            {var subQ0=sQuery(id+"F11.wireOp",EDGE,"E556.MirrorCS");var subQ1=makeQuery(id+"F1.opExtrude","CAP_EDGE",EDGE,{"disambiguationData":[OSD([sQuery(id+"F0.wireOp",EDGE,"E61.right")])],"isStart":false});var subQ2=makeQuery(id+"F11.imprint","INTERSECT",VERTEX,{"derivedFrom":[subQ1,subQ0]});Q7=makeQuery(id+"F11.imprint","IMPRINT",FACE,{"disambiguationData":[TD([[makeQuery(id+"F11.imprint","IMPRINT",EDGE,{"disambiguationData":[TD([[subQ2,-1.0]])],"derivedFrom":subQ0}),1.0]])]});}
            var Q8;
            {var subQ0=sQuery(id+"F11.wireOp",EDGE,"E562.MirrorCS");var subQ1=sQuery(id+"F11.wireOp",EDGE,"E560.MirrorCS");var subQ2=makeQuery(id+"F11.imprint","INTERSECT",VERTEX,{"derivedFrom":[subQ1,subQ0]});Q8=makeQuery(id+"F11.imprint","IMPRINT",FACE,{"disambiguationData":[TD([[makeQuery(id+"F11.imprint","IMPRINT",EDGE,{"disambiguationData":[TD([[subQ2,1.0]])],"derivedFrom":subQ1}),-1.0]])]});}
            var Q9;
            {var subQ0=sQuery(id+"F11.wireOp",EDGE,"E562.MirrorCS");var subQ1=sQuery(id+"F11.wireOp",EDGE,"E561.MirrorCS");var subQ2=makeQuery(id+"F11.imprint","INTERSECT",VERTEX,{"derivedFrom":[subQ1,subQ0]});Q9=makeQuery(id+"F11.imprint","IMPRINT",FACE,{"disambiguationData":[TD([[makeQuery(id+"F11.imprint","IMPRINT",EDGE,{"disambiguationData":[TD([[subQ2,-1.0]])],"derivedFrom":subQ1}),-1.0]])]});}
            var Q10;
            {var subQ0=sQuery(id+"F11.wireOp",EDGE,"E564.MirrorCS");var subQ1=sQuery(id+"F11.wireOp",EDGE,"E563.MirrorCS");var subQ2=makeQuery(id+"F11.imprint","INTERSECT",VERTEX,{"derivedFrom":[subQ1,subQ0]});Q10=makeQuery(id+"F11.imprint","IMPRINT",FACE,{"disambiguationData":[TD([[makeQuery(id+"F11.imprint","IMPRINT",EDGE,{"disambiguationData":[TD([[subQ2,-1.0]])],"derivedFrom":subQ1}),1.0]])]});}
            var Q11;
            {var subQ0=sQuery(id+"F11.wireOp",EDGE,"E563.MirrorCS");var subQ1=sQuery(id+"F11.wireOp",EDGE,"E560.MirrorCS");var subQ2=makeQuery(id+"F11.imprint","INTERSECT",VERTEX,{"derivedFrom":[subQ1,subQ0]});Q11=makeQuery(id+"F11.imprint","IMPRINT",FACE,{"disambiguationData":[TD([[makeQuery(id+"F11.imprint","IMPRINT",EDGE,{"disambiguationData":[TD([[subQ2,-1.0]])],"derivedFrom":subQ0}),-1.0]])]});}
            var Q12;
            {var subQ0=sQuery(id+"F11.wireOp",EDGE,"E563.MirrorCS");var subQ1=sQuery(id+"F11.wireOp",EDGE,"E561.MirrorCS");var subQ2=makeQuery(id+"F11.imprint","INTERSECT",VERTEX,{"derivedFrom":[subQ1,subQ0]});Q12=makeQuery(id+"F11.imprint","IMPRINT",FACE,{"disambiguationData":[TD([[makeQuery(id+"F11.imprint","IMPRINT",EDGE,{"disambiguationData":[TD([[subQ2,-1.0]])],"derivedFrom":subQ1}),-1.0]])]});}
            var Q13;
            {var subQ0=sQuery(id+"F11.wireOp",EDGE,"E561.MirrorCS");var subQ1=makeQuery(id+"F1.opExtrude","CAP_EDGE",EDGE,{"disambiguationData":[OSD([sQuery(id+"F0.wireOp",EDGE,"E61.right")])],"isStart":false});var subQ2=makeQuery(id+"F11.imprint","INTERSECT",VERTEX,{"derivedFrom":[subQ1,subQ0]});Q13=makeQuery(id+"F11.imprint","IMPRINT",FACE,{"disambiguationData":[TD([[makeQuery(id+"F11.imprint","IMPRINT",EDGE,{"disambiguationData":[TD([[subQ2,1.0]])],"derivedFrom":subQ0}),-1.0]])]});}
            var Q14;
            {var subQ0=sQuery(id+"F11.wireOp",EDGE,"E564.MirrorCS");var subQ1=makeQuery(id+"F1.opExtrude","CAP_EDGE",EDGE,{"disambiguationData":[OSD([sQuery(id+"F0.wireOp",EDGE,"E61.right")])],"isStart":false});var subQ2=makeQuery(id+"F11.imprint","INTERSECT",VERTEX,{"derivedFrom":[subQ1,subQ0]});Q14=makeQuery(id+"F11.imprint","IMPRINT",FACE,{"disambiguationData":[TD([[makeQuery(id+"F11.imprint","IMPRINT",EDGE,{"disambiguationData":[TD([[subQ2,-1.0]])],"derivedFrom":subQ0}),-1.0]])]});}
            var Q15;
            {var subQ1=makeQuery(id+"F1.opExtrude","CAP_EDGE",EDGE,{"disambiguationData":[OSD([sQuery(id+"F0.wireOp",EDGE,"E61.right")])],"isStart":false});var subQ5=sQuery(id+"F11.wireOp",EDGE,"E564.MirrorCS");var subQ6=makeQuery(id+"F11.imprint","INTERSECT",VERTEX,{"derivedFrom":[subQ1,subQ5]});Q15=makeQuery(id+"F11.imprint","IMPRINT",FACE,{"disambiguationData":[TD([[makeQuery(id+"F11.imprint","IMPRINT",EDGE,{"disambiguationData":[TD([[subQ6,-1.0]])],"derivedFrom":subQ5}),1.0]])]});}
            var Q16;
            {var subQ3=sQuery(id+"F11.wireOp",EDGE,"E566");Q16=makeQuery(id+"F11.imprint","IMPRINT",FACE,{"disambiguationData":[TD([[makeQuery(id+"F11.imprint","IMPRINT",EDGE,{"derivedFrom":subQ3}),-1.0]])]});}
            var Q17;
            {var subQ0=sQuery(id+"F11.wireOp",EDGE,"E550");var subQ1=sQuery(id+"F11.wireOp",EDGE,"E544");var subQ2=makeQuery(id+"F11.imprint","INTERSECT",VERTEX,{"derivedFrom":[subQ1,subQ0]});Q17=makeQuery(id+"F11.imprint","IMPRINT",FACE,{"disambiguationData":[TD([[makeQuery(id+"F11.imprint","IMPRINT",EDGE,{"disambiguationData":[TD([[subQ2,-1.0]])],"derivedFrom":subQ1}),1.0]])]});}
            var Q18;
            {var subQ0=sQuery(id+"F11.wireOp",EDGE,"E544");var subQ1=makeQuery(id+"F1.opExtrude","CAP_EDGE",EDGE,{"disambiguationData":[OSD([sQuery(id+"F0.wireOp",EDGE,"E61.right")])],"isStart":false});var subQ2=makeQuery(id+"F11.imprint","INTERSECT",VERTEX,{"derivedFrom":[subQ1,subQ0]});Q18=makeQuery(id+"F11.imprint","IMPRINT",FACE,{"disambiguationData":[TD([[makeQuery(id+"F11.imprint","IMPRINT",EDGE,{"disambiguationData":[TD([[subQ2,-1.0]])],"derivedFrom":subQ0}),1.0]])]});}
            var Q19;
            {var subQ0=sQuery(id+"F11.wireOp",EDGE,"E544");var subQ1=makeQuery(id+"F1.opExtrude","CAP_EDGE",EDGE,{"disambiguationData":[OSD([sQuery(id+"F0.wireOp",EDGE,"E61.right")])],"isStart":false});var subQ2=makeQuery(id+"F11.imprint","INTERSECT",VERTEX,{"derivedFrom":[subQ1,subQ0]});Q19=makeQuery(id+"F11.imprint","IMPRINT",FACE,{"disambiguationData":[TD([[makeQuery(id+"F11.imprint","IMPRINT",EDGE,{"disambiguationData":[TD([[subQ2,-1.0]])],"derivedFrom":subQ0}),-1.0]])]});}
            var Q20;
            {var subQ0=sQuery(id+"F11.wireOp",EDGE,"E545");var subQ1=makeQuery(id+"F1.opExtrude","CAP_EDGE",EDGE,{"disambiguationData":[OSD([sQuery(id+"F0.wireOp",EDGE,"E61.right")])],"isStart":false});var subQ2=makeQuery(id+"F11.imprint","INTERSECT",VERTEX,{"derivedFrom":[subQ1,subQ0]});Q20=makeQuery(id+"F11.imprint","IMPRINT",FACE,{"disambiguationData":[TD([[makeQuery(id+"F11.imprint","IMPRINT",EDGE,{"disambiguationData":[TD([[subQ2,1.0]])],"derivedFrom":subQ0}),1.0]])]});}
            var Q21;
            {var subQ0=sQuery(id+"F11.wireOp",EDGE,"E549");var subQ1=sQuery(id+"F11.wireOp",EDGE,"E545");var subQ2=makeQuery(id+"F11.imprint","INTERSECT",VERTEX,{"derivedFrom":[subQ1,subQ0]});Q21=makeQuery(id+"F11.imprint","IMPRINT",FACE,{"disambiguationData":[TD([[makeQuery(id+"F11.imprint","IMPRINT",EDGE,{"disambiguationData":[TD([[subQ2,-1.0]])],"derivedFrom":subQ1}),1.0]])]});}
            var Q22;
            {var subQ0=sQuery(id+"F11.wireOp",EDGE,"E548");var subQ5=sQuery(id+"F11.wireOp",EDGE,"E547");var subQ7=makeQuery(id+"F11.imprint","INTERSECT",VERTEX,{"derivedFrom":[subQ5,subQ0]});Q22=makeQuery(id+"F11.imprint","IMPRINT",FACE,{"disambiguationData":[TD([[makeQuery(id+"F11.imprint","IMPRINT",EDGE,{"disambiguationData":[TD([[subQ7,-1.0]])],"derivedFrom":subQ5}),-1.0]])]});}
            var Q23;
            {var subQ1=sQuery(id+"F11.wireOp",EDGE,"E544");var subQ3=sQuery(id+"F11.wireOp",EDGE,"E549");var subQ4=makeQuery(id+"F11.imprint","INTERSECT",VERTEX,{"derivedFrom":[subQ1,subQ3]});Q23=makeQuery(id+"F11.imprint","IMPRINT",FACE,{"disambiguationData":[TD([[makeQuery(id+"F11.imprint","IMPRINT",EDGE,{"disambiguationData":[TD([[subQ4,-1.0]])],"derivedFrom":subQ3}),1.0]])]});}
            var Q24;
            {var subQ0=sQuery(id+"F11.wireOp",EDGE,"E548");var subQ5=sQuery(id+"F11.wireOp",EDGE,"E546");var subQ6=makeQuery(id+"F11.imprint","INTERSECT",VERTEX,{"derivedFrom":[subQ5,subQ0]});Q24=makeQuery(id+"F11.imprint","IMPRINT",FACE,{"disambiguationData":[TD([[makeQuery(id+"F11.imprint","IMPRINT",EDGE,{"disambiguationData":[TD([[subQ6,1.0]])],"derivedFrom":subQ5}),-1.0]])]});}
            var Q25;
            {var subQ3=sQuery(id+"F11.wireOp",EDGE,"E558");Q25=makeQuery(id+"F11.imprint","IMPRINT",FACE,{"disambiguationData":[TD([[makeQuery(id+"F11.imprint","IMPRINT",EDGE,{"derivedFrom":subQ3}),-1.0]])]});}
            var Q26;
            {var subQ0=sQuery(id+"F11.wireOp",EDGE,"e4547195-d6ea-436c-a227-9162296988530.MirrorCS");var subQ1=sQuery(id+"F11.wireOp",EDGE,"88762fb8-f6bd-4012-b8e3-790002d080130.MirrorCS");var subQ2=makeQuery(id+"F11.imprint","INTERSECT",VERTEX,{"derivedFrom":[subQ1,subQ0]});Q26=makeQuery(id+"F11.imprint","IMPRINT",FACE,{"disambiguationData":[TD([[makeQuery(id+"F11.imprint","IMPRINT",EDGE,{"disambiguationData":[TD([[subQ2,-1.0]])],"derivedFrom":subQ1}),-1.0]])]});}
            var Q27;
            {var subQ0=sQuery(id+"F11.wireOp",EDGE,"88762fb8-f6bd-4012-b8e3-790002d080130.MirrorCS");var subQ1=sQuery(id+"F11.wireOp",EDGE,"01193295-7ec9-427c-91b4-f16029f9f8a30.MirrorCS");var subQ2=makeQuery(id+"F11.imprint","INTERSECT",VERTEX,{"derivedFrom":[subQ1,subQ0]});Q27=makeQuery(id+"F11.imprint","IMPRINT",FACE,{"disambiguationData":[TD([[makeQuery(id+"F11.imprint","IMPRINT",EDGE,{"disambiguationData":[TD([[subQ2,1.0]])],"derivedFrom":subQ0}),1.0]])]});}
            var Q28;
            {var subQ0=sQuery(id+"F11.wireOp",EDGE,"e4547195-d6ea-436c-a227-9162296988530.MirrorCS");var subQ1=makeQuery(id+"F1.opExtrude","CAP_EDGE",EDGE,{"disambiguationData":[OSD([sQuery(id+"F0.wireOp",EDGE,"E61.right")])],"isStart":false});var subQ2=makeQuery(id+"F11.imprint","INTERSECT",VERTEX,{"derivedFrom":[subQ1,subQ0]});Q28=makeQuery(id+"F11.imprint","IMPRINT",FACE,{"disambiguationData":[TD([[makeQuery(id+"F11.imprint","IMPRINT",EDGE,{"disambiguationData":[TD([[subQ2,-1.0]])],"derivedFrom":subQ0}),1.0]])]});}
            var Q29;
            {var subQ1=makeQuery(id+"F1.opExtrude","CAP_EDGE",EDGE,{"disambiguationData":[OSD([sQuery(id+"F0.wireOp",EDGE,"E61.right")])],"isStart":false});var subQ5=sQuery(id+"F11.wireOp",EDGE,"f563f4aa-8b0f-4fc6-b81a-003d91e410070.MirrorCS");var subQ6=makeQuery(id+"F11.imprint","INTERSECT",VERTEX,{"derivedFrom":[subQ1,subQ5]});Q29=makeQuery(id+"F11.imprint","IMPRINT",FACE,{"disambiguationData":[TD([[makeQuery(id+"F11.imprint","IMPRINT",EDGE,{"disambiguationData":[TD([[subQ6,1.0]])],"derivedFrom":subQ5}),-1.0]])]});}
            var Q30;
            {var subQ0=sQuery(id+"F11.wireOp",EDGE,"e27e7087-69ae-4157-97e2-bee256b5dc540.MirrorCS");var subQ1=sQuery(id+"F11.wireOp",EDGE,"01193295-7ec9-427c-91b4-f16029f9f8a30.MirrorCS");var subQ2=makeQuery(id+"F11.imprint","INTERSECT",VERTEX,{"derivedFrom":[subQ1,subQ0]});Q30=makeQuery(id+"F11.imprint","IMPRINT",FACE,{"disambiguationData":[TD([[makeQuery(id+"F11.imprint","IMPRINT",EDGE,{"disambiguationData":[TD([[subQ2,-1.0]])],"derivedFrom":subQ1}),1.0]])]});}
            var Q31;
            {var subQ0=sQuery(id+"F11.wireOp",EDGE,"e27e7087-69ae-4157-97e2-bee256b5dc540.MirrorCS");var subQ1=sQuery(id+"F11.wireOp",EDGE,"0308581d-1ea2-4f0f-9d34-a10d6036e8220.MirrorCS");var subQ2=makeQuery(id+"F11.imprint","INTERSECT",VERTEX,{"derivedFrom":[subQ1,subQ0]});Q31=makeQuery(id+"F11.imprint","IMPRINT",FACE,{"disambiguationData":[TD([[makeQuery(id+"F11.imprint","IMPRINT",EDGE,{"disambiguationData":[TD([[subQ2,1.0]])],"derivedFrom":subQ1}),1.0]])]});}
            var Q32;
            {var subQ0=sQuery(id+"F11.wireOp",EDGE,"88762fb8-f6bd-4012-b8e3-790002d080130.MirrorCS");var subQ1=sQuery(id+"F11.wireOp",EDGE,"0308581d-1ea2-4f0f-9d34-a10d6036e8220.MirrorCS");var subQ2=makeQuery(id+"F11.imprint","INTERSECT",VERTEX,{"derivedFrom":[subQ1,subQ0]});Q32=makeQuery(id+"F11.imprint","IMPRINT",FACE,{"disambiguationData":[TD([[makeQuery(id+"F11.imprint","IMPRINT",EDGE,{"disambiguationData":[TD([[subQ2,1.0]])],"derivedFrom":subQ1}),1.0]])]});}
            var Q33;
            {var subQ0=sQuery(id+"F11.wireOp",EDGE,"0308581d-1ea2-4f0f-9d34-a10d6036e8220.MirrorCS");var subQ1=makeQuery(id+"F1.opExtrude","CAP_EDGE",EDGE,{"disambiguationData":[OSD([sQuery(id+"F0.wireOp",EDGE,"E61.right")])],"isStart":false});var subQ2=makeQuery(id+"F11.imprint","INTERSECT",VERTEX,{"derivedFrom":[subQ1,subQ0]});Q33=makeQuery(id+"F11.imprint","IMPRINT",FACE,{"disambiguationData":[TD([[makeQuery(id+"F11.imprint","IMPRINT",EDGE,{"disambiguationData":[TD([[subQ2,-1.0]])],"derivedFrom":subQ0}),1.0]])]});}
            extrude(context, id + "F12", {"entities" : qUnion([Q0, Q1, Q2, Q3, Q4, Q5, Q6, Q7, Q8, Q9, Q10, Q11, Q12, Q13, Q14, Q15, Q16, Q17, Q18, Q19, Q20, Q21, Q22, Q23, Q24, Q25, Q26, Q27, Q28, Q29, Q30, Q31, Q32, Q33]), "operationType" : NewBodyOperationType.ADD, "oppositeDirection" : true, "depth" : 9 * mm, "offsetDistance" : 25 * mm});
        }
        {
            var Q0;
            Q0=makeQuery(id+"F12.opExtrude","SWEPT_FACE",FACE,{"disambiguationData":[OSD([sQuery(id+"F11.wireOp",EDGE,"E548")])]});
            var sketch = newSketch(context, id + "F13", { "sketchPlane" : qUnion([Q0])});
            skLineSegment(sketch, "E570.0", {"start": v(82.38, -35.87) * mm, "end": v(91.38, -35.87) * mm});
            skCircle(sketch, "E570.1", {"center": v(86.88, -30.87) * mm, "radius": 1.5 * mm});
            skCircle(sketch, "E570.2", {"center": v(86.88, 86.63) * mm, "radius": 1.5 * mm});
            skLineSegment(sketch, "E570.3", {"start": v(82.38, 91.63) * mm, "end": v(91.38, 91.63) * mm});
            skLineSegment(sketch, "E571", {"start": v(91.38, -35.87) * mm, "end": v(91.38, 91.63) * mm});
            skLineSegment(sketch, "E572", {"start": v(82.38, -35.87) * mm, "end": v(82.38, 91.63) * mm});
            skSolve(sketch);
        }
        {
            var Q0;
            {var subQ2=sQuery(id+"F13.wireOp",EDGE,"E570.0");Q0=makeQuery(id+"F13.imprint","IMPRINT",FACE,{"disambiguationData":[TD([[makeQuery(id+"F13.imprint","IMPRINT",EDGE,{"derivedFrom":subQ2}),1.0]])]});}
            var Q1;
            {var subQ1=sQuery(id+"F11.wireOp",EDGE,"E548");var subQ2=makeQuery(id+"F12.opExtrude","SWEPT_EDGE",EDGE,{"disambiguationData":[OSD([sQuery(id+"F11.wireOp",EDGE,"E546"),subQ1])]});Q1=makeQuery(id+"F13.imprint","IMPRINT",FACE,{"disambiguationData":[TD([[makeQuery(id+"F13.imprint","IMPRINT",EDGE,{"derivedFrom":subQ2}),1.0]])]});}
            var Q2;
            Q2=makeQuery(id+"F13.imprint","IMPRINT",FACE,{"disambiguationData":[TD([[makeQuery(id+"F13.imprint","IMPRINT",EDGE,{"derivedFrom":sQuery(id+"F13.wireOp",EDGE,"E570.2")}),-1.0]])]});
            extrude(context, id + "F14", {"entities" : qUnion([Q0, Q1, Q2]), "operationType" : NewBodyOperationType.ADD, "depth" : 5.08 * mm, "offsetDistance" : 25 * mm});
        }
        {
            var Q0;
            {var subQ0=sQuery(id+"F0.wireOp",EDGE,"E61.right");Q0=makeQuery(id+"F14.boolean.opBoolean","MERGE",FACE,{"derivedFrom":[makeQuery(id+"F12.boolean.opBoolean","MERGE",FACE,{"derivedFrom":[makeQuery(id+"F1.opExtrude","SWEPT_FACE",FACE,{"disambiguationData":[OSD([subQ0])]}),makeQuery(id+"F12.opExtrude","CAP_FACE",FACE,{"disambiguationData":[OSD([subQ0,sQuery(id+"F11.wireOp",EDGE,"E544"),sQuery(id+"F11.wireOp",EDGE,"E545"),sQuery(id+"F11.wireOp",EDGE,"E546"),sQuery(id+"F11.wireOp",EDGE,"E547"),sQuery(id+"F11.wireOp",EDGE,"E548"),sQuery(id+"F11.wireOp",EDGE,"E549"),sQuery(id+"F11.wireOp",EDGE,"E550"),sQuery(id+"F11.wireOp",EDGE,"E552.MirrorCS"),sQuery(id+"F11.wireOp",EDGE,"E553.MirrorCS"),sQuery(id+"F11.wireOp",EDGE,"E554.MirrorCS"),sQuery(id+"F11.wireOp",EDGE,"E555.MirrorCS"),sQuery(id+"F11.wireOp",EDGE,"E556.MirrorCS"),sQuery(id+"F11.wireOp",EDGE,"E557.MirrorCS"),sQuery(id+"F11.wireOp",EDGE,"E558"),sQuery(id+"F11.wireOp",EDGE,"E560.MirrorCS"),sQuery(id+"F11.wireOp",EDGE,"E561.MirrorCS"),sQuery(id+"F11.wireOp",EDGE,"E562.MirrorCS"),sQuery(id+"F11.wireOp",EDGE,"E563.MirrorCS"),sQuery(id+"F11.wireOp",EDGE,"E564.MirrorCS"),sQuery(id+"F11.wireOp",EDGE,"E565.MirrorCS"),sQuery(id+"F11.wireOp",EDGE,"E566"),sQuery(id+"F11.wireOp",EDGE,"E567.MirrorCS"),sQuery(id+"F11.wireOp",EDGE,"E568.MirrorCS")])],"isStart":true})]}),makeQuery(id+"F14.opExtrude","SWEPT_FACE",FACE,{"disambiguationData":[OSD([sQuery(id+"F13.wireOp",EDGE,"E571")])]})]});}
            var sketch = newSketch(context, id + "F15", { "sketchPlane" : qUnion([Q0])});
            skLineSegment(sketch, "E573", {"start": v(41.2, 9.84) * mm, "end": v(91.63, 9.84) * mm, "construction": true});
            skLineSegment(sketch, "E574", {"start": v(48.55, 9.84) * mm, "end": v(67.88, 20) * mm});
            skLineSegment(sketch, "E575", {"start": v(67.88, 20) * mm, "end": v(91.63, 20) * mm});
            skLineSegment(sketch, "E576", {"start": v(91.63, 20) * mm, "end": v(91.63, 25.08) * mm});
            skLineSegment(sketch, "E577", {"start": v(91.63, 25.08) * mm, "end": v(66.63, 25.08) * mm});
            skLineSegment(sketch, "E578", {"start": v(66.63, 25.08) * mm, "end": v(37.64, 9.84) * mm});
            skLineSegment(sketch, "E579.MirrorCS", {"start": v(48.55, 9.84) * mm, "end": v(67.88, -0.32) * mm});
            skLineSegment(sketch, "E580.MirrorCS", {"start": v(66.63, -5.4) * mm, "end": v(37.64, 9.84) * mm});
            skLineSegment(sketch, "E581.MirrorCS", {"start": v(91.63, -5.4) * mm, "end": v(66.63, -5.4) * mm});
            skLineSegment(sketch, "E582.MirrorCS", {"start": v(67.88, -0.32) * mm, "end": v(91.63, -0.32) * mm});
            skLineSegment(sketch, "E583.MirrorCS", {"start": v(91.63, -0.32) * mm, "end": v(91.63, -5.4) * mm});
            skSolve(sketch);
        }
        {
            var Q0;
            {var subQ0=sQuery(id+"F15.wireOp",EDGE,"E581.MirrorCS");Q0=makeQuery(id+"F15.imprint","IMPRINT",FACE,{"disambiguationData":[TD([[makeQuery(id+"F15.imprint","IMPRINT",EDGE,{"derivedFrom":subQ0}),-1.0]])]});}
            var Q1;
            {var subQ3=sQuery(id+"F15.wireOp",EDGE,"E577");Q1=makeQuery(id+"F15.imprint","IMPRINT",FACE,{"disambiguationData":[TD([[makeQuery(id+"F15.imprint","IMPRINT",EDGE,{"derivedFrom":subQ3}),1.0]])]});}
            extrude(context, id + "F16", {"entities" : qUnion([Q0, Q1]), "operationType" : NewBodyOperationType.ADD, "oppositeDirection" : true, "depth" : 9 * mm, "offsetDistance" : 25 * mm});
        }
        {
            var Q0;
            Q0=makeQuery(id+"F16.opExtrude","SWEPT_FACE",FACE,{"disambiguationData":[OSD([sQuery(id+"F15.wireOp",EDGE,"E577")])]});
            var sketch = newSketch(context, id + "F17", { "sketchPlane" : qUnion([Q0])});
            skPoint(sketch, "E584.centerSnap0", {"position": v(86.88, 91.63) * mm});
            skCircle(sketch, "E585.0", {"center": v(86.88, 86.63) * mm, "radius": 1.5 * mm});
            skSolve(sketch);
        }
        {
            var Q0;
            Q0 = qSketchRegion(id + "F17", true);
            extrude(context, id + "F18", {"entities" : qUnion([Q0]), "operationType" : NewBodyOperationType.REMOVE, "oppositeDirection" : true, "depth" : 35 * mm, "offsetDistance" : 25 * mm});
        }
        {
            var Q0;
            Q0=makeQuery(id+"F0.imprint","IMPRINT",FACE,{"disambiguationData":[TD([[makeQuery(id+"F0.imprint","IMPRINT",EDGE,{"derivedFrom":sQuery(id+"F0.wireOp",EDGE,"E64")}),1.0]])]});
            extrude(context, id + "F19", {"entities" : qUnion([Q0]), "depth" : 9.53 * mm, "offsetDistance" : 25 * mm});
        }
        {
            var Q0;
            Q0=makeQuery(id+"F1.opExtrude","SWEPT_EDGE",EDGE,{"disambiguationData":[OSD([sQuery(id+"F0.wireOp",EDGE,"E212"),sQuery(id+"F0.wireOp",EDGE,"E297")])]});
            var Q1;
            Q1=makeQuery(id+"F1.opExtrude","SWEPT_EDGE",EDGE,{"disambiguationData":[OSD([sQuery(id+"F0.wireOp",EDGE,"E212"),sQuery(id+"F0.wireOp",EDGE,"E298.MirrorCS")])]});
            var Q2;
            Q2=makeQuery(id+"F1.opExtrude","SWEPT_EDGE",EDGE,{"disambiguationData":[OSD([sQuery(id+"F0.wireOp",EDGE,"E0.bottom"),sQuery(id+"F0.wireOp",EDGE,"E0.right")])]});
            var Q3;
            Q3=makeQuery(id+"F1.opExtrude","SWEPT_EDGE",EDGE,{"disambiguationData":[OSD([sQuery(id+"F0.wireOp",EDGE,"E29.MirrorCS"),sQuery(id+"F0.wireOp",EDGE,"E30.MirrorCS")])]});
            var Q4;
            Q4=makeQuery(id+"F1.opExtrude","SWEPT_EDGE",EDGE,{"disambiguationData":[OSD([sQuery(id+"F0.wireOp",EDGE,"E17"),sQuery(id+"F0.wireOp",EDGE,"E29.MirrorCS")])]});
            var Q5;
            Q5=makeQuery(id+"F1.opExtrude","SWEPT_EDGE",EDGE,{"disambiguationData":[OSD([sQuery(id+"F0.wireOp",EDGE,"E20.MirrorCS"),sQuery(id+"F0.wireOp",EDGE,"E28")])]});
            var Q6;
            Q6=makeQuery(id+"F1.opExtrude","SWEPT_EDGE",EDGE,{"disambiguationData":[OSD([sQuery(id+"F0.wireOp",EDGE,"E27"),sQuery(id+"F0.wireOp",EDGE,"E28")])]});
            var Q7;
            Q7=makeQuery(id+"F1.opExtrude","SWEPT_EDGE",EDGE,{"disambiguationData":[OSD([sQuery(id+"F0.wireOp",EDGE,"E0.bottom"),sQuery(id+"F0.wireOp",EDGE,"E0.left")])]});
            var Q8;
            Q8=makeQuery(id+"F1.opExtrude","SWEPT_EDGE",EDGE,{"disambiguationData":[OSD([sQuery(id+"F0.wireOp",EDGE,"E16"),sQuery(id+"F0.wireOp",EDGE,"E18"),sQuery(id+"F0.wireOp",EDGE,"E25.MirrorCS")])]});
            var Q9;
            Q9=makeQuery(id+"F1.opExtrude","SWEPT_EDGE",EDGE,{"disambiguationData":[OSD([sQuery(id+"F0.wireOp",EDGE,"E19.MirrorCS"),sQuery(id+"F0.wireOp",EDGE,"E21.MirrorCS"),sQuery(id+"F0.wireOp",EDGE,"E22")])]});
            var Q10;
            Q10=makeQuery(id+"F1.opExtrude","SWEPT_EDGE",EDGE,{"disambiguationData":[OSD([sQuery(id+"F0.wireOp",EDGE,"E0.top"),sQuery(id+"F0.wireOp",EDGE,"E3")])]});
            var Q11;
            Q11=makeQuery(id+"F1.opExtrude","SWEPT_EDGE",EDGE,{"disambiguationData":[OSD([sQuery(id+"F0.wireOp",EDGE,"E3"),sQuery(id+"F0.wireOp",EDGE,"E46")])]});
            var Q12;
            Q12=makeQuery(id+"F1.opExtrude","SWEPT_EDGE",EDGE,{"disambiguationData":[OSD([sQuery(id+"F0.wireOp",EDGE,"E42"),sQuery(id+"F0.wireOp",EDGE,"E46")])]});
            var Q13;
            Q13=makeQuery(id+"F1.opExtrude","SWEPT_EDGE",EDGE,{"disambiguationData":[OSD([sQuery(id+"F0.wireOp",EDGE,"E43.MirrorCS"),sQuery(id+"F0.wireOp",EDGE,"E46")])]});
            var Q14;
            Q14=makeQuery(id+"F1.opExtrude","SWEPT_EDGE",EDGE,{"disambiguationData":[OSD([sQuery(id+"F0.wireOp",EDGE,"E5.MirrorCS"),sQuery(id+"F0.wireOp",EDGE,"E46")])]});
            var Q15;
            Q15=makeQuery(id+"F1.opExtrude","SWEPT_EDGE",EDGE,{"disambiguationData":[OSD([sQuery(id+"F0.wireOp",EDGE,"E0.top"),sQuery(id+"F0.wireOp",EDGE,"E5.MirrorCS")])]});
            var Q16;
            Q16=makeQuery(id+"F1.opExtrude","SWEPT_EDGE",EDGE,{"disambiguationData":[OSD([sQuery(id+"F0.wireOp",EDGE,"E2.top"),sQuery(id+"F0.wireOp",EDGE,"E2.left"),sQuery(id+"F0.wireOp",EDGE,"E22")])]});
            var Q17;
            Q17=makeQuery(id+"F1.opExtrude","SWEPT_EDGE",EDGE,{"disambiguationData":[OSD([sQuery(id+"F0.wireOp",EDGE,"E2.bottom"),sQuery(id+"F0.wireOp",EDGE,"E2.left"),sQuery(id+"F0.wireOp",EDGE,"E33.MirrorCS")])]});
            var Q18;
            Q18=makeQuery(id+"F1.opExtrude","SWEPT_EDGE",EDGE,{"disambiguationData":[OSD([sQuery(id+"F0.wireOp",EDGE,"E0.top"),sQuery(id+"F0.wireOp",EDGE,"E33.MirrorCS")])]});
            var Q19;
            Q19=makeQuery(id+"F1.opExtrude","SWEPT_EDGE",EDGE,{"disambiguationData":[OSD([sQuery(id+"F0.wireOp",EDGE,"E0.top"),sQuery(id+"F0.wireOp",EDGE,"E26")])]});
            var Q20;
            Q20=makeQuery(id+"F1.opExtrude","SWEPT_EDGE",EDGE,{"disambiguationData":[OSD([sQuery(id+"F0.wireOp",EDGE,"E19.MirrorCS"),sQuery(id+"F0.wireOp",EDGE,"E26")])]});
            var Q21;
            Q21=makeQuery(id+"F1.opExtrude","SWEPT_EDGE",EDGE,{"disambiguationData":[OSD([sQuery(id+"F0.wireOp",EDGE,"E0.top"),sQuery(id+"F0.wireOp",EDGE,"E31.MirrorCS")])]});
            var Q22;
            Q22=makeQuery(id+"F1.opExtrude","SWEPT_EDGE",EDGE,{"disambiguationData":[OSD([sQuery(id+"F0.wireOp",EDGE,"E0.top"),sQuery(id+"F0.wireOp",EDGE,"E32")])]});
            var Q23;
            Q23=makeQuery(id+"F1.opExtrude","SWEPT_EDGE",EDGE,{"disambiguationData":[OSD([sQuery(id+"F0.wireOp",EDGE,"E16"),sQuery(id+"F0.wireOp",EDGE,"E31.MirrorCS")])]});
            var Q24;
            Q24=makeQuery(id+"F1.opExtrude","SWEPT_EDGE",EDGE,{"disambiguationData":[OSD([sQuery(id+"F0.wireOp",EDGE,"E2.bottom"),sQuery(id+"F0.wireOp",EDGE,"E2.right"),sQuery(id+"F0.wireOp",EDGE,"E32")])]});
            var Q25;
            Q25=makeQuery(id+"F1.opExtrude","SWEPT_EDGE",EDGE,{"disambiguationData":[OSD([sQuery(id+"F0.wireOp",EDGE,"E2.top"),sQuery(id+"F0.wireOp",EDGE,"E2.right"),sQuery(id+"F0.wireOp",EDGE,"E25.MirrorCS")])]});
            var Q26;
            Q26=makeQuery(id+"F1.opExtrude","SWEPT_EDGE",EDGE,{"disambiguationData":[OSD([sQuery(id+"F0.wireOp",EDGE,"E10.bottom"),sQuery(id+"F0.wireOp",EDGE,"E11")])]});
            var Q27;
            Q27=makeQuery(id+"F1.opExtrude","SWEPT_EDGE",EDGE,{"disambiguationData":[OSD([sQuery(id+"F0.wireOp",EDGE,"E10.bottom"),sQuery(id+"F0.wireOp",EDGE,"E12")])]});
            var Q28;
            Q28=makeQuery(id+"F1.opExtrude","SWEPT_EDGE",EDGE,{"disambiguationData":[OSD([sQuery(id+"F0.wireOp",EDGE,"E112"),sQuery(id+"F0.wireOp",EDGE,"E113")])]});
            var Q29;
            Q29=makeQuery(id+"F1.opExtrude","SWEPT_EDGE",EDGE,{"disambiguationData":[OSD([sQuery(id+"F0.wireOp",EDGE,"E113"),sQuery(id+"F0.wireOp",EDGE,"E114")])]});
            var Q30;
            Q30=makeQuery(id+"F1.opExtrude","SWEPT_EDGE",EDGE,{"disambiguationData":[OSD([sQuery(id+"F0.wireOp",EDGE,"E129.bottom"),sQuery(id+"F0.wireOp",EDGE,"E129.right")])]});
            var Q31;
            Q31=makeQuery(id+"F1.opExtrude","SWEPT_EDGE",EDGE,{"disambiguationData":[OSD([sQuery(id+"F0.wireOp",EDGE,"E158.MirrorCS"),sQuery(id+"F0.wireOp",EDGE,"E159.MirrorCS")])]});
            var Q32;
            Q32=makeQuery(id+"F1.opExtrude","SWEPT_EDGE",EDGE,{"disambiguationData":[OSD([sQuery(id+"F0.wireOp",EDGE,"E146"),sQuery(id+"F0.wireOp",EDGE,"E158.MirrorCS")])]});
            var Q33;
            Q33=makeQuery(id+"F1.opExtrude","SWEPT_EDGE",EDGE,{"disambiguationData":[OSD([sQuery(id+"F0.wireOp",EDGE,"E149.MirrorCS"),sQuery(id+"F0.wireOp",EDGE,"E157")])]});
            var Q34;
            Q34=makeQuery(id+"F1.opExtrude","SWEPT_EDGE",EDGE,{"disambiguationData":[OSD([sQuery(id+"F0.wireOp",EDGE,"E156"),sQuery(id+"F0.wireOp",EDGE,"E157")])]});
            var Q35;
            Q35=makeQuery(id+"F1.opExtrude","SWEPT_EDGE",EDGE,{"disambiguationData":[OSD([sQuery(id+"F0.wireOp",EDGE,"E129.bottom"),sQuery(id+"F0.wireOp",EDGE,"E129.left")])]});
            var Q36;
            Q36=makeQuery(id+"F1.opExtrude","SWEPT_EDGE",EDGE,{"disambiguationData":[OSD([sQuery(id+"F0.wireOp",EDGE,"E129.top"),sQuery(id+"F0.wireOp",EDGE,"E160.MirrorCS")])]});
            var Q37;
            Q37=makeQuery(id+"F1.opExtrude","SWEPT_EDGE",EDGE,{"disambiguationData":[OSD([sQuery(id+"F0.wireOp",EDGE,"E129.top"),sQuery(id+"F0.wireOp",EDGE,"E161")])]});
            var Q38;
            Q38=makeQuery(id+"F1.opExtrude","SWEPT_EDGE",EDGE,{"disambiguationData":[OSD([sQuery(id+"F0.wireOp",EDGE,"E145"),sQuery(id+"F0.wireOp",EDGE,"E160.MirrorCS")])]});
            var Q39;
            Q39=makeQuery(id+"F1.opExtrude","SWEPT_EDGE",EDGE,{"disambiguationData":[OSD([sQuery(id+"F0.wireOp",EDGE,"E145"),sQuery(id+"F0.wireOp",EDGE,"E147"),sQuery(id+"F0.wireOp",EDGE,"E154.MirrorCS")])]});
            var Q40;
            Q40=makeQuery(id+"F1.opExtrude","SWEPT_EDGE",EDGE,{"disambiguationData":[OSD([sQuery(id+"F0.wireOp",EDGE,"E131.top"),sQuery(id+"F0.wireOp",EDGE,"E131.right"),sQuery(id+"F0.wireOp",EDGE,"E154.MirrorCS")])]});
            var Q41;
            Q41=makeQuery(id+"F1.opExtrude","SWEPT_EDGE",EDGE,{"disambiguationData":[OSD([sQuery(id+"F0.wireOp",EDGE,"E131.bottom"),sQuery(id+"F0.wireOp",EDGE,"E131.right"),sQuery(id+"F0.wireOp",EDGE,"E161")])]});
            var Q42;
            Q42=makeQuery(id+"F1.opExtrude","SWEPT_EDGE",EDGE,{"disambiguationData":[OSD([sQuery(id+"F0.wireOp",EDGE,"E132"),sQuery(id+"F0.wireOp",EDGE,"E175")])]});
            var Q43;
            Q43=makeQuery(id+"F1.opExtrude","SWEPT_EDGE",EDGE,{"disambiguationData":[OSD([sQuery(id+"F0.wireOp",EDGE,"E129.top"),sQuery(id+"F0.wireOp",EDGE,"E132")])]});
            var Q44;
            Q44=makeQuery(id+"F1.opExtrude","SWEPT_EDGE",EDGE,{"disambiguationData":[OSD([sQuery(id+"F0.wireOp",EDGE,"E139.bottom"),sQuery(id+"F0.wireOp",EDGE,"E140")])]});
            var Q45;
            Q45=makeQuery(id+"F1.opExtrude","SWEPT_EDGE",EDGE,{"disambiguationData":[OSD([sQuery(id+"F0.wireOp",EDGE,"E139.bottom"),sQuery(id+"F0.wireOp",EDGE,"E141")])]});
            var Q46;
            Q46=makeQuery(id+"F1.opExtrude","SWEPT_EDGE",EDGE,{"disambiguationData":[OSD([sQuery(id+"F0.wireOp",EDGE,"E131.top"),sQuery(id+"F0.wireOp",EDGE,"E131.left"),sQuery(id+"F0.wireOp",EDGE,"E151")])]});
            var Q47;
            Q47=makeQuery(id+"F1.opExtrude","SWEPT_EDGE",EDGE,{"disambiguationData":[OSD([sQuery(id+"F0.wireOp",EDGE,"E131.bottom"),sQuery(id+"F0.wireOp",EDGE,"E131.left"),sQuery(id+"F0.wireOp",EDGE,"E162.MirrorCS")])]});
            var Q48;
            Q48=makeQuery(id+"F1.opExtrude","SWEPT_EDGE",EDGE,{"disambiguationData":[OSD([sQuery(id+"F0.wireOp",EDGE,"E129.top"),sQuery(id+"F0.wireOp",EDGE,"E134.MirrorCS")])]});
            var Q49;
            Q49=makeQuery(id+"F1.opExtrude","SWEPT_EDGE",EDGE,{"disambiguationData":[OSD([sQuery(id+"F0.wireOp",EDGE,"E148.MirrorCS"),sQuery(id+"F0.wireOp",EDGE,"E150.MirrorCS"),sQuery(id+"F0.wireOp",EDGE,"E151")])]});
            var Q50;
            Q50=makeQuery(id+"F1.opExtrude","SWEPT_EDGE",EDGE,{"disambiguationData":[OSD([sQuery(id+"F0.wireOp",EDGE,"E148.MirrorCS"),sQuery(id+"F0.wireOp",EDGE,"E155")])]});
            var Q51;
            Q51=makeQuery(id+"F1.opExtrude","SWEPT_EDGE",EDGE,{"disambiguationData":[OSD([sQuery(id+"F0.wireOp",EDGE,"E129.top"),sQuery(id+"F0.wireOp",EDGE,"E155")])]});
            var Q52;
            Q52=makeQuery(id+"F1.opExtrude","SWEPT_EDGE",EDGE,{"disambiguationData":[OSD([sQuery(id+"F0.wireOp",EDGE,"E129.top"),sQuery(id+"F0.wireOp",EDGE,"E162.MirrorCS")])]});
            var Q53;
            Q53=makeQuery(id+"F1.opExtrude","SWEPT_EDGE",EDGE,{"disambiguationData":[OSD([sQuery(id+"F0.wireOp",EDGE,"E211"),sQuery(id+"F0.wireOp",EDGE,"E297")])]});
            var Q54;
            Q54=makeQuery(id+"F1.opExtrude","SWEPT_EDGE",EDGE,{"disambiguationData":[OSD([sQuery(id+"F0.wireOp",EDGE,"E211"),sQuery(id+"F0.wireOp",EDGE,"E298.MirrorCS")])]});
            var Q55;
            Q55=makeQuery(id+"F1.opExtrude","SWEPT_EDGE",EDGE,{"disambiguationData":[OSD([sQuery(id+"F0.wireOp",EDGE,"E224"),sQuery(id+"F0.wireOp",EDGE,"E225"),sQuery(id+"F0.wireOp",EDGE,"E231")])]});
            var Q56;
            Q56=makeQuery(id+"F1.opExtrude","SWEPT_EDGE",EDGE,{"disambiguationData":[OSD([sQuery(id+"F0.wireOp",EDGE,"E230"),sQuery(id+"F0.wireOp",EDGE,"E233")])]});
            var Q57;
            Q57=makeQuery(id+"F1.opExtrude","SWEPT_EDGE",EDGE,{"disambiguationData":[OSD([sQuery(id+"F0.wireOp",EDGE,"E299"),sQuery(id+"F0.wireOp",EDGE,"E303")])]});
            var Q58;
            Q58=makeQuery(id+"F1.opExtrude","SWEPT_EDGE",EDGE,{"disambiguationData":[OSD([sQuery(id+"F0.wireOp",EDGE,"E300"),sQuery(id+"F0.wireOp",EDGE,"E303")])]});
            var Q59;
            Q59=makeQuery(id+"F1.opExtrude","SWEPT_EDGE",EDGE,{"disambiguationData":[OSD([sQuery(id+"F0.wireOp",EDGE,"E299"),sQuery(id+"F0.wireOp",EDGE,"E304.MirrorCS")])]});
            var Q60;
            Q60=makeQuery(id+"F1.opExtrude","SWEPT_EDGE",EDGE,{"disambiguationData":[OSD([sQuery(id+"F0.wireOp",EDGE,"E300"),sQuery(id+"F0.wireOp",EDGE,"E304.MirrorCS")])]});
            fillet(context, id + "F20", {"entities" : qUnion([Q0, Q1, Q2, Q3, Q4, Q5, Q6, Q7, Q8, Q9, Q10, Q11, Q12, Q13, Q14, Q15, Q16, Q17, Q18, Q19, Q20, Q21, Q22, Q23, Q24, Q25, Q26, Q27, Q28, Q29, Q30, Q31, Q32, Q33, Q34, Q35, Q36, Q37, Q38, Q39, Q40, Q41, Q42, Q43, Q44, Q45, Q46, Q47, Q48, Q49, Q50, Q51, Q52, Q53, Q54, Q55, Q56, Q57, Q58, Q59, Q60]), "radius" : 5 * mm, "tangentPropagation" : true, "allowEdgeOverflow" : false});
        }
        {
            var Q0;
            Q0=makeQuery(id+"F14.opExtrude","SWEPT_FACE",FACE,{"disambiguationData":[OSD([sQuery(id+"F13.wireOp",EDGE,"E570.0")])]});
            var Q1;
            Q1=makeQuery(id+"F1.opExtrude","SWEPT_FACE",FACE,{"disambiguationData":[OSD([sQuery(id+"F0.wireOp",EDGE,"E61.top")])]});
            extrude(context, id + "F21", {"entities" : qUnion([Q0, Q1]), "operationType" : NewBodyOperationType.REMOVE, "oppositeDirection" : true, "depth" : 1 * mm, "offsetDistance" : 25 * mm});
        }
        {
            var Q0;
            {var subQ0=sQuery(id+"F0.wireOp",EDGE,"E61.right");var subQ1=sQuery(id+"F13.wireOp",EDGE,"E571");Q0=makeQuery(id+"F16.boolean.opBoolean","MERGE",FACE,{"derivedFrom":[makeQuery(id+"F14.boolean.opBoolean","MERGE",FACE,{"derivedFrom":[makeQuery(id+"F12.boolean.opBoolean","MERGE",FACE,{"derivedFrom":[makeQuery(id+"F1.opExtrude","SWEPT_FACE",FACE,{"disambiguationData":[OSD([subQ0])]}),makeQuery(id+"F12.opExtrude","CAP_FACE",FACE,{"disambiguationData":[OSD([subQ0,sQuery(id+"F11.wireOp",EDGE,"E544"),sQuery(id+"F11.wireOp",EDGE,"E545"),sQuery(id+"F11.wireOp",EDGE,"E546"),sQuery(id+"F11.wireOp",EDGE,"E547"),sQuery(id+"F11.wireOp",EDGE,"E548"),sQuery(id+"F11.wireOp",EDGE,"E549"),sQuery(id+"F11.wireOp",EDGE,"E550"),sQuery(id+"F11.wireOp",EDGE,"E552.MirrorCS"),sQuery(id+"F11.wireOp",EDGE,"E553.MirrorCS"),sQuery(id+"F11.wireOp",EDGE,"E554.MirrorCS"),sQuery(id+"F11.wireOp",EDGE,"E555.MirrorCS"),sQuery(id+"F11.wireOp",EDGE,"E556.MirrorCS"),sQuery(id+"F11.wireOp",EDGE,"E557.MirrorCS"),sQuery(id+"F11.wireOp",EDGE,"E558"),sQuery(id+"F11.wireOp",EDGE,"E560.MirrorCS"),sQuery(id+"F11.wireOp",EDGE,"E561.MirrorCS"),sQuery(id+"F11.wireOp",EDGE,"E562.MirrorCS"),sQuery(id+"F11.wireOp",EDGE,"E563.MirrorCS"),sQuery(id+"F11.wireOp",EDGE,"E564.MirrorCS"),sQuery(id+"F11.wireOp",EDGE,"E565.MirrorCS"),sQuery(id+"F11.wireOp",EDGE,"E566"),sQuery(id+"F11.wireOp",EDGE,"E567.MirrorCS"),sQuery(id+"F11.wireOp",EDGE,"E568.MirrorCS")])],"isStart":true})]}),makeQuery(id+"F14.opExtrude","SWEPT_FACE",FACE,{"disambiguationData":[OSD([subQ1])]})]}),makeQuery(id+"F16.opExtrude","CAP_FACE",FACE,{"disambiguationData":[OSD([subQ1,sQuery(id+"F15.wireOp",EDGE,"E574"),sQuery(id+"F15.wireOp",EDGE,"E575"),sQuery(id+"F15.wireOp",EDGE,"E576"),sQuery(id+"F15.wireOp",EDGE,"E577"),sQuery(id+"F15.wireOp",EDGE,"E578")])],"isStart":true}),makeQuery(id+"F16.opExtrude","CAP_FACE",FACE,{"disambiguationData":[OSD([subQ0,sQuery(id+"F15.wireOp",EDGE,"E579.MirrorCS"),sQuery(id+"F15.wireOp",EDGE,"E580.MirrorCS"),sQuery(id+"F15.wireOp",EDGE,"E581.MirrorCS"),sQuery(id+"F15.wireOp",EDGE,"E582.MirrorCS"),sQuery(id+"F15.wireOp",EDGE,"E583.MirrorCS")])],"isStart":true})]});}
            var sketch = newSketch(context, id + "F22", { "sketchPlane" : qUnion([Q0])});
            skLineSegment(sketch, "E586", {"start": v(67.28, 0) * mm, "end": v(57.61, 5.08) * mm});
            skLineSegment(sketch, "E587", {"start": v(67.28, 19.68) * mm, "end": v(57.61, 14.6) * mm});
            skSolve(sketch);
        }
        {
            var Q0;
            Q0 = qSketchRegion(id + "F22", true);
            var Q1;
            {var subQ0=sQuery(id+"F22.wireOp",EDGE,"E586");Q1=makeQuery(id+"F22.imprint","IMPRINT",FACE,{"disambiguationData":[TD([[makeQuery(id+"F22.imprint","IMPRINT",EDGE,{"derivedFrom":subQ0}),-1.0]])]});}
            var Q2;
            {var subQ0=sQuery(id+"F22.wireOp",EDGE,"E587");Q2=makeQuery(id+"F22.imprint","IMPRINT",FACE,{"disambiguationData":[TD([[makeQuery(id+"F22.imprint","IMPRINT",EDGE,{"derivedFrom":subQ0}),1.0]])]});}
            extrude(context, id + "F23", {"entities" : qUnion([Q0, Q1, Q2]), "operationType" : NewBodyOperationType.REMOVE, "oppositeDirection" : true, "depth" : 25 * mm, "offsetDistance" : 25 * mm});
        }
        {
            var Q0;
            {var subQ0=sQuery(id+"F0.wireOp",EDGE,"E59.right");var subQ1=sQuery(id+"F0.wireOp",EDGE,"E55.right");Q0=makeQuery(id+"F7.boolean.opBoolean","MERGE",FACE,{"derivedFrom":[makeQuery(id+"F5.boolean.opBoolean","MERGE",FACE,{"derivedFrom":[makeQuery(id+"F3.boolean.opBoolean","MERGE",FACE,{"derivedFrom":[makeQuery(id+"F1.opExtrude","SWEPT_FACE",FACE,{"disambiguationData":[OSD([sQuery(id+"F0.wireOp",EDGE,"E55.left"),sQuery(id+"F0.wireOp",EDGE,"E59.left")])]}),makeQuery(id+"F3.opExtrude","CAP_FACE",FACE,{"disambiguationData":[OSD([subQ1,subQ0,sQuery(id+"F2.wireOp",EDGE,"E502"),sQuery(id+"F2.wireOp",EDGE,"E503"),sQuery(id+"F2.wireOp",EDGE,"E504"),sQuery(id+"F2.wireOp",EDGE,"E505"),sQuery(id+"F2.wireOp",EDGE,"E506"),sQuery(id+"F2.wireOp",EDGE,"E507"),sQuery(id+"F2.wireOp",EDGE,"E508"),sQuery(id+"F2.wireOp",EDGE,"E510.MirrorCS"),sQuery(id+"F2.wireOp",EDGE,"E511.MirrorCS"),sQuery(id+"F2.wireOp",EDGE,"E512.MirrorCS"),sQuery(id+"F2.wireOp",EDGE,"E513.MirrorCS"),sQuery(id+"F2.wireOp",EDGE,"E514.MirrorCS"),sQuery(id+"F2.wireOp",EDGE,"E515.MirrorCS"),sQuery(id+"F2.wireOp",EDGE,"E516.MirrorCS"),sQuery(id+"F2.wireOp",EDGE,"E517"),sQuery(id+"F2.wireOp",EDGE,"E519.MirrorCS"),sQuery(id+"F2.wireOp",EDGE,"E520.MirrorCS"),sQuery(id+"F2.wireOp",EDGE,"E521.MirrorCS"),sQuery(id+"F2.wireOp",EDGE,"E522.MirrorCS"),sQuery(id+"F2.wireOp",EDGE,"E523.MirrorCS"),sQuery(id+"F2.wireOp",EDGE,"E524.MirrorCS"),sQuery(id+"F2.wireOp",EDGE,"E525.MirrorCS"),sQuery(id+"F2.wireOp",EDGE,"E526")])],"isStart":false})]}),makeQuery(id+"F5.opExtrude","SWEPT_FACE",FACE,{"disambiguationData":[OSD([sQuery(id+"F4.wireOp",EDGE,"E529.5"),sQuery(id+"F4.wireOp",EDGE,"E529.6"),sQuery(id+"F4.wireOp",EDGE,"E530")])]})]}),makeQuery(id+"F7.opExtrude","CAP_FACE",FACE,{"disambiguationData":[OSD([sQuery(id+"F4.wireOp",EDGE,"E529.4"),sQuery(id+"F4.wireOp",EDGE,"E529.8"),sQuery(id+"F4.wireOp",EDGE,"E531"),sQuery(id+"F6.wireOp",EDGE,"E532"),sQuery(id+"F6.wireOp",EDGE,"E533"),sQuery(id+"F6.wireOp",EDGE,"E534"),sQuery(id+"F6.wireOp",EDGE,"E535"),sQuery(id+"F6.wireOp",EDGE,"E536")])],"isStart":false}),makeQuery(id+"F7.opExtrude","CAP_FACE",FACE,{"disambiguationData":[OSD([subQ1,subQ0,sQuery(id+"F6.wireOp",EDGE,"E538.MirrorCS"),sQuery(id+"F6.wireOp",EDGE,"E539.MirrorCS"),sQuery(id+"F6.wireOp",EDGE,"E540.MirrorCS"),sQuery(id+"F6.wireOp",EDGE,"E541.MirrorCS"),sQuery(id+"F6.wireOp",EDGE,"E542.MirrorCS")])],"isStart":false})]});}
            var sketch = newSketch(context, id + "F24", { "sketchPlane" : qUnion([Q0])});
            skLineSegment(sketch, "E588", {"start": v(49.03, 0) * mm, "end": v(38.9, 5.08) * mm});
            skSolve(sketch);
        }
        {
            var Q0;
            {var subQ0=sQuery(id+"F24.wireOp",EDGE,"E588");Q0=makeQuery(id+"F24.imprint","IMPRINT",FACE,{"disambiguationData":[TD([[makeQuery(id+"F24.imprint","IMPRINT",EDGE,{"derivedFrom":subQ0}),-1.0]])]});}
            extrude(context, id + "F25", {"entities" : qUnion([Q0]), "operationType" : NewBodyOperationType.REMOVE, "oppositeDirection" : true, "depth" : 25 * mm, "offsetDistance" : 25 * mm});
        }
        {
            var Q0;
            Q0=makeQuery(id+"F0.imprint","IMPRINT",FACE,{"disambiguationData":[TD([[makeQuery(id+"F0.imprint","IMPRINT",EDGE,{"derivedFrom":sQuery(id+"F0.wireOp",EDGE,"E123")}),-1.0]])]});
            var Q1;
            Q1=makeQuery(id+"F0.imprint","IMPRINT",FACE,{"disambiguationData":[TD([[makeQuery(id+"F0.imprint","IMPRINT",EDGE,{"derivedFrom":sQuery(id+"F0.wireOp",EDGE,"E125")}),-1.0]])]});
            extrude(context, id + "F26", {"entities" : qUnion([Q0, Q1]), "depth" : 5.08 * mm, "offsetDistance" : 25 * mm});
        }
        {
            var Q0;
            Q0=makeQuery(id+"F1.opExtrude","SWEPT_EDGE",EDGE,{"disambiguationData":[OSD([sQuery(id+"F0.wireOp",EDGE,"E229"),sQuery(id+"F0.wireOp",EDGE,"E251.MirrorCS")])]});
            var Q1;
            Q1=makeQuery(id+"F1.opExtrude","SWEPT_EDGE",EDGE,{"disambiguationData":[OSD([sQuery(id+"F0.wireOp",EDGE,"E229"),sQuery(id+"F0.wireOp",EDGE,"E250")])]});
            var Q2;
            Q2=makeQuery(id+"F1.opExtrude","SWEPT_EDGE",EDGE,{"disambiguationData":[OSD([sQuery(id+"F0.wireOp",EDGE,"E224"),sQuery(id+"F0.wireOp",EDGE,"E250")])]});
            var Q3;
            Q3=makeQuery(id+"F1.opExtrude","SWEPT_EDGE",EDGE,{"disambiguationData":[OSD([sQuery(id+"F0.wireOp",EDGE,"E226"),sQuery(id+"F0.wireOp",EDGE,"E251.MirrorCS")])]});
            fillet(context, id + "F27", {"entities" : qUnion([Q0, Q1, Q2, Q3]), "radius" : 3 * mm, "tangentPropagation" : true, "allowEdgeOverflow" : false});
        }
        {
            var Q0;
            Q0=makeQuery(id+"F1.opExtrude","SWEPT_EDGE",EDGE,{"disambiguationData":[OSD([sQuery(id+"F0.wireOp",EDGE,"E368"),sQuery(id+"F0.wireOp",EDGE,"E369")])]});
            var Q1;
            Q1=makeQuery(id+"F1.opExtrude","SWEPT_EDGE",EDGE,{"disambiguationData":[OSD([sQuery(id+"F0.wireOp",EDGE,"E369"),sQuery(id+"F0.wireOp",EDGE,"E370")])]});
            var Q2;
            Q2=makeQuery(id+"F1.opExtrude","SWEPT_EDGE",EDGE,{"disambiguationData":[OSD([sQuery(id+"F0.wireOp",EDGE,"E331"),sQuery(id+"F0.wireOp",EDGE,"E332")])]});
            var Q3;
            Q3=makeQuery(id+"F1.opExtrude","SWEPT_EDGE",EDGE,{"disambiguationData":[OSD([sQuery(id+"F0.wireOp",EDGE,"E332"),sQuery(id+"F0.wireOp",EDGE,"E333")])]});
            fillet(context, id + "F28", {"entities" : qUnion([Q0, Q1, Q2, Q3]), "radius" : 3 * mm, "tangentPropagation" : true, "allowEdgeOverflow" : false});
        }
    });
